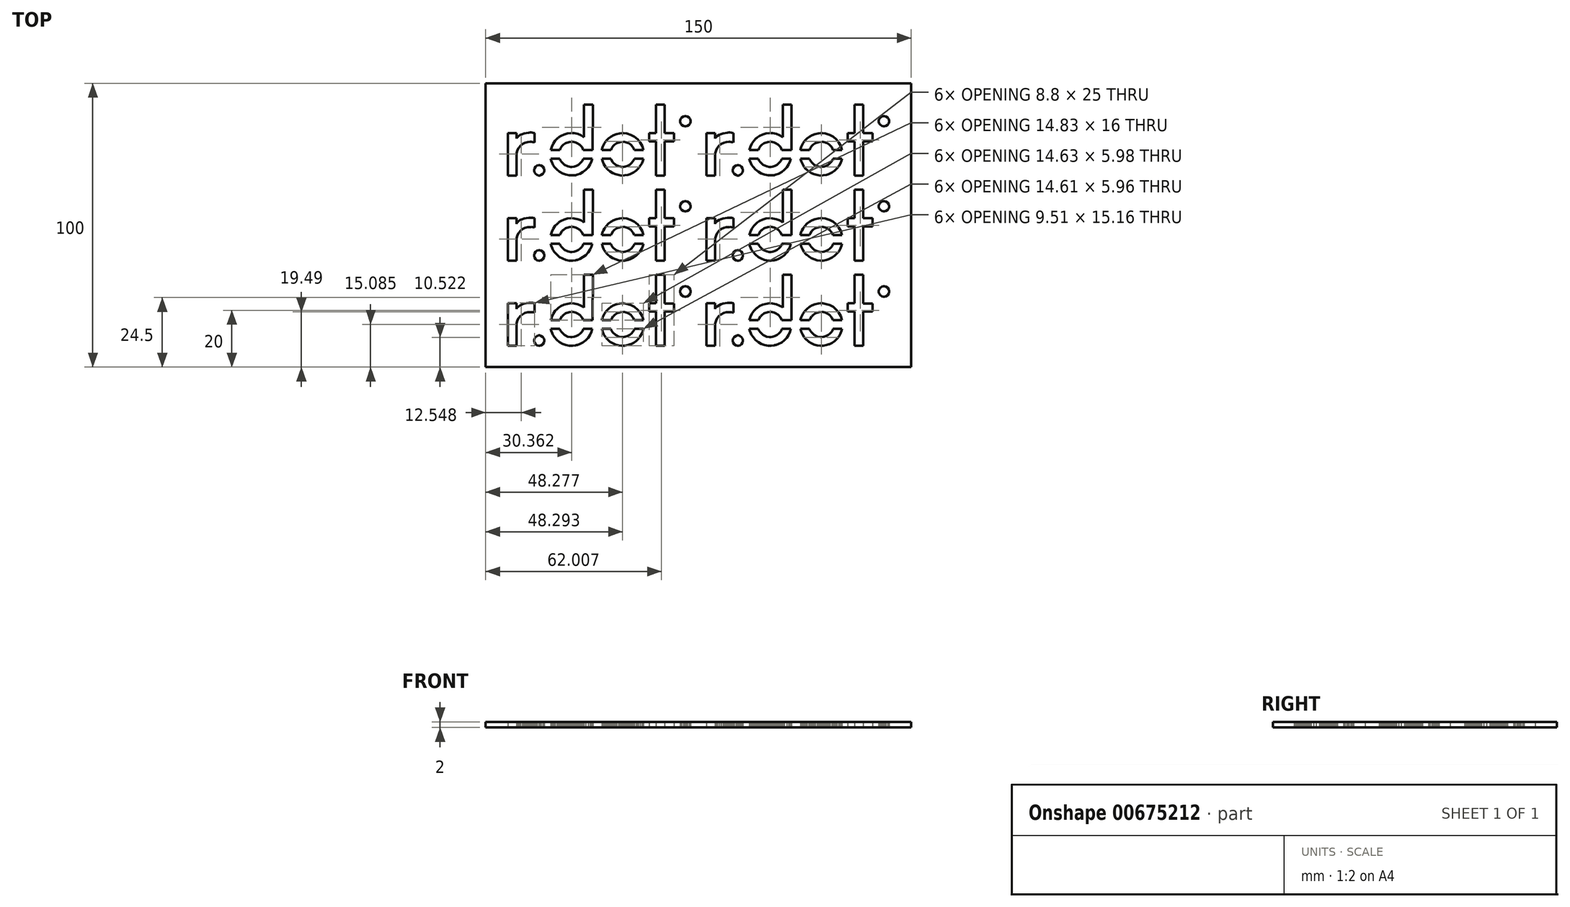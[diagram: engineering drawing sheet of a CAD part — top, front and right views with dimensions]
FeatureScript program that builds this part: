
annotation { "Feature Type Name" : "Feature", "Feature Type Description" : "" }
export const myFeature = defineFeature(function(context is Context, id is Id, definition is map)
    precondition{}
    {
        {
            var Q0;
            Q0=qCreatedBy(makeId("Top.planeOp"),FACE);
            var sketch = newSketch(context, id + "F0", { "sketchPlane" : qUnion([Q0])});
            skLineSegment(sketch, "E0", {"start": v(32.2, 6.66) * mm, "end": v(32.2, 6.49) * mm});
            skLineSegment(sketch, "E1", {"start": v(32.2, 6.49) * mm, "end": v(32.06, 5.96) * mm});
            skLineSegment(sketch, "E2", {"start": v(32.06, 5.96) * mm, "end": v(31.67, 5.38) * mm});
            skLineSegment(sketch, "E3", {"start": v(31.67, 5.38) * mm, "end": v(31.1, 5) * mm});
            skLineSegment(sketch, "E4", {"start": v(31.1, 5) * mm, "end": v(30.57, 4.85) * mm});
            skLineSegment(sketch, "E5", {"start": v(30.57, 4.85) * mm, "end": v(30.39, 4.85) * mm});
            skLineSegment(sketch, "E6", {"start": v(30.39, 4.85) * mm, "end": v(30.21, 4.85) * mm});
            skLineSegment(sketch, "E7", {"start": v(30.21, 4.85) * mm, "end": v(29.68, 5) * mm});
            skLineSegment(sketch, "E8", {"start": v(29.68, 5) * mm, "end": v(29.1, 5.38) * mm});
            skLineSegment(sketch, "E9", {"start": v(29.1, 5.38) * mm, "end": v(28.72, 5.96) * mm});
            skLineSegment(sketch, "E10", {"start": v(28.72, 5.96) * mm, "end": v(28.57, 6.49) * mm});
            skLineSegment(sketch, "E11", {"start": v(28.57, 6.49) * mm, "end": v(28.57, 6.66) * mm});
            skLineSegment(sketch, "E12", {"start": v(28.57, 6.66) * mm, "end": v(28.57, 6.84) * mm});
            skLineSegment(sketch, "E13", {"start": v(28.57, 6.84) * mm, "end": v(28.72, 7.37) * mm});
            skLineSegment(sketch, "E14", {"start": v(28.72, 7.37) * mm, "end": v(29.1, 7.95) * mm});
            skLineSegment(sketch, "E15", {"start": v(29.1, 7.95) * mm, "end": v(29.68, 8.34) * mm});
            skLineSegment(sketch, "E16", {"start": v(29.68, 8.34) * mm, "end": v(30.21, 8.48) * mm});
            skLineSegment(sketch, "E17", {"start": v(30.21, 8.48) * mm, "end": v(30.39, 8.48) * mm});
            skLineSegment(sketch, "E18", {"start": v(30.39, 8.48) * mm, "end": v(30.57, 8.48) * mm});
            skLineSegment(sketch, "E19", {"start": v(30.57, 8.48) * mm, "end": v(31.1, 8.34) * mm});
            skLineSegment(sketch, "E20", {"start": v(31.1, 8.34) * mm, "end": v(31.67, 7.95) * mm});
            skLineSegment(sketch, "E21", {"start": v(31.67, 7.95) * mm, "end": v(32.06, 7.37) * mm});
            skLineSegment(sketch, "E22", {"start": v(32.06, 7.37) * mm, "end": v(32.2, 6.84) * mm});
            skLineSegment(sketch, "E23", {"start": v(32.2, 6.84) * mm, "end": v(32.2, 6.66) * mm});
            skLineSegment(sketch, "E24", {"start": v(23.05, 12.5) * mm, "end": v(19.98, 12.5) * mm});
            skLineSegment(sketch, "E25", {"start": v(19.98, 12.5) * mm, "end": v(19.98, 2.51) * mm});
            skLineSegment(sketch, "E26", {"start": v(19.98, 2.51) * mm, "end": v(17.6, 2.51) * mm});
            skLineSegment(sketch, "E27", {"start": v(17.6, 2.51) * mm, "end": v(17.6, -0.42) * mm});
            skLineSegment(sketch, "E28", {"start": v(17.6, -0.42) * mm, "end": v(19.98, -0.42) * mm});
            skLineSegment(sketch, "E29", {"start": v(19.98, -0.42) * mm, "end": v(19.98, -12.5) * mm});
            skLineSegment(sketch, "E30", {"start": v(19.98, -12.5) * mm, "end": v(23.05, -12.5) * mm});
            skLineSegment(sketch, "E31", {"start": v(23.05, -12.5) * mm, "end": v(23.05, -0.42) * mm});
            skLineSegment(sketch, "E32", {"start": v(23.05, -0.42) * mm, "end": v(26.4, -0.42) * mm});
            skLineSegment(sketch, "E33", {"start": v(26.4, -0.42) * mm, "end": v(26.4, 2.44) * mm});
            skLineSegment(sketch, "E34", {"start": v(26.4, 2.44) * mm, "end": v(23.05, 2.44) * mm});
            skLineSegment(sketch, "E35", {"start": v(23.05, 2.44) * mm, "end": v(23.05, 12.5) * mm});
            skLineSegment(sketch, "E36", {"start": v(8.29, 2.48) * mm, "end": v(8, 2.48) * mm});
            skLineSegment(sketch, "E37", {"start": v(8, 2.48) * mm, "end": v(7.17, 2.4) * mm});
            skLineSegment(sketch, "E38", {"start": v(7.17, 2.4) * mm, "end": v(6.1, 2.15) * mm});
            skLineSegment(sketch, "E39", {"start": v(6.1, 2.15) * mm, "end": v(5.08, 1.76) * mm});
            skLineSegment(sketch, "E40", {"start": v(5.08, 1.76) * mm, "end": v(4.13, 1.22) * mm});
            skLineSegment(sketch, "E41", {"start": v(4.13, 1.22) * mm, "end": v(3.28, 0.55) * mm});
            skLineSegment(sketch, "E42", {"start": v(3.28, 0.55) * mm, "end": v(2.52, -0.23) * mm});
            skLineSegment(sketch, "E43", {"start": v(2.52, -0.23) * mm, "end": v(1.89, -1.13) * mm});
            skLineSegment(sketch, "E44", {"start": v(1.89, -1.13) * mm, "end": v(1.49, -1.87) * mm});
            skLineSegment(sketch, "E45", {"start": v(1.49, -1.87) * mm, "end": v(1.38, -2.13) * mm});
            skLineSegment(sketch, "E46", {"start": v(1.38, -2.13) * mm, "end": v(1.28, -2.4) * mm});
            skLineSegment(sketch, "E47", {"start": v(1.28, -2.4) * mm, "end": v(1.03, -3.2) * mm});
            skLineSegment(sketch, "E48", {"start": v(1.03, -3.2) * mm, "end": v(0.98, -3.5) * mm});
            skLineSegment(sketch, "E49", {"start": v(0.97, -6.5) * mm, "end": v(1.24, -7.5) * mm});
            skLineSegment(sketch, "E50", {"start": v(1.24, -7.5) * mm, "end": v(1.68, -8.5) * mm});
            skLineSegment(sketch, "E51", {"start": v(1.68, -8.5) * mm, "end": v(2.27, -9.43) * mm});
            skLineSegment(sketch, "E52", {"start": v(2.27, -9.43) * mm, "end": v(2.8, -10.08) * mm});
            skLineSegment(sketch, "E53", {"start": v(2.8, -10.08) * mm, "end": v(3, -10.28) * mm});
            skLineSegment(sketch, "E54", {"start": v(3, -10.28) * mm, "end": v(3.2, -10.47) * mm});
            skLineSegment(sketch, "E55", {"start": v(3.2, -10.47) * mm, "end": v(3.85, -11) * mm});
            skLineSegment(sketch, "E56", {"start": v(3.85, -11) * mm, "end": v(4.78, -11.6) * mm});
            skLineSegment(sketch, "E57", {"start": v(4.78, -11.6) * mm, "end": v(5.78, -12.03) * mm});
            skLineSegment(sketch, "E58", {"start": v(5.78, -12.03) * mm, "end": v(6.83, -12.32) * mm});
            skLineSegment(sketch, "E59", {"start": v(6.83, -12.32) * mm, "end": v(7.9, -12.46) * mm});
            skLineSegment(sketch, "E60", {"start": v(7.9, -12.46) * mm, "end": v(9, -12.43) * mm});
            skLineSegment(sketch, "E61", {"start": v(9, -12.43) * mm, "end": v(10.08, -12.25) * mm});
            skLineSegment(sketch, "E62", {"start": v(10.08, -12.25) * mm, "end": v(10.89, -12) * mm});
            skLineSegment(sketch, "E63", {"start": v(10.89, -12) * mm, "end": v(11.14, -11.9) * mm});
            skLineSegment(sketch, "E64", {"start": v(11.14, -11.9) * mm, "end": v(11.4, -11.79) * mm});
            skLineSegment(sketch, "E65", {"start": v(11.4, -11.79) * mm, "end": v(12.14, -11.4) * mm});
            skLineSegment(sketch, "E66", {"start": v(12.14, -11.4) * mm, "end": v(13.04, -10.75) * mm});
            skLineSegment(sketch, "E67", {"start": v(13.04, -10.75) * mm, "end": v(13.83, -10) * mm});
            skLineSegment(sketch, "E68", {"start": v(13.83, -10) * mm, "end": v(14.5, -9.14) * mm});
            skLineSegment(sketch, "E69", {"start": v(14.5, -9.14) * mm, "end": v(15.03, -8.2) * mm});
            skLineSegment(sketch, "E70", {"start": v(15.03, -8.2) * mm, "end": v(15.43, -7.18) * mm});
            skLineSegment(sketch, "E71", {"start": v(15.43, -7.18) * mm, "end": v(15.58, -6.5) * mm});
            skLineSegment(sketch, "E72", {"start": v(15.6, -3.5) * mm, "end": v(15.6, -3.49) * mm});
            skLineSegment(sketch, "E73", {"start": v(15.6, -3.49) * mm, "end": v(15.17, -2.08) * mm});
            skLineSegment(sketch, "E74", {"start": v(15.17, -2.08) * mm, "end": v(14.48, -0.82) * mm});
            skLineSegment(sketch, "E75", {"start": v(14.48, -0.82) * mm, "end": v(13.57, 0.3) * mm});
            skLineSegment(sketch, "E76", {"start": v(13.57, 0.3) * mm, "end": v(12.46, 1.2) * mm});
            skLineSegment(sketch, "E77", {"start": v(12.46, 1.2) * mm, "end": v(11.2, 1.9) * mm});
            skLineSegment(sketch, "E78", {"start": v(11.2, 1.9) * mm, "end": v(9.8, 2.33) * mm});
            skLineSegment(sketch, "E79", {"start": v(9.8, 2.33) * mm, "end": v(8.66, 2.48) * mm});
            skLineSegment(sketch, "E80", {"start": v(8.66, 2.48) * mm, "end": v(8.29, 2.48) * mm});
            skLineSegment(sketch, "E81", {"start": v(8.29, -9.43) * mm, "end": v(7.96, -9.43) * mm});
            skLineSegment(sketch, "E82", {"start": v(7.96, -9.43) * mm, "end": v(6.99, -9.23) * mm});
            skLineSegment(sketch, "E83", {"start": v(6.99, -9.23) * mm, "end": v(5.82, -8.68) * mm});
            skLineSegment(sketch, "E84", {"start": v(5.82, -8.68) * mm, "end": v(4.87, -7.82) * mm});
            skLineSegment(sketch, "E85", {"start": v(4.87, -7.82) * mm, "end": v(4.31, -6.99) * mm});
            skLineSegment(sketch, "E86", {"start": v(4.31, -6.99) * mm, "end": v(4.19, -6.69) * mm});
            skLineSegment(sketch, "E87", {"start": v(4.19, -6.69) * mm, "end": v(4.11, -6.5) * mm});
            skLineSegment(sketch, "E88", {"start": v(4.16, -3.5) * mm, "end": v(4.37, -2.91) * mm});
            skLineSegment(sketch, "E89", {"start": v(4.37, -2.91) * mm, "end": v(4.92, -2.09) * mm});
            skLineSegment(sketch, "E90", {"start": v(4.92, -2.09) * mm, "end": v(5.15, -1.86) * mm});
            skLineSegment(sketch, "E91", {"start": v(5.15, -1.86) * mm, "end": v(5.38, -1.63) * mm});
            skLineSegment(sketch, "E92", {"start": v(5.38, -1.63) * mm, "end": v(6.2, -1.08) * mm});
            skLineSegment(sketch, "E93", {"start": v(6.2, -1.08) * mm, "end": v(7.42, -0.64) * mm});
            skLineSegment(sketch, "E94", {"start": v(7.42, -0.64) * mm, "end": v(8.7, -0.58) * mm});
            skLineSegment(sketch, "E95", {"start": v(8.7, -0.58) * mm, "end": v(9.68, -0.77) * mm});
            skLineSegment(sketch, "E96", {"start": v(9.68, -0.77) * mm, "end": v(9.98, -0.9) * mm});
            skLineSegment(sketch, "E97", {"start": v(9.98, -0.9) * mm, "end": v(10.28, -1.02) * mm});
            skLineSegment(sketch, "E98", {"start": v(10.28, -1.02) * mm, "end": v(11.1, -1.57) * mm});
            skLineSegment(sketch, "E99", {"start": v(11.1, -1.57) * mm, "end": v(11.97, -2.53) * mm});
            skLineSegment(sketch, "E100", {"start": v(11.97, -2.53) * mm, "end": v(12.43, -3.5) * mm});
            skLineSegment(sketch, "E101", {"start": v(12.44, -6.5) * mm, "end": v(12.37, -6.72) * mm});
            skLineSegment(sketch, "E102", {"start": v(12.37, -6.72) * mm, "end": v(11.96, -7.47) * mm});
            skLineSegment(sketch, "E103", {"start": v(11.96, -7.47) * mm, "end": v(11.42, -8.13) * mm});
            skLineSegment(sketch, "E104", {"start": v(11.42, -8.13) * mm, "end": v(10.76, -8.67) * mm});
            skLineSegment(sketch, "E105", {"start": v(10.76, -8.67) * mm, "end": v(10.01, -9.08) * mm});
            skLineSegment(sketch, "E106", {"start": v(10.01, -9.08) * mm, "end": v(9.18, -9.34) * mm});
            skLineSegment(sketch, "E107", {"start": v(9.18, -9.34) * mm, "end": v(8.5, -9.43) * mm});
            skLineSegment(sketch, "E108", {"start": v(8.5, -9.43) * mm, "end": v(8.29, -9.43) * mm});
            skLineSegment(sketch, "E109", {"start": v(-2.22, 12.5) * mm, "end": v(-5.3, 12.5) * mm});
            skLineSegment(sketch, "E110", {"start": v(-5.3, 12.5) * mm, "end": v(-5.3, 1.02) * mm});
            skLineSegment(sketch, "E111", {"start": v(-5.3, 1.02) * mm, "end": v(-5.55, 1.21) * mm});
            skLineSegment(sketch, "E112", {"start": v(-5.55, 1.21) * mm, "end": v(-6.39, 1.69) * mm});
            skLineSegment(sketch, "E113", {"start": v(-6.39, 1.69) * mm, "end": v(-7.55, 2.15) * mm});
            skLineSegment(sketch, "E114", {"start": v(-7.55, 2.15) * mm, "end": v(-8.75, 2.42) * mm});
            skLineSegment(sketch, "E115", {"start": v(-8.75, 2.42) * mm, "end": v(-9.98, 2.48) * mm});
            skLineSegment(sketch, "E116", {"start": v(-9.98, 2.48) * mm, "end": v(-11.2, 2.33) * mm});
            skLineSegment(sketch, "E117", {"start": v(-11.2, 2.33) * mm, "end": v(-12.38, 2) * mm});
            skLineSegment(sketch, "E118", {"start": v(-12.38, 2) * mm, "end": v(-13.51, 1.45) * mm});
            skLineSegment(sketch, "E119", {"start": v(-13.51, 1.45) * mm, "end": v(-14.31, 0.92) * mm});
            skLineSegment(sketch, "E120", {"start": v(-14.31, 0.92) * mm, "end": v(-14.55, 0.71) * mm});
            skLineSegment(sketch, "E121", {"start": v(-14.55, 0.71) * mm, "end": v(-14.8, 0.5) * mm});
            skLineSegment(sketch, "E122", {"start": v(-14.8, 0.5) * mm, "end": v(-15.46, -0.19) * mm});
            skLineSegment(sketch, "E123", {"start": v(-15.46, -0.19) * mm, "end": v(-16.18, -1.21) * mm});
            skLineSegment(sketch, "E124", {"start": v(-16.18, -1.21) * mm, "end": v(-16.71, -2.32) * mm});
            skLineSegment(sketch, "E125", {"start": v(-16.71, -2.32) * mm, "end": v(-17.05, -3.5) * mm});
            skLineSegment(sketch, "E126", {"start": v(-17.02, -6.5) * mm, "end": v(-16.88, -7.18) * mm});
            skLineSegment(sketch, "E127", {"start": v(-16.88, -7.18) * mm, "end": v(-16.54, -8.08) * mm});
            skLineSegment(sketch, "E128", {"start": v(-16.54, -8.08) * mm, "end": v(-16.4, -8.36) * mm});
            skLineSegment(sketch, "E129", {"start": v(-16.4, -8.36) * mm, "end": v(-16.26, -8.65) * mm});
            skLineSegment(sketch, "E130", {"start": v(-16.26, -8.65) * mm, "end": v(-15.73, -9.45) * mm});
            skLineSegment(sketch, "E131", {"start": v(-15.73, -9.45) * mm, "end": v(-14.9, -10.39) * mm});
            skLineSegment(sketch, "E132", {"start": v(-14.9, -10.39) * mm, "end": v(-13.94, -11.16) * mm});
            skLineSegment(sketch, "E133", {"start": v(-13.94, -11.16) * mm, "end": v(-12.88, -11.77) * mm});
            skLineSegment(sketch, "E134", {"start": v(-12.88, -11.77) * mm, "end": v(-11.73, -12.2) * mm});
            skLineSegment(sketch, "E135", {"start": v(-11.73, -12.2) * mm, "end": v(-10.51, -12.42) * mm});
            skLineSegment(sketch, "E136", {"start": v(-10.51, -12.42) * mm, "end": v(-9.26, -12.45) * mm});
            skLineSegment(sketch, "E137", {"start": v(-9.26, -12.45) * mm, "end": v(-8.3, -12.34) * mm});
            skLineSegment(sketch, "E138", {"start": v(-8.3, -12.34) * mm, "end": v(-8, -12.26) * mm});
            skLineSegment(sketch, "E139", {"start": v(-8, -12.26) * mm, "end": v(-7.7, -12.19) * mm});
            skLineSegment(sketch, "E140", {"start": v(-7.7, -12.19) * mm, "end": v(-6.79, -11.86) * mm});
            skLineSegment(sketch, "E141", {"start": v(-6.79, -11.86) * mm, "end": v(-5.68, -11.27) * mm});
            skLineSegment(sketch, "E142", {"start": v(-5.68, -11.27) * mm, "end": v(-4.7, -10.52) * mm});
            skLineSegment(sketch, "E143", {"start": v(-4.7, -10.52) * mm, "end": v(-3.87, -9.62) * mm});
            skLineSegment(sketch, "E144", {"start": v(-3.87, -9.62) * mm, "end": v(-3.19, -8.6) * mm});
            skLineSegment(sketch, "E145", {"start": v(-3.19, -8.6) * mm, "end": v(-2.68, -7.48) * mm});
            skLineSegment(sketch, "E146", {"start": v(-2.68, -7.48) * mm, "end": v(-2.43, -6.5) * mm});
            skLineSegment(sketch, "E147", {"start": v(-2.26, -3.5) * mm, "end": v(-2.22, 12.5) * mm});
            skLineSegment(sketch, "E148", {"start": v(-9.73, -9.43) * mm, "end": v(-10.06, -9.43) * mm});
            skLineSegment(sketch, "E149", {"start": v(-10.06, -9.43) * mm, "end": v(-11.03, -9.24) * mm});
            skLineSegment(sketch, "E150", {"start": v(-11.03, -9.24) * mm, "end": v(-12.2, -8.68) * mm});
            skLineSegment(sketch, "E151", {"start": v(-12.2, -8.68) * mm, "end": v(-13.15, -7.82) * mm});
            skLineSegment(sketch, "E152", {"start": v(-13.15, -7.82) * mm, "end": v(-13.7, -7) * mm});
            skLineSegment(sketch, "E153", {"start": v(-13.7, -7) * mm, "end": v(-13.83, -6.7) * mm});
            skLineSegment(sketch, "E154", {"start": v(-13.83, -6.7) * mm, "end": v(-13.95, -6.4) * mm});
            skLineSegment(sketch, "E155", {"start": v(-13.85, -3.5) * mm, "end": v(-13.65, -2.92) * mm});
            skLineSegment(sketch, "E156", {"start": v(-13.65, -2.92) * mm, "end": v(-13.1, -2.1) * mm});
            skLineSegment(sketch, "E157", {"start": v(-13.1, -2.1) * mm, "end": v(-12.87, -1.86) * mm});
            skLineSegment(sketch, "E158", {"start": v(-12.87, -1.86) * mm, "end": v(-12.64, -1.63) * mm});
            skLineSegment(sketch, "E159", {"start": v(-12.64, -1.63) * mm, "end": v(-11.8, -1.08) * mm});
            skLineSegment(sketch, "E160", {"start": v(-11.8, -1.08) * mm, "end": v(-10.6, -0.65) * mm});
            skLineSegment(sketch, "E161", {"start": v(-10.6, -0.65) * mm, "end": v(-9.3, -0.58) * mm});
            skLineSegment(sketch, "E162", {"start": v(-9.3, -0.58) * mm, "end": v(-8.33, -0.78) * mm});
            skLineSegment(sketch, "E163", {"start": v(-8.33, -0.78) * mm, "end": v(-8.03, -0.9) * mm});
            skLineSegment(sketch, "E164", {"start": v(-8.03, -0.9) * mm, "end": v(-7.73, -1.02) * mm});
            skLineSegment(sketch, "E165", {"start": v(-7.73, -1.02) * mm, "end": v(-6.9, -1.58) * mm});
            skLineSegment(sketch, "E166", {"start": v(-6.9, -1.58) * mm, "end": v(-6.04, -2.53) * mm});
            skLineSegment(sketch, "E167", {"start": v(-6.04, -2.53) * mm, "end": v(-5.58, -3.5) * mm});
            skLineSegment(sketch, "E168", {"start": v(-5.58, -6.5) * mm, "end": v(-5.65, -6.72) * mm});
            skLineSegment(sketch, "E169", {"start": v(-5.65, -6.72) * mm, "end": v(-6.06, -7.47) * mm});
            skLineSegment(sketch, "E170", {"start": v(-6.06, -7.47) * mm, "end": v(-6.6, -8.13) * mm});
            skLineSegment(sketch, "E171", {"start": v(-6.6, -8.13) * mm, "end": v(-7.25, -8.67) * mm});
            skLineSegment(sketch, "E172", {"start": v(-7.25, -8.67) * mm, "end": v(-8, -9.08) * mm});
            skLineSegment(sketch, "E173", {"start": v(-8, -9.08) * mm, "end": v(-8.84, -9.34) * mm});
            skLineSegment(sketch, "E174", {"start": v(-8.84, -9.34) * mm, "end": v(-9.5, -9.43) * mm});
            skLineSegment(sketch, "E175", {"start": v(-9.5, -9.43) * mm, "end": v(-9.73, -9.43) * mm});
            skLineSegment(sketch, "E176", {"start": v(-9.73, -9.43) * mm, "end": v(-9.73, -9.43) * mm});
            skLineSegment(sketch, "E177", {"start": v(-19.3, -10.65) * mm, "end": v(-19.3, -10.83) * mm});
            skLineSegment(sketch, "E178", {"start": v(-19.3, -10.83) * mm, "end": v(-19.44, -11.36) * mm});
            skLineSegment(sketch, "E179", {"start": v(-19.44, -11.36) * mm, "end": v(-19.83, -11.93) * mm});
            skLineSegment(sketch, "E180", {"start": v(-19.83, -11.93) * mm, "end": v(-20.4, -12.32) * mm});
            skLineSegment(sketch, "E181", {"start": v(-20.4, -12.32) * mm, "end": v(-20.94, -12.47) * mm});
            skLineSegment(sketch, "E182", {"start": v(-20.94, -12.47) * mm, "end": v(-21.11, -12.47) * mm});
            skLineSegment(sketch, "E183", {"start": v(-21.11, -12.47) * mm, "end": v(-21.29, -12.47) * mm});
            skLineSegment(sketch, "E184", {"start": v(-21.29, -12.47) * mm, "end": v(-21.82, -12.32) * mm});
            skLineSegment(sketch, "E185", {"start": v(-21.82, -12.32) * mm, "end": v(-22.4, -11.93) * mm});
            skLineSegment(sketch, "E186", {"start": v(-22.4, -11.93) * mm, "end": v(-22.79, -11.36) * mm});
            skLineSegment(sketch, "E187", {"start": v(-22.79, -11.36) * mm, "end": v(-22.93, -10.83) * mm});
            skLineSegment(sketch, "E188", {"start": v(-22.93, -10.83) * mm, "end": v(-22.93, -10.65) * mm});
            skLineSegment(sketch, "E189", {"start": v(-22.93, -10.65) * mm, "end": v(-22.93, -10.47) * mm});
            skLineSegment(sketch, "E190", {"start": v(-22.93, -10.47) * mm, "end": v(-22.79, -9.94) * mm});
            skLineSegment(sketch, "E191", {"start": v(-22.79, -9.94) * mm, "end": v(-22.4, -9.37) * mm});
            skLineSegment(sketch, "E192", {"start": v(-22.4, -9.37) * mm, "end": v(-21.82, -8.98) * mm});
            skLineSegment(sketch, "E193", {"start": v(-21.82, -8.98) * mm, "end": v(-21.29, -8.83) * mm});
            skLineSegment(sketch, "E194", {"start": v(-21.29, -8.83) * mm, "end": v(-21.11, -8.83) * mm});
            skLineSegment(sketch, "E195", {"start": v(-21.11, -8.83) * mm, "end": v(-20.94, -8.83) * mm});
            skLineSegment(sketch, "E196", {"start": v(-20.94, -8.83) * mm, "end": v(-20.4, -8.98) * mm});
            skLineSegment(sketch, "E197", {"start": v(-20.4, -8.98) * mm, "end": v(-19.83, -9.37) * mm});
            skLineSegment(sketch, "E198", {"start": v(-19.83, -9.37) * mm, "end": v(-19.44, -9.94) * mm});
            skLineSegment(sketch, "E199", {"start": v(-19.44, -9.94) * mm, "end": v(-19.3, -10.47) * mm});
            skLineSegment(sketch, "E200", {"start": v(-19.3, -10.47) * mm, "end": v(-19.3, -10.65) * mm});
            skLineSegment(sketch, "E201", {"start": v(-22.7, -0.77) * mm, "end": v(-22.81, -0.75) * mm});
            skLineSegment(sketch, "E202", {"start": v(-22.81, -0.75) * mm, "end": v(-23.38, -0.65) * mm});
            skLineSegment(sketch, "E203", {"start": v(-23.38, -0.65) * mm, "end": v(-23.96, -0.61) * mm});
            skLineSegment(sketch, "E204", {"start": v(-23.96, -0.61) * mm, "end": v(-24.08, -0.61) * mm});
            skLineSegment(sketch, "E205", {"start": v(-24.08, -0.61) * mm, "end": v(-24.35, -0.61) * mm});
            skLineSegment(sketch, "E206", {"start": v(-24.35, -0.61) * mm, "end": v(-25.16, -0.7) * mm});
            skLineSegment(sketch, "E207", {"start": v(-25.16, -0.7) * mm, "end": v(-26.13, -0.94) * mm});
            skLineSegment(sketch, "E208", {"start": v(-26.13, -0.94) * mm, "end": v(-27, -1.35) * mm});
            skLineSegment(sketch, "E209", {"start": v(-27, -1.35) * mm, "end": v(-27.74, -1.93) * mm});
            skLineSegment(sketch, "E210", {"start": v(-27.74, -1.93) * mm, "end": v(-28.34, -2.69) * mm});
            skLineSegment(sketch, "E211", {"start": v(-28.34, -2.69) * mm, "end": v(-28.8, -3.62) * mm});
            skLineSegment(sketch, "E212", {"start": v(-28.8, -3.62) * mm, "end": v(-29.07, -4.74) * mm});
            skLineSegment(sketch, "E213", {"start": v(-29.07, -4.74) * mm, "end": v(-29.17, -5.72) * mm});
            skLineSegment(sketch, "E214", {"start": v(-29.17, -5.72) * mm, "end": v(-29.17, -6.04) * mm});
            skLineSegment(sketch, "E215", {"start": v(-29.17, -6.04) * mm, "end": v(-29.17, -12.5) * mm});
            skLineSegment(sketch, "E216", {"start": v(-29.17, -12.5) * mm, "end": v(-32.2, -12.5) * mm});
            skLineSegment(sketch, "E217", {"start": v(-32.2, -12.5) * mm, "end": v(-32.2, 2.47) * mm});
            skLineSegment(sketch, "E218", {"start": v(-32.2, 2.47) * mm, "end": v(-29.17, 2.47) * mm});
            skLineSegment(sketch, "E219", {"start": v(-29.17, 2.47) * mm, "end": v(-29.17, 0.52) * mm});
            skLineSegment(sketch, "E220", {"start": v(-29.17, 0.52) * mm, "end": v(-29.1, 0.65) * mm});
            skLineSegment(sketch, "E221", {"start": v(-29.1, 0.65) * mm, "end": v(-28.84, 1) * mm});
            skLineSegment(sketch, "E222", {"start": v(-28.84, 1) * mm, "end": v(-28.37, 1.44) * mm});
            skLineSegment(sketch, "E223", {"start": v(-28.37, 1.44) * mm, "end": v(-27.79, 1.8) * mm});
            skLineSegment(sketch, "E224", {"start": v(-27.79, 1.8) * mm, "end": v(-27.12, 2.1) * mm});
            skLineSegment(sketch, "E225", {"start": v(-27.12, 2.1) * mm, "end": v(-26.39, 2.35) * mm});
            skLineSegment(sketch, "E226", {"start": v(-26.39, 2.35) * mm, "end": v(-25.62, 2.52) * mm});
            skLineSegment(sketch, "E227", {"start": v(-25.62, 2.52) * mm, "end": v(-24.84, 2.63) * mm});
            skLineSegment(sketch, "E228", {"start": v(-24.84, 2.63) * mm, "end": v(-24.27, 2.66) * mm});
            skLineSegment(sketch, "E229", {"start": v(-24.27, 2.66) * mm, "end": v(-24.08, 2.66) * mm});
            skLineSegment(sketch, "E230", {"start": v(-24.08, 2.66) * mm, "end": v(-23.9, 2.66) * mm});
            skLineSegment(sketch, "E231", {"start": v(-23.9, 2.66) * mm, "end": v(-23.33, 2.61) * mm});
            skLineSegment(sketch, "E232", {"start": v(-23.33, 2.61) * mm, "end": v(-22.8, 2.48) * mm});
            skLineSegment(sketch, "E233", {"start": v(-22.8, 2.48) * mm, "end": v(-22.7, 2.44) * mm});
            skLineSegment(sketch, "E234", {"start": v(-22.7, 2.44) * mm, "end": v(-22.7, -0.77) * mm});
            skLineSegment(sketch, "E235", {"start": v(-17.02, -6.5) * mm, "end": v(-13.9, -6.5) * mm});
            skLineSegment(sketch, "E236", {"start": v(-17.05, -3.5) * mm, "end": v(-13.85, -3.5) * mm});
            skLineSegment(sketch, "E237.trimOffspring", {"start": v(-5.58, -6.5) * mm, "end": v(-2.43, -6.5) * mm});
            skLineSegment(sketch, "E238.trimOffspring", {"start": v(-5.58, -3.5) * mm, "end": v(-2.26, -3.5) * mm});
            skLineSegment(sketch, "E239.trimOffspring", {"start": v(12.43, -3.5) * mm, "end": v(15.6, -3.5) * mm});
            skLineSegment(sketch, "E240.trimOffspring", {"start": v(12.44, -6.5) * mm, "end": v(15.58, -6.5) * mm});
            skLineSegment(sketch, "E241.trimOffspring", {"start": v(0.98, -3.5) * mm, "end": v(4.16, -3.5) * mm});
            skLineSegment(sketch, "E242.trimOffspring", {"start": v(0.97, -6.5) * mm, "end": v(4.11, -6.5) * mm});
            skLineSegment(sketch, "E243.0.1.0", {"start": v(19.98, 29.58) * mm, "end": v(19.98, 17.5) * mm});
            skLineSegment(sketch, "E243.0.1.1", {"start": v(19.98, 42.5) * mm, "end": v(19.98, 32.51) * mm});
            skLineSegment(sketch, "E243.0.1.2", {"start": v(-22.7, 32.44) * mm, "end": v(-22.7, 29.23) * mm});
            skLineSegment(sketch, "E243.0.1.3", {"start": v(26.4, 29.58) * mm, "end": v(26.4, 32.44) * mm});
            skLineSegment(sketch, "E243.0.1.4", {"start": v(26.4, 32.44) * mm, "end": v(23.05, 32.44) * mm});
            skLineSegment(sketch, "E243.0.1.5", {"start": v(12.43, 26.5) * mm, "end": v(15.6, 26.5) * mm});
            skLineSegment(sketch, "E243.0.1.6", {"start": v(-17.05, 26.5) * mm, "end": v(-13.85, 26.5) * mm});
            skLineSegment(sketch, "E243.0.1.7", {"start": v(-32.2, 17.5) * mm, "end": v(-32.2, 32.47) * mm});
            skLineSegment(sketch, "E243.0.1.8", {"start": v(-29.17, 23.96) * mm, "end": v(-29.17, 17.5) * mm});
            skLineSegment(sketch, "E243.0.1.9", {"start": v(0.98, 26.5) * mm, "end": v(4.16, 26.5) * mm});
            skLineSegment(sketch, "E243.0.1.10", {"start": v(0.97, 23.5) * mm, "end": v(4.11, 23.5) * mm});
            skLineSegment(sketch, "E243.0.1.11", {"start": v(12.44, 23.5) * mm, "end": v(15.58, 23.5) * mm});
            skLineSegment(sketch, "E243.0.1.12", {"start": v(-5.3, 42.5) * mm, "end": v(-5.3, 31.02) * mm});
            skLineSegment(sketch, "E243.0.1.13", {"start": v(23.05, 17.5) * mm, "end": v(23.05, 29.58) * mm});
            skLineSegment(sketch, "E243.0.1.14", {"start": v(-32.2, 32.47) * mm, "end": v(-29.17, 32.47) * mm});
            skLineSegment(sketch, "E243.0.1.15", {"start": v(-29.17, 17.5) * mm, "end": v(-32.2, 17.5) * mm});
            skLineSegment(sketch, "E243.0.1.16", {"start": v(17.6, 32.51) * mm, "end": v(17.6, 29.58) * mm});
            skLineSegment(sketch, "E243.0.1.17", {"start": v(-2.26, 26.5) * mm, "end": v(-2.22, 42.5) * mm});
            skLineSegment(sketch, "E243.0.1.18", {"start": v(-2.22, 42.5) * mm, "end": v(-5.3, 42.5) * mm});
            skLineSegment(sketch, "E243.0.1.19", {"start": v(19.98, 17.5) * mm, "end": v(23.05, 17.5) * mm});
            skLineSegment(sketch, "E243.0.1.20", {"start": v(-5.58, 23.5) * mm, "end": v(-2.43, 23.5) * mm});
            skLineSegment(sketch, "E243.0.1.21", {"start": v(-17.02, 23.5) * mm, "end": v(-13.9, 23.5) * mm});
            skLineSegment(sketch, "E243.0.1.22", {"start": v(23.05, 42.5) * mm, "end": v(19.98, 42.5) * mm});
            skLineSegment(sketch, "E243.0.1.23", {"start": v(23.05, 32.44) * mm, "end": v(23.05, 42.5) * mm});
            skLineSegment(sketch, "E243.0.1.24", {"start": v(-5.58, 26.5) * mm, "end": v(-2.26, 26.5) * mm});
            skLineSegment(sketch, "E243.0.1.25", {"start": v(23.05, 29.58) * mm, "end": v(26.4, 29.58) * mm});
            skLineSegment(sketch, "E243.0.1.26", {"start": v(-4.7, 19.48) * mm, "end": v(-3.87, 20.38) * mm});
            skLineSegment(sketch, "E243.0.1.27", {"start": v(-16.71, 27.68) * mm, "end": v(-17.05, 26.5) * mm});
            skLineSegment(sketch, "E243.0.1.28", {"start": v(29.1, 37.95) * mm, "end": v(29.68, 38.34) * mm});
            skLineSegment(sketch, "E243.0.1.29", {"start": v(-13.83, 23.3) * mm, "end": v(-13.95, 23.6) * mm});
            skLineSegment(sketch, "E243.0.1.30", {"start": v(5.82, 21.32) * mm, "end": v(4.87, 22.18) * mm});
            skLineSegment(sketch, "E243.0.1.31", {"start": v(-3.19, 21.4) * mm, "end": v(-2.68, 22.52) * mm});
            skLineSegment(sketch, "E243.0.1.32", {"start": v(17.6, 29.58) * mm, "end": v(19.98, 29.58) * mm});
            skLineSegment(sketch, "E243.0.1.33", {"start": v(-6.79, 18.14) * mm, "end": v(-5.68, 18.73) * mm});
            skLineSegment(sketch, "E243.0.1.34", {"start": v(7.42, 29.36) * mm, "end": v(8.7, 29.42) * mm});
            skLineSegment(sketch, "E243.0.1.35", {"start": v(4.78, 18.4) * mm, "end": v(5.78, 17.97) * mm});
            skLineSegment(sketch, "E243.0.1.36", {"start": v(-6.06, 22.53) * mm, "end": v(-6.6, 21.87) * mm});
            skLineSegment(sketch, "E243.0.1.37", {"start": v(15.17, 27.92) * mm, "end": v(14.48, 29.18) * mm});
            skLineSegment(sketch, "E243.0.1.38", {"start": v(14.5, 20.86) * mm, "end": v(15.03, 21.8) * mm});
            skLineSegment(sketch, "E243.0.1.39", {"start": v(1.68, 21.5) * mm, "end": v(2.27, 20.57) * mm});
            skLineSegment(sketch, "E243.0.1.40", {"start": v(-27.74, 28.07) * mm, "end": v(-28.34, 27.31) * mm});
            skLineSegment(sketch, "E243.0.1.41", {"start": v(-27, 28.65) * mm, "end": v(-27.74, 28.07) * mm});
            skLineSegment(sketch, "E243.0.1.42", {"start": v(-3.87, 20.38) * mm, "end": v(-3.19, 21.4) * mm});
            skLineSegment(sketch, "E243.0.1.43", {"start": v(9.8, 32.33) * mm, "end": v(8.66, 32.48) * mm});
            skLineSegment(sketch, "E243.0.1.44", {"start": v(-2.68, 22.52) * mm, "end": v(-2.43, 23.5) * mm});
            skLineSegment(sketch, "E243.0.1.45", {"start": v(-6.6, 21.87) * mm, "end": v(-7.25, 21.33) * mm});
            skLineSegment(sketch, "E243.0.1.46", {"start": v(14.48, 29.18) * mm, "end": v(13.57, 30.3) * mm});
            skLineSegment(sketch, "E243.0.1.47", {"start": v(19.98, 32.51) * mm, "end": v(17.6, 32.51) * mm});
            skLineSegment(sketch, "E243.0.1.48", {"start": v(-11.03, 20.76) * mm, "end": v(-12.2, 21.32) * mm});
            skLineSegment(sketch, "E243.0.1.49", {"start": v(31.67, 37.95) * mm, "end": v(32.06, 37.37) * mm});
            skLineSegment(sketch, "E243.0.1.50", {"start": v(6.99, 20.77) * mm, "end": v(5.82, 21.32) * mm});
            skLineSegment(sketch, "E243.0.1.51", {"start": v(1.24, 22.5) * mm, "end": v(1.68, 21.5) * mm});
            skLineSegment(sketch, "E243.0.1.52", {"start": v(-26.39, 32.35) * mm, "end": v(-25.62, 32.52) * mm});
            skLineSegment(sketch, "E243.0.1.53", {"start": v(11.14, 18.1) * mm, "end": v(11.4, 18.21) * mm});
            skLineSegment(sketch, "E243.0.1.54", {"start": v(5.15, 28.14) * mm, "end": v(5.38, 28.37) * mm});
            skLineSegment(sketch, "E243.0.1.55", {"start": v(-12.64, 28.37) * mm, "end": v(-11.8, 28.92) * mm});
            skLineSegment(sketch, "E243.0.1.56", {"start": v(-16.26, 21.35) * mm, "end": v(-15.73, 20.55) * mm});
            skLineSegment(sketch, "E243.0.1.57", {"start": v(-29.17, 30.52) * mm, "end": v(-29.1, 30.65) * mm});
            skLineSegment(sketch, "E243.0.1.58", {"start": v(10.01, 20.92) * mm, "end": v(9.18, 20.66) * mm});
            skLineSegment(sketch, "E243.0.1.59", {"start": v(3.28, 30.55) * mm, "end": v(2.52, 29.77) * mm});
            skLineSegment(sketch, "E243.0.1.60", {"start": v(5.78, 17.97) * mm, "end": v(6.83, 17.68) * mm});
            skLineSegment(sketch, "E243.0.1.61", {"start": v(15.03, 21.8) * mm, "end": v(15.43, 22.82) * mm});
            skLineSegment(sketch, "E243.0.1.62", {"start": v(-13.15, 22.18) * mm, "end": v(-13.7, 23) * mm});
            skLineSegment(sketch, "E243.0.1.63", {"start": v(11.42, 21.87) * mm, "end": v(10.76, 21.33) * mm});
            skLineSegment(sketch, "E243.0.1.64", {"start": v(-10.51, 17.58) * mm, "end": v(-9.26, 17.55) * mm});
            skLineSegment(sketch, "E243.0.1.65", {"start": v(11.97, 27.47) * mm, "end": v(12.43, 26.5) * mm});
            skLineSegment(sketch, "E243.0.1.66", {"start": v(-28.8, 26.38) * mm, "end": v(-29.07, 25.26) * mm});
            skLineSegment(sketch, "E243.0.1.67", {"start": v(10.28, 28.98) * mm, "end": v(11.1, 28.43) * mm});
            skLineSegment(sketch, "E243.0.1.68", {"start": v(9.98, 29.1) * mm, "end": v(10.28, 28.98) * mm});
            skLineSegment(sketch, "E243.0.1.69", {"start": v(-22.4, 20.63) * mm, "end": v(-21.82, 21.02) * mm});
            skLineSegment(sketch, "E243.0.1.70", {"start": v(-7.55, 32.15) * mm, "end": v(-8.75, 32.42) * mm});
            skLineSegment(sketch, "E243.0.1.71", {"start": v(10.08, 17.75) * mm, "end": v(10.89, 18) * mm});
            skLineSegment(sketch, "E243.0.1.72", {"start": v(9, 17.57) * mm, "end": v(10.08, 17.75) * mm});
            skLineSegment(sketch, "E243.0.1.73", {"start": v(-7.25, 21.33) * mm, "end": v(-8, 20.92) * mm});
            skLineSegment(sketch, "E243.0.1.74", {"start": v(5.38, 28.37) * mm, "end": v(6.2, 28.92) * mm});
            skLineSegment(sketch, "E243.0.1.75", {"start": v(4.13, 31.22) * mm, "end": v(3.28, 30.55) * mm});
            skLineSegment(sketch, "E243.0.1.76", {"start": v(6.83, 17.68) * mm, "end": v(7.9, 17.54) * mm});
            skLineSegment(sketch, "E243.0.1.77", {"start": v(-22.4, 18.07) * mm, "end": v(-22.79, 18.64) * mm});
            skLineSegment(sketch, "E243.0.1.78", {"start": v(6.1, 32.15) * mm, "end": v(5.08, 31.76) * mm});
            skLineSegment(sketch, "E243.0.1.79", {"start": v(-6.9, 28.42) * mm, "end": v(-6.04, 27.47) * mm});
            skLineSegment(sketch, "E243.0.1.80", {"start": v(5.08, 31.76) * mm, "end": v(4.13, 31.22) * mm});
            skLineSegment(sketch, "E243.0.1.81", {"start": v(-6.04, 27.47) * mm, "end": v(-5.58, 26.5) * mm});
            skLineSegment(sketch, "E243.0.1.82", {"start": v(-15.73, 20.55) * mm, "end": v(-14.9, 19.61) * mm});
            skLineSegment(sketch, "E243.0.1.83", {"start": v(-8.75, 32.42) * mm, "end": v(-9.98, 32.48) * mm});
            skLineSegment(sketch, "E243.0.1.84", {"start": v(13.04, 19.25) * mm, "end": v(13.83, 20) * mm});
            skLineSegment(sketch, "E243.0.1.85", {"start": v(-10.6, 29.35) * mm, "end": v(-9.3, 29.42) * mm});
            skLineSegment(sketch, "E243.0.1.86", {"start": v(-6.39, 31.69) * mm, "end": v(-7.55, 32.15) * mm});
            skLineSegment(sketch, "E243.0.1.87", {"start": v(0.97, 23.5) * mm, "end": v(1.24, 22.5) * mm});
            skLineSegment(sketch, "E243.0.1.88", {"start": v(10.76, 21.33) * mm, "end": v(10.01, 20.92) * mm});
            skLineSegment(sketch, "E243.0.1.89", {"start": v(3.85, 19) * mm, "end": v(4.78, 18.4) * mm});
            skLineSegment(sketch, "E243.0.1.90", {"start": v(13.83, 20) * mm, "end": v(14.5, 20.86) * mm});
            skLineSegment(sketch, "E243.0.1.91", {"start": v(-12.87, 28.14) * mm, "end": v(-12.64, 28.37) * mm});
            skLineSegment(sketch, "E243.0.1.92", {"start": v(-29.17, 32.47) * mm, "end": v(-29.17, 30.52) * mm});
            skLineSegment(sketch, "E243.0.1.93", {"start": v(-13.85, 26.5) * mm, "end": v(-13.65, 27.08) * mm});
            skLineSegment(sketch, "E243.0.1.94", {"start": v(4.92, 27.91) * mm, "end": v(5.15, 28.14) * mm});
            skLineSegment(sketch, "E243.0.1.95", {"start": v(-12.38, 32) * mm, "end": v(-13.51, 31.45) * mm});
            skLineSegment(sketch, "E243.0.1.96", {"start": v(-12.88, 18.23) * mm, "end": v(-11.73, 17.8) * mm});
            skLineSegment(sketch, "E243.0.1.97", {"start": v(-19.83, 18.07) * mm, "end": v(-20.4, 17.68) * mm});
            skLineSegment(sketch, "E243.0.1.98", {"start": v(29.1, 35.38) * mm, "end": v(28.72, 35.96) * mm});
            skLineSegment(sketch, "E243.0.1.99", {"start": v(11.4, 18.21) * mm, "end": v(12.14, 18.6) * mm});
            skLineSegment(sketch, "E243.0.1.100", {"start": v(-27.12, 32.1) * mm, "end": v(-26.39, 32.35) * mm});
            skLineSegment(sketch, "E243.0.1.101", {"start": v(6.2, 28.92) * mm, "end": v(7.42, 29.36) * mm});
            skLineSegment(sketch, "E243.0.1.102", {"start": v(7.9, 17.54) * mm, "end": v(9, 17.57) * mm});
            skLineSegment(sketch, "E243.0.1.103", {"start": v(-29.1, 30.65) * mm, "end": v(-28.84, 31) * mm});
            skLineSegment(sketch, "E243.0.1.104", {"start": v(-28.37, 31.44) * mm, "end": v(-27.79, 31.8) * mm});
            skLineSegment(sketch, "E243.0.1.105", {"start": v(-7.7, 17.81) * mm, "end": v(-6.79, 18.14) * mm});
            skLineSegment(sketch, "E243.0.1.106", {"start": v(7.17, 32.4) * mm, "end": v(6.1, 32.15) * mm});
            skLineSegment(sketch, "E243.0.1.107", {"start": v(-19.83, 20.63) * mm, "end": v(-19.44, 20.06) * mm});
            skLineSegment(sketch, "E243.0.1.108", {"start": v(4.16, 26.5) * mm, "end": v(4.37, 27.09) * mm});
            skLineSegment(sketch, "E243.0.1.109", {"start": v(-11.73, 17.8) * mm, "end": v(-10.51, 17.58) * mm});
            skLineSegment(sketch, "E243.0.1.110", {"start": v(-7.73, 28.98) * mm, "end": v(-6.9, 28.42) * mm});
            skLineSegment(sketch, "E243.0.1.111", {"start": v(12.14, 18.6) * mm, "end": v(13.04, 19.25) * mm});
            skLineSegment(sketch, "E243.0.1.112", {"start": v(1.03, 26.8) * mm, "end": v(0.98, 26.5) * mm});
            skLineSegment(sketch, "E243.0.1.113", {"start": v(31.67, 35.38) * mm, "end": v(31.1, 35) * mm});
            skLineSegment(sketch, "E243.0.1.114", {"start": v(-26.13, 29.06) * mm, "end": v(-27, 28.65) * mm});
            skLineSegment(sketch, "E243.0.1.115", {"start": v(-27.79, 31.8) * mm, "end": v(-27.12, 32.1) * mm});
            skLineSegment(sketch, "E243.0.1.116", {"start": v(-5.68, 18.73) * mm, "end": v(-4.7, 19.48) * mm});
            skLineSegment(sketch, "E243.0.1.117", {"start": v(11.2, 31.9) * mm, "end": v(9.8, 32.33) * mm});
            skLineSegment(sketch, "E243.0.1.118", {"start": v(-11.8, 28.92) * mm, "end": v(-10.6, 29.35) * mm});
            skLineSegment(sketch, "E243.0.1.119", {"start": v(-17.02, 23.5) * mm, "end": v(-16.88, 22.82) * mm});
            skLineSegment(sketch, "E243.0.1.120", {"start": v(8.7, 29.42) * mm, "end": v(9.68, 29.23) * mm});
            skLineSegment(sketch, "E243.0.1.121", {"start": v(10.89, 18) * mm, "end": v(11.14, 18.1) * mm});
            skLineSegment(sketch, "E243.0.1.122", {"start": v(9.68, 29.23) * mm, "end": v(9.98, 29.1) * mm});
            skLineSegment(sketch, "E243.0.1.123", {"start": v(12.46, 31.2) * mm, "end": v(11.2, 31.9) * mm});
            skLineSegment(sketch, "E243.0.1.124", {"start": v(13.57, 30.3) * mm, "end": v(12.46, 31.2) * mm});
            skLineSegment(sketch, "E243.0.1.125", {"start": v(-13.65, 27.08) * mm, "end": v(-13.1, 27.9) * mm});
            skLineSegment(sketch, "E243.0.1.126", {"start": v(-16.18, 28.79) * mm, "end": v(-16.71, 27.68) * mm});
            skLineSegment(sketch, "E243.0.1.127", {"start": v(-8, 20.92) * mm, "end": v(-8.84, 20.66) * mm});
            skLineSegment(sketch, "E243.0.1.128", {"start": v(-28.84, 31) * mm, "end": v(-28.37, 31.44) * mm});
            skLineSegment(sketch, "E243.0.1.129", {"start": v(4.37, 27.09) * mm, "end": v(4.92, 27.91) * mm});
            skLineSegment(sketch, "E243.0.1.130", {"start": v(-15.46, 29.81) * mm, "end": v(-16.18, 28.79) * mm});
            skLineSegment(sketch, "E243.0.1.131", {"start": v(11.96, 22.53) * mm, "end": v(11.42, 21.87) * mm});
            skLineSegment(sketch, "E243.0.1.132", {"start": v(-9.98, 32.48) * mm, "end": v(-11.2, 32.33) * mm});
            skLineSegment(sketch, "E243.0.1.133", {"start": v(-13.94, 18.84) * mm, "end": v(-12.88, 18.23) * mm});
            skLineSegment(sketch, "E243.0.1.134", {"start": v(-11.2, 32.33) * mm, "end": v(-12.38, 32) * mm});
            skLineSegment(sketch, "E243.0.1.135", {"start": v(11.1, 28.43) * mm, "end": v(11.97, 27.47) * mm});
            skLineSegment(sketch, "E243.0.1.136", {"start": v(-13.1, 27.9) * mm, "end": v(-12.87, 28.14) * mm});
            skLineSegment(sketch, "E243.0.1.137", {"start": v(-13.7, 23) * mm, "end": v(-13.83, 23.3) * mm});
            skLineSegment(sketch, "E243.0.1.138", {"start": v(2.52, 29.77) * mm, "end": v(1.89, 28.87) * mm});
            skLineSegment(sketch, "E243.0.1.139", {"start": v(15.43, 22.82) * mm, "end": v(15.58, 23.5) * mm});
            skLineSegment(sketch, "E243.0.1.140", {"start": v(-12.2, 21.32) * mm, "end": v(-13.15, 22.18) * mm});
            skLineSegment(sketch, "E243.0.1.141", {"start": v(-14.9, 19.61) * mm, "end": v(-13.94, 18.84) * mm});
            skLineSegment(sketch, "E243.0.1.142", {"start": v(-28.34, 27.31) * mm, "end": v(-28.8, 26.38) * mm});
            skLineSegment(sketch, "E243.0.1.143", {"start": v(28.72, 37.37) * mm, "end": v(29.1, 37.95) * mm});
            skLineSegment(sketch, "E243.0.1.144", {"start": v(15.6, 26.51) * mm, "end": v(15.17, 27.92) * mm});
            skLineSegment(sketch, "E243.0.1.145", {"start": v(-22.79, 20.06) * mm, "end": v(-22.4, 20.63) * mm});
            skLineSegment(sketch, "E243.0.1.146", {"start": v(29.68, 35) * mm, "end": v(29.1, 35.38) * mm});
            skLineSegment(sketch, "E243.0.1.147", {"start": v(1.28, 27.6) * mm, "end": v(1.03, 26.8) * mm});
            skLineSegment(sketch, "E243.0.1.148", {"start": v(-19.44, 18.64) * mm, "end": v(-19.83, 18.07) * mm});
            skLineSegment(sketch, "E243.0.1.149", {"start": v(-20.4, 21.02) * mm, "end": v(-19.83, 20.63) * mm});
            skLineSegment(sketch, "E243.0.1.150", {"start": v(31.1, 38.34) * mm, "end": v(31.67, 37.95) * mm});
            skLineSegment(sketch, "E243.0.1.151", {"start": v(-25.62, 32.52) * mm, "end": v(-24.84, 32.63) * mm});
            skLineSegment(sketch, "E243.0.1.152", {"start": v(32.06, 35.96) * mm, "end": v(31.67, 35.38) * mm});
            skLineSegment(sketch, "E243.0.1.153", {"start": v(-25.16, 29.3) * mm, "end": v(-26.13, 29.06) * mm});
            skLineSegment(sketch, "E243.0.1.154", {"start": v(-21.82, 17.68) * mm, "end": v(-22.4, 18.07) * mm});
            skLineSegment(sketch, "E243.0.1.155", {"start": v(3.2, 19.53) * mm, "end": v(3.85, 19) * mm});
            skLineSegment(sketch, "E243.0.1.156", {"start": v(-23.33, 32.61) * mm, "end": v(-22.8, 32.48) * mm});
            skLineSegment(sketch, "E243.0.1.157", {"start": v(8.29, 32.48) * mm, "end": v(8, 32.48) * mm});
            skLineSegment(sketch, "E243.0.1.158", {"start": v(-10.06, 20.57) * mm, "end": v(-11.03, 20.76) * mm});
            skLineSegment(sketch, "E243.0.1.159", {"start": v(8.66, 32.48) * mm, "end": v(8.29, 32.48) * mm});
            skLineSegment(sketch, "E243.0.1.160", {"start": v(29.68, 38.34) * mm, "end": v(30.21, 38.48) * mm});
            skLineSegment(sketch, "E243.0.1.161", {"start": v(8.5, 20.57) * mm, "end": v(8.29, 20.57) * mm});
            skLineSegment(sketch, "E243.0.1.162", {"start": v(1.89, 28.87) * mm, "end": v(1.49, 28.13) * mm});
            skLineSegment(sketch, "E243.0.1.163", {"start": v(-24.08, 32.66) * mm, "end": v(-23.9, 32.66) * mm});
            skLineSegment(sketch, "E243.0.1.164", {"start": v(-19.3, 19.53) * mm, "end": v(-19.3, 19.35) * mm});
            skLineSegment(sketch, "E243.0.1.165", {"start": v(2.8, 19.92) * mm, "end": v(3, 19.72) * mm});
            skLineSegment(sketch, "E243.0.1.166", {"start": v(30.21, 34.85) * mm, "end": v(29.68, 35) * mm});
            skLineSegment(sketch, "E243.0.1.167", {"start": v(-23.38, 29.35) * mm, "end": v(-23.96, 29.39) * mm});
            skLineSegment(sketch, "E243.0.1.168", {"start": v(-19.44, 20.06) * mm, "end": v(-19.3, 19.53) * mm});
            skLineSegment(sketch, "E243.0.1.169", {"start": v(30.21, 38.48) * mm, "end": v(30.39, 38.48) * mm});
            skLineSegment(sketch, "E243.0.1.170", {"start": v(9.18, 20.66) * mm, "end": v(8.5, 20.57) * mm});
            skLineSegment(sketch, "E243.0.1.171", {"start": v(-9.26, 17.55) * mm, "end": v(-8.3, 17.66) * mm});
            skLineSegment(sketch, "E243.0.1.172", {"start": v(-22.8, 32.48) * mm, "end": v(-22.7, 32.44) * mm});
            skLineSegment(sketch, "E243.0.1.173", {"start": v(-5.58, 23.5) * mm, "end": v(-5.65, 23.28) * mm});
            skLineSegment(sketch, "E243.0.1.174", {"start": v(-14.31, 30.92) * mm, "end": v(-14.55, 30.71) * mm});
            skLineSegment(sketch, "E243.0.1.175", {"start": v(-23.9, 32.66) * mm, "end": v(-23.33, 32.61) * mm});
            skLineSegment(sketch, "E243.0.1.176", {"start": v(-24.84, 32.63) * mm, "end": v(-24.27, 32.66) * mm});
            skLineSegment(sketch, "E243.0.1.177", {"start": v(-24.27, 32.66) * mm, "end": v(-24.08, 32.66) * mm});
            skLineSegment(sketch, "E243.0.1.178", {"start": v(-29.07, 25.26) * mm, "end": v(-29.17, 24.28) * mm});
            skLineSegment(sketch, "E243.0.1.179", {"start": v(30.57, 38.48) * mm, "end": v(31.1, 38.34) * mm});
            skLineSegment(sketch, "E243.0.1.180", {"start": v(7.96, 20.57) * mm, "end": v(6.99, 20.77) * mm});
            skLineSegment(sketch, "E243.0.1.181", {"start": v(-8.33, 29.22) * mm, "end": v(-8.03, 29.1) * mm});
            skLineSegment(sketch, "E243.0.1.182", {"start": v(-5.55, 31.21) * mm, "end": v(-6.39, 31.69) * mm});
            skLineSegment(sketch, "E243.0.1.183", {"start": v(-5.3, 31.02) * mm, "end": v(-5.55, 31.21) * mm});
            skLineSegment(sketch, "E243.0.1.184", {"start": v(-24.35, 29.39) * mm, "end": v(-25.16, 29.3) * mm});
            skLineSegment(sketch, "E243.0.1.185", {"start": v(30.39, 34.85) * mm, "end": v(30.21, 34.85) * mm});
            skLineSegment(sketch, "E243.0.1.186", {"start": v(30.57, 34.85) * mm, "end": v(30.39, 34.85) * mm});
            skLineSegment(sketch, "E243.0.1.187", {"start": v(4.19, 23.31) * mm, "end": v(4.11, 23.5) * mm});
            skLineSegment(sketch, "E243.0.1.188", {"start": v(-13.51, 31.45) * mm, "end": v(-14.31, 30.92) * mm});
            skLineSegment(sketch, "E243.0.1.189", {"start": v(-19.3, 19.35) * mm, "end": v(-19.3, 19.17) * mm});
            skLineSegment(sketch, "E243.0.1.190", {"start": v(-16.4, 21.64) * mm, "end": v(-16.26, 21.35) * mm});
            skLineSegment(sketch, "E243.0.1.191", {"start": v(-22.93, 19.17) * mm, "end": v(-22.93, 19.35) * mm});
            skLineSegment(sketch, "E243.0.1.192", {"start": v(-8.3, 17.66) * mm, "end": v(-8, 17.74) * mm});
            skLineSegment(sketch, "E243.0.1.193", {"start": v(8, 32.48) * mm, "end": v(7.17, 32.4) * mm});
            skLineSegment(sketch, "E243.0.1.194", {"start": v(-16.54, 21.92) * mm, "end": v(-16.4, 21.64) * mm});
            skLineSegment(sketch, "E243.0.1.195", {"start": v(-22.93, 19.53) * mm, "end": v(-22.79, 20.06) * mm});
            skLineSegment(sketch, "E243.0.1.196", {"start": v(1.38, 27.87) * mm, "end": v(1.28, 27.6) * mm});
            skLineSegment(sketch, "E243.0.1.197", {"start": v(-29.17, 24.28) * mm, "end": v(-29.17, 23.96) * mm});
            skLineSegment(sketch, "E243.0.1.198", {"start": v(15.6, 26.5) * mm, "end": v(15.6, 26.51) * mm});
            skLineSegment(sketch, "E243.0.1.199", {"start": v(-8, 17.74) * mm, "end": v(-7.7, 17.81) * mm});
            skLineSegment(sketch, "E243.0.1.200", {"start": v(-22.79, 18.64) * mm, "end": v(-22.93, 19.17) * mm});
            skLineSegment(sketch, "E243.0.1.201", {"start": v(-14.8, 30.5) * mm, "end": v(-15.46, 29.81) * mm});
            skLineSegment(sketch, "E243.0.1.202", {"start": v(12.37, 23.28) * mm, "end": v(11.96, 22.53) * mm});
            skLineSegment(sketch, "E243.0.1.203", {"start": v(4.87, 22.18) * mm, "end": v(4.31, 23.01) * mm});
            skLineSegment(sketch, "E243.0.1.204", {"start": v(-8.03, 29.1) * mm, "end": v(-7.73, 28.98) * mm});
            skLineSegment(sketch, "E243.0.1.205", {"start": v(30.39, 38.48) * mm, "end": v(30.57, 38.48) * mm});
            skLineSegment(sketch, "E243.0.1.206", {"start": v(-9.3, 29.42) * mm, "end": v(-8.33, 29.22) * mm});
            skLineSegment(sketch, "E243.0.1.207", {"start": v(8.29, 20.57) * mm, "end": v(7.96, 20.57) * mm});
            skLineSegment(sketch, "E243.0.1.208", {"start": v(-16.88, 22.82) * mm, "end": v(-16.54, 21.92) * mm});
            skLineSegment(sketch, "E243.0.1.209", {"start": v(1.49, 28.13) * mm, "end": v(1.38, 27.87) * mm});
            skLineSegment(sketch, "E243.0.1.210", {"start": v(-23.96, 29.39) * mm, "end": v(-24.08, 29.39) * mm});
            skLineSegment(sketch, "E243.0.1.211", {"start": v(31.1, 35) * mm, "end": v(30.57, 34.85) * mm});
            skLineSegment(sketch, "E243.0.1.212", {"start": v(-5.65, 23.28) * mm, "end": v(-6.06, 22.53) * mm});
            skLineSegment(sketch, "E243.0.1.213", {"start": v(-22.81, 29.25) * mm, "end": v(-23.38, 29.35) * mm});
            skLineSegment(sketch, "E243.0.1.214", {"start": v(4.31, 23.01) * mm, "end": v(4.19, 23.31) * mm});
            skLineSegment(sketch, "E243.0.1.215", {"start": v(2.27, 20.57) * mm, "end": v(2.8, 19.92) * mm});
            skLineSegment(sketch, "E243.0.1.216", {"start": v(-19.3, 19.17) * mm, "end": v(-19.44, 18.64) * mm});
            skLineSegment(sketch, "E243.0.1.217", {"start": v(12.44, 23.5) * mm, "end": v(12.37, 23.28) * mm});
            skLineSegment(sketch, "E243.0.1.218", {"start": v(3, 19.72) * mm, "end": v(3.2, 19.53) * mm});
            skLineSegment(sketch, "E243.0.1.219", {"start": v(-22.93, 19.35) * mm, "end": v(-22.93, 19.53) * mm});
            skLineSegment(sketch, "E243.0.1.220", {"start": v(-14.55, 30.71) * mm, "end": v(-14.8, 30.5) * mm});
            skLineSegment(sketch, "E243.0.1.221", {"start": v(-22.7, 29.23) * mm, "end": v(-22.81, 29.25) * mm});
            skLineSegment(sketch, "E243.0.1.222", {"start": v(-24.08, 29.39) * mm, "end": v(-24.35, 29.39) * mm});
            skLineSegment(sketch, "E243.0.1.223", {"start": v(-8.84, 20.66) * mm, "end": v(-9.5, 20.57) * mm});
            skLineSegment(sketch, "E243.0.1.224", {"start": v(-21.82, 21.02) * mm, "end": v(-21.29, 21.17) * mm});
            skLineSegment(sketch, "E243.0.1.225", {"start": v(32.2, 36.49) * mm, "end": v(32.06, 35.96) * mm});
            skLineSegment(sketch, "E243.0.1.226", {"start": v(-21.29, 21.17) * mm, "end": v(-21.11, 21.17) * mm});
            skLineSegment(sketch, "E243.0.1.227", {"start": v(-21.29, 17.53) * mm, "end": v(-21.82, 17.68) * mm});
            skLineSegment(sketch, "E243.0.1.228", {"start": v(-20.4, 17.68) * mm, "end": v(-20.94, 17.53) * mm});
            skLineSegment(sketch, "E243.0.1.229", {"start": v(-9.73, 20.57) * mm, "end": v(-9.73, 20.57) * mm});
            skLineSegment(sketch, "E243.0.1.230", {"start": v(28.57, 36.84) * mm, "end": v(28.72, 37.37) * mm});
            skLineSegment(sketch, "E243.0.1.231", {"start": v(-9.5, 20.57) * mm, "end": v(-9.73, 20.57) * mm});
            skLineSegment(sketch, "E243.0.1.232", {"start": v(-20.94, 21.17) * mm, "end": v(-20.4, 21.02) * mm});
            skLineSegment(sketch, "E243.0.1.233", {"start": v(28.57, 36.66) * mm, "end": v(28.57, 36.84) * mm});
            skLineSegment(sketch, "E243.0.1.234", {"start": v(28.72, 35.96) * mm, "end": v(28.57, 36.49) * mm});
            skLineSegment(sketch, "E243.0.1.235", {"start": v(32.2, 36.84) * mm, "end": v(32.2, 36.66) * mm});
            skLineSegment(sketch, "E243.0.1.236", {"start": v(-21.11, 17.53) * mm, "end": v(-21.29, 17.53) * mm});
            skLineSegment(sketch, "E243.0.1.237", {"start": v(32.06, 37.37) * mm, "end": v(32.2, 36.84) * mm});
            skLineSegment(sketch, "E243.0.1.238", {"start": v(-20.94, 17.53) * mm, "end": v(-21.11, 17.53) * mm});
            skLineSegment(sketch, "E243.0.1.239", {"start": v(-21.11, 21.17) * mm, "end": v(-20.94, 21.17) * mm});
            skLineSegment(sketch, "E243.0.1.240", {"start": v(-9.73, 20.57) * mm, "end": v(-10.06, 20.57) * mm});
            skLineSegment(sketch, "E243.0.1.241", {"start": v(28.57, 36.49) * mm, "end": v(28.57, 36.66) * mm});
            skLineSegment(sketch, "E243.0.1.242", {"start": v(32.2, 36.66) * mm, "end": v(32.2, 36.49) * mm});
            skLineSegment(sketch, "E243.0.2.0", {"start": v(19.98, 59.58) * mm, "end": v(19.98, 47.5) * mm});
            skLineSegment(sketch, "E243.0.2.1", {"start": v(19.98, 72.5) * mm, "end": v(19.98, 62.51) * mm});
            skLineSegment(sketch, "E243.0.2.2", {"start": v(-22.7, 62.44) * mm, "end": v(-22.7, 59.23) * mm});
            skLineSegment(sketch, "E243.0.2.3", {"start": v(26.4, 59.58) * mm, "end": v(26.4, 62.44) * mm});
            skLineSegment(sketch, "E243.0.2.4", {"start": v(26.4, 62.44) * mm, "end": v(23.05, 62.44) * mm});
            skLineSegment(sketch, "E243.0.2.5", {"start": v(12.43, 56.5) * mm, "end": v(15.6, 56.5) * mm});
            skLineSegment(sketch, "E243.0.2.6", {"start": v(-17.05, 56.5) * mm, "end": v(-13.85, 56.5) * mm});
            skLineSegment(sketch, "E243.0.2.7", {"start": v(-32.2, 47.5) * mm, "end": v(-32.2, 62.47) * mm});
            skLineSegment(sketch, "E243.0.2.8", {"start": v(-29.17, 53.96) * mm, "end": v(-29.17, 47.5) * mm});
            skLineSegment(sketch, "E243.0.2.9", {"start": v(0.98, 56.5) * mm, "end": v(4.16, 56.5) * mm});
            skLineSegment(sketch, "E243.0.2.10", {"start": v(0.97, 53.5) * mm, "end": v(4.11, 53.5) * mm});
            skLineSegment(sketch, "E243.0.2.11", {"start": v(12.44, 53.5) * mm, "end": v(15.58, 53.5) * mm});
            skLineSegment(sketch, "E243.0.2.12", {"start": v(-5.3, 72.5) * mm, "end": v(-5.3, 61.02) * mm});
            skLineSegment(sketch, "E243.0.2.13", {"start": v(23.05, 47.5) * mm, "end": v(23.05, 59.58) * mm});
            skLineSegment(sketch, "E243.0.2.14", {"start": v(-32.2, 62.47) * mm, "end": v(-29.17, 62.47) * mm});
            skLineSegment(sketch, "E243.0.2.15", {"start": v(-29.17, 47.5) * mm, "end": v(-32.2, 47.5) * mm});
            skLineSegment(sketch, "E243.0.2.16", {"start": v(17.6, 62.51) * mm, "end": v(17.6, 59.58) * mm});
            skLineSegment(sketch, "E243.0.2.17", {"start": v(-2.26, 56.5) * mm, "end": v(-2.22, 72.5) * mm});
            skLineSegment(sketch, "E243.0.2.18", {"start": v(-2.22, 72.5) * mm, "end": v(-5.3, 72.5) * mm});
            skLineSegment(sketch, "E243.0.2.19", {"start": v(19.98, 47.5) * mm, "end": v(23.05, 47.5) * mm});
            skLineSegment(sketch, "E243.0.2.20", {"start": v(-5.58, 53.5) * mm, "end": v(-2.43, 53.5) * mm});
            skLineSegment(sketch, "E243.0.2.21", {"start": v(-17.02, 53.5) * mm, "end": v(-13.9, 53.5) * mm});
            skLineSegment(sketch, "E243.0.2.22", {"start": v(23.05, 72.5) * mm, "end": v(19.98, 72.5) * mm});
            skLineSegment(sketch, "E243.0.2.23", {"start": v(23.05, 62.44) * mm, "end": v(23.05, 72.5) * mm});
            skLineSegment(sketch, "E243.0.2.24", {"start": v(-5.58, 56.5) * mm, "end": v(-2.26, 56.5) * mm});
            skLineSegment(sketch, "E243.0.2.25", {"start": v(23.05, 59.58) * mm, "end": v(26.4, 59.58) * mm});
            skLineSegment(sketch, "E243.0.2.26", {"start": v(-4.7, 49.48) * mm, "end": v(-3.87, 50.38) * mm});
            skLineSegment(sketch, "E243.0.2.27", {"start": v(-16.71, 57.68) * mm, "end": v(-17.05, 56.5) * mm});
            skLineSegment(sketch, "E243.0.2.28", {"start": v(29.1, 67.95) * mm, "end": v(29.68, 68.34) * mm});
            skLineSegment(sketch, "E243.0.2.29", {"start": v(-13.83, 53.3) * mm, "end": v(-13.95, 53.6) * mm});
            skLineSegment(sketch, "E243.0.2.30", {"start": v(5.82, 51.32) * mm, "end": v(4.87, 52.18) * mm});
            skLineSegment(sketch, "E243.0.2.31", {"start": v(-3.19, 51.4) * mm, "end": v(-2.68, 52.52) * mm});
            skLineSegment(sketch, "E243.0.2.32", {"start": v(17.6, 59.58) * mm, "end": v(19.98, 59.58) * mm});
            skLineSegment(sketch, "E243.0.2.33", {"start": v(-6.79, 48.14) * mm, "end": v(-5.68, 48.73) * mm});
            skLineSegment(sketch, "E243.0.2.34", {"start": v(7.42, 59.36) * mm, "end": v(8.7, 59.42) * mm});
            skLineSegment(sketch, "E243.0.2.35", {"start": v(4.78, 48.4) * mm, "end": v(5.78, 47.97) * mm});
            skLineSegment(sketch, "E243.0.2.36", {"start": v(-6.06, 52.53) * mm, "end": v(-6.6, 51.87) * mm});
            skLineSegment(sketch, "E243.0.2.37", {"start": v(15.17, 57.92) * mm, "end": v(14.48, 59.18) * mm});
            skLineSegment(sketch, "E243.0.2.38", {"start": v(14.5, 50.86) * mm, "end": v(15.03, 51.8) * mm});
            skLineSegment(sketch, "E243.0.2.39", {"start": v(1.68, 51.5) * mm, "end": v(2.27, 50.57) * mm});
            skLineSegment(sketch, "E243.0.2.40", {"start": v(-27.74, 58.07) * mm, "end": v(-28.34, 57.31) * mm});
            skLineSegment(sketch, "E243.0.2.41", {"start": v(-27, 58.65) * mm, "end": v(-27.74, 58.07) * mm});
            skLineSegment(sketch, "E243.0.2.42", {"start": v(-3.87, 50.38) * mm, "end": v(-3.19, 51.4) * mm});
            skLineSegment(sketch, "E243.0.2.43", {"start": v(9.8, 62.33) * mm, "end": v(8.66, 62.48) * mm});
            skLineSegment(sketch, "E243.0.2.44", {"start": v(-2.68, 52.52) * mm, "end": v(-2.43, 53.5) * mm});
            skLineSegment(sketch, "E243.0.2.45", {"start": v(-6.6, 51.87) * mm, "end": v(-7.25, 51.33) * mm});
            skLineSegment(sketch, "E243.0.2.46", {"start": v(14.48, 59.18) * mm, "end": v(13.57, 60.3) * mm});
            skLineSegment(sketch, "E243.0.2.47", {"start": v(19.98, 62.51) * mm, "end": v(17.6, 62.51) * mm});
            skLineSegment(sketch, "E243.0.2.48", {"start": v(-11.03, 50.76) * mm, "end": v(-12.2, 51.32) * mm});
            skLineSegment(sketch, "E243.0.2.49", {"start": v(31.67, 67.95) * mm, "end": v(32.06, 67.37) * mm});
            skLineSegment(sketch, "E243.0.2.50", {"start": v(6.99, 50.77) * mm, "end": v(5.82, 51.32) * mm});
            skLineSegment(sketch, "E243.0.2.51", {"start": v(1.24, 52.5) * mm, "end": v(1.68, 51.5) * mm});
            skLineSegment(sketch, "E243.0.2.52", {"start": v(-26.39, 62.35) * mm, "end": v(-25.62, 62.52) * mm});
            skLineSegment(sketch, "E243.0.2.53", {"start": v(11.14, 48.1) * mm, "end": v(11.4, 48.21) * mm});
            skLineSegment(sketch, "E243.0.2.54", {"start": v(5.15, 58.14) * mm, "end": v(5.38, 58.37) * mm});
            skLineSegment(sketch, "E243.0.2.55", {"start": v(-12.64, 58.37) * mm, "end": v(-11.8, 58.92) * mm});
            skLineSegment(sketch, "E243.0.2.56", {"start": v(-16.26, 51.35) * mm, "end": v(-15.73, 50.55) * mm});
            skLineSegment(sketch, "E243.0.2.57", {"start": v(-29.17, 60.52) * mm, "end": v(-29.1, 60.65) * mm});
            skLineSegment(sketch, "E243.0.2.58", {"start": v(10.01, 50.92) * mm, "end": v(9.18, 50.66) * mm});
            skLineSegment(sketch, "E243.0.2.59", {"start": v(3.28, 60.55) * mm, "end": v(2.52, 59.77) * mm});
            skLineSegment(sketch, "E243.0.2.60", {"start": v(5.78, 47.97) * mm, "end": v(6.83, 47.68) * mm});
            skLineSegment(sketch, "E243.0.2.61", {"start": v(15.03, 51.8) * mm, "end": v(15.43, 52.82) * mm});
            skLineSegment(sketch, "E243.0.2.62", {"start": v(-13.15, 52.18) * mm, "end": v(-13.7, 53) * mm});
            skLineSegment(sketch, "E243.0.2.63", {"start": v(11.42, 51.87) * mm, "end": v(10.76, 51.33) * mm});
            skLineSegment(sketch, "E243.0.2.64", {"start": v(-10.51, 47.58) * mm, "end": v(-9.26, 47.55) * mm});
            skLineSegment(sketch, "E243.0.2.65", {"start": v(11.97, 57.47) * mm, "end": v(12.43, 56.5) * mm});
            skLineSegment(sketch, "E243.0.2.66", {"start": v(-28.8, 56.38) * mm, "end": v(-29.07, 55.26) * mm});
            skLineSegment(sketch, "E243.0.2.67", {"start": v(10.28, 58.98) * mm, "end": v(11.1, 58.43) * mm});
            skLineSegment(sketch, "E243.0.2.68", {"start": v(9.98, 59.1) * mm, "end": v(10.28, 58.98) * mm});
            skLineSegment(sketch, "E243.0.2.69", {"start": v(-22.4, 50.63) * mm, "end": v(-21.82, 51.02) * mm});
            skLineSegment(sketch, "E243.0.2.70", {"start": v(-7.55, 62.15) * mm, "end": v(-8.75, 62.42) * mm});
            skLineSegment(sketch, "E243.0.2.71", {"start": v(10.08, 47.75) * mm, "end": v(10.89, 48) * mm});
            skLineSegment(sketch, "E243.0.2.72", {"start": v(9, 47.57) * mm, "end": v(10.08, 47.75) * mm});
            skLineSegment(sketch, "E243.0.2.73", {"start": v(-7.25, 51.33) * mm, "end": v(-8, 50.92) * mm});
            skLineSegment(sketch, "E243.0.2.74", {"start": v(5.38, 58.37) * mm, "end": v(6.2, 58.92) * mm});
            skLineSegment(sketch, "E243.0.2.75", {"start": v(4.13, 61.22) * mm, "end": v(3.28, 60.55) * mm});
            skLineSegment(sketch, "E243.0.2.76", {"start": v(6.83, 47.68) * mm, "end": v(7.9, 47.54) * mm});
            skLineSegment(sketch, "E243.0.2.77", {"start": v(-22.4, 48.07) * mm, "end": v(-22.79, 48.64) * mm});
            skLineSegment(sketch, "E243.0.2.78", {"start": v(6.1, 62.15) * mm, "end": v(5.08, 61.76) * mm});
            skLineSegment(sketch, "E243.0.2.79", {"start": v(-6.9, 58.42) * mm, "end": v(-6.04, 57.47) * mm});
            skLineSegment(sketch, "E243.0.2.80", {"start": v(5.08, 61.76) * mm, "end": v(4.13, 61.22) * mm});
            skLineSegment(sketch, "E243.0.2.81", {"start": v(-6.04, 57.47) * mm, "end": v(-5.58, 56.5) * mm});
            skLineSegment(sketch, "E243.0.2.82", {"start": v(-15.73, 50.55) * mm, "end": v(-14.9, 49.61) * mm});
            skLineSegment(sketch, "E243.0.2.83", {"start": v(-8.75, 62.42) * mm, "end": v(-9.98, 62.48) * mm});
            skLineSegment(sketch, "E243.0.2.84", {"start": v(13.04, 49.25) * mm, "end": v(13.83, 50) * mm});
            skLineSegment(sketch, "E243.0.2.85", {"start": v(-10.6, 59.35) * mm, "end": v(-9.3, 59.42) * mm});
            skLineSegment(sketch, "E243.0.2.86", {"start": v(-6.39, 61.69) * mm, "end": v(-7.55, 62.15) * mm});
            skLineSegment(sketch, "E243.0.2.87", {"start": v(0.97, 53.5) * mm, "end": v(1.24, 52.5) * mm});
            skLineSegment(sketch, "E243.0.2.88", {"start": v(10.76, 51.33) * mm, "end": v(10.01, 50.92) * mm});
            skLineSegment(sketch, "E243.0.2.89", {"start": v(3.85, 49) * mm, "end": v(4.78, 48.4) * mm});
            skLineSegment(sketch, "E243.0.2.90", {"start": v(13.83, 50) * mm, "end": v(14.5, 50.86) * mm});
            skLineSegment(sketch, "E243.0.2.91", {"start": v(-12.87, 58.14) * mm, "end": v(-12.64, 58.37) * mm});
            skLineSegment(sketch, "E243.0.2.92", {"start": v(-29.17, 62.47) * mm, "end": v(-29.17, 60.52) * mm});
            skLineSegment(sketch, "E243.0.2.93", {"start": v(-13.85, 56.5) * mm, "end": v(-13.65, 57.08) * mm});
            skLineSegment(sketch, "E243.0.2.94", {"start": v(4.92, 57.91) * mm, "end": v(5.15, 58.14) * mm});
            skLineSegment(sketch, "E243.0.2.95", {"start": v(-12.38, 62) * mm, "end": v(-13.51, 61.45) * mm});
            skLineSegment(sketch, "E243.0.2.96", {"start": v(-12.88, 48.23) * mm, "end": v(-11.73, 47.8) * mm});
            skLineSegment(sketch, "E243.0.2.97", {"start": v(-19.83, 48.07) * mm, "end": v(-20.4, 47.68) * mm});
            skLineSegment(sketch, "E243.0.2.98", {"start": v(29.1, 65.38) * mm, "end": v(28.72, 65.96) * mm});
            skLineSegment(sketch, "E243.0.2.99", {"start": v(11.4, 48.21) * mm, "end": v(12.14, 48.6) * mm});
            skLineSegment(sketch, "E243.0.2.100", {"start": v(-27.12, 62.1) * mm, "end": v(-26.39, 62.35) * mm});
            skLineSegment(sketch, "E243.0.2.101", {"start": v(6.2, 58.92) * mm, "end": v(7.42, 59.36) * mm});
            skLineSegment(sketch, "E243.0.2.102", {"start": v(7.9, 47.54) * mm, "end": v(9, 47.57) * mm});
            skLineSegment(sketch, "E243.0.2.103", {"start": v(-29.1, 60.65) * mm, "end": v(-28.84, 61) * mm});
            skLineSegment(sketch, "E243.0.2.104", {"start": v(-28.37, 61.44) * mm, "end": v(-27.79, 61.8) * mm});
            skLineSegment(sketch, "E243.0.2.105", {"start": v(-7.7, 47.81) * mm, "end": v(-6.79, 48.14) * mm});
            skLineSegment(sketch, "E243.0.2.106", {"start": v(7.17, 62.4) * mm, "end": v(6.1, 62.15) * mm});
            skLineSegment(sketch, "E243.0.2.107", {"start": v(-19.83, 50.63) * mm, "end": v(-19.44, 50.06) * mm});
            skLineSegment(sketch, "E243.0.2.108", {"start": v(4.16, 56.5) * mm, "end": v(4.37, 57.09) * mm});
            skLineSegment(sketch, "E243.0.2.109", {"start": v(-11.73, 47.8) * mm, "end": v(-10.51, 47.58) * mm});
            skLineSegment(sketch, "E243.0.2.110", {"start": v(-7.73, 58.98) * mm, "end": v(-6.9, 58.42) * mm});
            skLineSegment(sketch, "E243.0.2.111", {"start": v(12.14, 48.6) * mm, "end": v(13.04, 49.25) * mm});
            skLineSegment(sketch, "E243.0.2.112", {"start": v(1.03, 56.8) * mm, "end": v(0.98, 56.5) * mm});
            skLineSegment(sketch, "E243.0.2.113", {"start": v(31.67, 65.38) * mm, "end": v(31.1, 65) * mm});
            skLineSegment(sketch, "E243.0.2.114", {"start": v(-26.13, 59.06) * mm, "end": v(-27, 58.65) * mm});
            skLineSegment(sketch, "E243.0.2.115", {"start": v(-27.79, 61.8) * mm, "end": v(-27.12, 62.1) * mm});
            skLineSegment(sketch, "E243.0.2.116", {"start": v(-5.68, 48.73) * mm, "end": v(-4.7, 49.48) * mm});
            skLineSegment(sketch, "E243.0.2.117", {"start": v(11.2, 61.9) * mm, "end": v(9.8, 62.33) * mm});
            skLineSegment(sketch, "E243.0.2.118", {"start": v(-11.8, 58.92) * mm, "end": v(-10.6, 59.35) * mm});
            skLineSegment(sketch, "E243.0.2.119", {"start": v(-17.02, 53.5) * mm, "end": v(-16.88, 52.82) * mm});
            skLineSegment(sketch, "E243.0.2.120", {"start": v(8.7, 59.42) * mm, "end": v(9.68, 59.23) * mm});
            skLineSegment(sketch, "E243.0.2.121", {"start": v(10.89, 48) * mm, "end": v(11.14, 48.1) * mm});
            skLineSegment(sketch, "E243.0.2.122", {"start": v(9.68, 59.23) * mm, "end": v(9.98, 59.1) * mm});
            skLineSegment(sketch, "E243.0.2.123", {"start": v(12.46, 61.2) * mm, "end": v(11.2, 61.9) * mm});
            skLineSegment(sketch, "E243.0.2.124", {"start": v(13.57, 60.3) * mm, "end": v(12.46, 61.2) * mm});
            skLineSegment(sketch, "E243.0.2.125", {"start": v(-13.65, 57.08) * mm, "end": v(-13.1, 57.9) * mm});
            skLineSegment(sketch, "E243.0.2.126", {"start": v(-16.18, 58.79) * mm, "end": v(-16.71, 57.68) * mm});
            skLineSegment(sketch, "E243.0.2.127", {"start": v(-8, 50.92) * mm, "end": v(-8.84, 50.66) * mm});
            skLineSegment(sketch, "E243.0.2.128", {"start": v(-28.84, 61) * mm, "end": v(-28.37, 61.44) * mm});
            skLineSegment(sketch, "E243.0.2.129", {"start": v(4.37, 57.09) * mm, "end": v(4.92, 57.91) * mm});
            skLineSegment(sketch, "E243.0.2.130", {"start": v(-15.46, 59.81) * mm, "end": v(-16.18, 58.79) * mm});
            skLineSegment(sketch, "E243.0.2.131", {"start": v(11.96, 52.53) * mm, "end": v(11.42, 51.87) * mm});
            skLineSegment(sketch, "E243.0.2.132", {"start": v(-9.98, 62.48) * mm, "end": v(-11.2, 62.33) * mm});
            skLineSegment(sketch, "E243.0.2.133", {"start": v(-13.94, 48.84) * mm, "end": v(-12.88, 48.23) * mm});
            skLineSegment(sketch, "E243.0.2.134", {"start": v(-11.2, 62.33) * mm, "end": v(-12.38, 62) * mm});
            skLineSegment(sketch, "E243.0.2.135", {"start": v(11.1, 58.43) * mm, "end": v(11.97, 57.47) * mm});
            skLineSegment(sketch, "E243.0.2.136", {"start": v(-13.1, 57.9) * mm, "end": v(-12.87, 58.14) * mm});
            skLineSegment(sketch, "E243.0.2.137", {"start": v(-13.7, 53) * mm, "end": v(-13.83, 53.3) * mm});
            skLineSegment(sketch, "E243.0.2.138", {"start": v(2.52, 59.77) * mm, "end": v(1.89, 58.87) * mm});
            skLineSegment(sketch, "E243.0.2.139", {"start": v(15.43, 52.82) * mm, "end": v(15.58, 53.5) * mm});
            skLineSegment(sketch, "E243.0.2.140", {"start": v(-12.2, 51.32) * mm, "end": v(-13.15, 52.18) * mm});
            skLineSegment(sketch, "E243.0.2.141", {"start": v(-14.9, 49.61) * mm, "end": v(-13.94, 48.84) * mm});
            skLineSegment(sketch, "E243.0.2.142", {"start": v(-28.34, 57.31) * mm, "end": v(-28.8, 56.38) * mm});
            skLineSegment(sketch, "E243.0.2.143", {"start": v(28.72, 67.37) * mm, "end": v(29.1, 67.95) * mm});
            skLineSegment(sketch, "E243.0.2.144", {"start": v(15.6, 56.51) * mm, "end": v(15.17, 57.92) * mm});
            skLineSegment(sketch, "E243.0.2.145", {"start": v(-22.79, 50.06) * mm, "end": v(-22.4, 50.63) * mm});
            skLineSegment(sketch, "E243.0.2.146", {"start": v(29.68, 65) * mm, "end": v(29.1, 65.38) * mm});
            skLineSegment(sketch, "E243.0.2.147", {"start": v(1.28, 57.6) * mm, "end": v(1.03, 56.8) * mm});
            skLineSegment(sketch, "E243.0.2.148", {"start": v(-19.44, 48.64) * mm, "end": v(-19.83, 48.07) * mm});
            skLineSegment(sketch, "E243.0.2.149", {"start": v(-20.4, 51.02) * mm, "end": v(-19.83, 50.63) * mm});
            skLineSegment(sketch, "E243.0.2.150", {"start": v(31.1, 68.34) * mm, "end": v(31.67, 67.95) * mm});
            skLineSegment(sketch, "E243.0.2.151", {"start": v(-25.62, 62.52) * mm, "end": v(-24.84, 62.63) * mm});
            skLineSegment(sketch, "E243.0.2.152", {"start": v(32.06, 65.96) * mm, "end": v(31.67, 65.38) * mm});
            skLineSegment(sketch, "E243.0.2.153", {"start": v(-25.16, 59.3) * mm, "end": v(-26.13, 59.06) * mm});
            skLineSegment(sketch, "E243.0.2.154", {"start": v(-21.82, 47.68) * mm, "end": v(-22.4, 48.07) * mm});
            skLineSegment(sketch, "E243.0.2.155", {"start": v(3.2, 49.53) * mm, "end": v(3.85, 49) * mm});
            skLineSegment(sketch, "E243.0.2.156", {"start": v(-23.33, 62.61) * mm, "end": v(-22.8, 62.48) * mm});
            skLineSegment(sketch, "E243.0.2.157", {"start": v(8.29, 62.48) * mm, "end": v(8, 62.48) * mm});
            skLineSegment(sketch, "E243.0.2.158", {"start": v(-10.06, 50.57) * mm, "end": v(-11.03, 50.76) * mm});
            skLineSegment(sketch, "E243.0.2.159", {"start": v(8.66, 62.48) * mm, "end": v(8.29, 62.48) * mm});
            skLineSegment(sketch, "E243.0.2.160", {"start": v(29.68, 68.34) * mm, "end": v(30.21, 68.48) * mm});
            skLineSegment(sketch, "E243.0.2.161", {"start": v(8.5, 50.57) * mm, "end": v(8.29, 50.57) * mm});
            skLineSegment(sketch, "E243.0.2.162", {"start": v(1.89, 58.87) * mm, "end": v(1.49, 58.13) * mm});
            skLineSegment(sketch, "E243.0.2.163", {"start": v(-24.08, 62.66) * mm, "end": v(-23.9, 62.66) * mm});
            skLineSegment(sketch, "E243.0.2.164", {"start": v(-19.3, 49.53) * mm, "end": v(-19.3, 49.35) * mm});
            skLineSegment(sketch, "E243.0.2.165", {"start": v(2.8, 49.92) * mm, "end": v(3, 49.72) * mm});
            skLineSegment(sketch, "E243.0.2.166", {"start": v(30.21, 64.85) * mm, "end": v(29.68, 65) * mm});
            skLineSegment(sketch, "E243.0.2.167", {"start": v(-23.38, 59.35) * mm, "end": v(-23.96, 59.39) * mm});
            skLineSegment(sketch, "E243.0.2.168", {"start": v(-19.44, 50.06) * mm, "end": v(-19.3, 49.53) * mm});
            skLineSegment(sketch, "E243.0.2.169", {"start": v(30.21, 68.48) * mm, "end": v(30.39, 68.48) * mm});
            skLineSegment(sketch, "E243.0.2.170", {"start": v(9.18, 50.66) * mm, "end": v(8.5, 50.57) * mm});
            skLineSegment(sketch, "E243.0.2.171", {"start": v(-9.26, 47.55) * mm, "end": v(-8.3, 47.66) * mm});
            skLineSegment(sketch, "E243.0.2.172", {"start": v(-22.8, 62.48) * mm, "end": v(-22.7, 62.44) * mm});
            skLineSegment(sketch, "E243.0.2.173", {"start": v(-5.58, 53.5) * mm, "end": v(-5.65, 53.28) * mm});
            skLineSegment(sketch, "E243.0.2.174", {"start": v(-14.31, 60.92) * mm, "end": v(-14.55, 60.71) * mm});
            skLineSegment(sketch, "E243.0.2.175", {"start": v(-23.9, 62.66) * mm, "end": v(-23.33, 62.61) * mm});
            skLineSegment(sketch, "E243.0.2.176", {"start": v(-24.84, 62.63) * mm, "end": v(-24.27, 62.66) * mm});
            skLineSegment(sketch, "E243.0.2.177", {"start": v(-24.27, 62.66) * mm, "end": v(-24.08, 62.66) * mm});
            skLineSegment(sketch, "E243.0.2.178", {"start": v(-29.07, 55.26) * mm, "end": v(-29.17, 54.28) * mm});
            skLineSegment(sketch, "E243.0.2.179", {"start": v(30.57, 68.48) * mm, "end": v(31.1, 68.34) * mm});
            skLineSegment(sketch, "E243.0.2.180", {"start": v(7.96, 50.57) * mm, "end": v(6.99, 50.77) * mm});
            skLineSegment(sketch, "E243.0.2.181", {"start": v(-8.33, 59.22) * mm, "end": v(-8.03, 59.1) * mm});
            skLineSegment(sketch, "E243.0.2.182", {"start": v(-5.55, 61.21) * mm, "end": v(-6.39, 61.69) * mm});
            skLineSegment(sketch, "E243.0.2.183", {"start": v(-5.3, 61.02) * mm, "end": v(-5.55, 61.21) * mm});
            skLineSegment(sketch, "E243.0.2.184", {"start": v(-24.35, 59.39) * mm, "end": v(-25.16, 59.3) * mm});
            skLineSegment(sketch, "E243.0.2.185", {"start": v(30.39, 64.85) * mm, "end": v(30.21, 64.85) * mm});
            skLineSegment(sketch, "E243.0.2.186", {"start": v(30.57, 64.85) * mm, "end": v(30.39, 64.85) * mm});
            skLineSegment(sketch, "E243.0.2.187", {"start": v(4.19, 53.31) * mm, "end": v(4.11, 53.5) * mm});
            skLineSegment(sketch, "E243.0.2.188", {"start": v(-13.51, 61.45) * mm, "end": v(-14.31, 60.92) * mm});
            skLineSegment(sketch, "E243.0.2.189", {"start": v(-19.3, 49.35) * mm, "end": v(-19.3, 49.17) * mm});
            skLineSegment(sketch, "E243.0.2.190", {"start": v(-16.4, 51.64) * mm, "end": v(-16.26, 51.35) * mm});
            skLineSegment(sketch, "E243.0.2.191", {"start": v(-22.93, 49.17) * mm, "end": v(-22.93, 49.35) * mm});
            skLineSegment(sketch, "E243.0.2.192", {"start": v(-8.3, 47.66) * mm, "end": v(-8, 47.74) * mm});
            skLineSegment(sketch, "E243.0.2.193", {"start": v(8, 62.48) * mm, "end": v(7.17, 62.4) * mm});
            skLineSegment(sketch, "E243.0.2.194", {"start": v(-16.54, 51.92) * mm, "end": v(-16.4, 51.64) * mm});
            skLineSegment(sketch, "E243.0.2.195", {"start": v(-22.93, 49.53) * mm, "end": v(-22.79, 50.06) * mm});
            skLineSegment(sketch, "E243.0.2.196", {"start": v(1.38, 57.87) * mm, "end": v(1.28, 57.6) * mm});
            skLineSegment(sketch, "E243.0.2.197", {"start": v(-29.17, 54.28) * mm, "end": v(-29.17, 53.96) * mm});
            skLineSegment(sketch, "E243.0.2.198", {"start": v(15.6, 56.5) * mm, "end": v(15.6, 56.51) * mm});
            skLineSegment(sketch, "E243.0.2.199", {"start": v(-8, 47.74) * mm, "end": v(-7.7, 47.81) * mm});
            skLineSegment(sketch, "E243.0.2.200", {"start": v(-22.79, 48.64) * mm, "end": v(-22.93, 49.17) * mm});
            skLineSegment(sketch, "E243.0.2.201", {"start": v(-14.8, 60.5) * mm, "end": v(-15.46, 59.81) * mm});
            skLineSegment(sketch, "E243.0.2.202", {"start": v(12.37, 53.28) * mm, "end": v(11.96, 52.53) * mm});
            skLineSegment(sketch, "E243.0.2.203", {"start": v(4.87, 52.18) * mm, "end": v(4.31, 53.01) * mm});
            skLineSegment(sketch, "E243.0.2.204", {"start": v(-8.03, 59.1) * mm, "end": v(-7.73, 58.98) * mm});
            skLineSegment(sketch, "E243.0.2.205", {"start": v(30.39, 68.48) * mm, "end": v(30.57, 68.48) * mm});
            skLineSegment(sketch, "E243.0.2.206", {"start": v(-9.3, 59.42) * mm, "end": v(-8.33, 59.22) * mm});
            skLineSegment(sketch, "E243.0.2.207", {"start": v(8.29, 50.57) * mm, "end": v(7.96, 50.57) * mm});
            skLineSegment(sketch, "E243.0.2.208", {"start": v(-16.88, 52.82) * mm, "end": v(-16.54, 51.92) * mm});
            skLineSegment(sketch, "E243.0.2.209", {"start": v(1.49, 58.13) * mm, "end": v(1.38, 57.87) * mm});
            skLineSegment(sketch, "E243.0.2.210", {"start": v(-23.96, 59.39) * mm, "end": v(-24.08, 59.39) * mm});
            skLineSegment(sketch, "E243.0.2.211", {"start": v(31.1, 65) * mm, "end": v(30.57, 64.85) * mm});
            skLineSegment(sketch, "E243.0.2.212", {"start": v(-5.65, 53.28) * mm, "end": v(-6.06, 52.53) * mm});
            skLineSegment(sketch, "E243.0.2.213", {"start": v(-22.81, 59.25) * mm, "end": v(-23.38, 59.35) * mm});
            skLineSegment(sketch, "E243.0.2.214", {"start": v(4.31, 53.01) * mm, "end": v(4.19, 53.31) * mm});
            skLineSegment(sketch, "E243.0.2.215", {"start": v(2.27, 50.57) * mm, "end": v(2.8, 49.92) * mm});
            skLineSegment(sketch, "E243.0.2.216", {"start": v(-19.3, 49.17) * mm, "end": v(-19.44, 48.64) * mm});
            skLineSegment(sketch, "E243.0.2.217", {"start": v(12.44, 53.5) * mm, "end": v(12.37, 53.28) * mm});
            skLineSegment(sketch, "E243.0.2.218", {"start": v(3, 49.72) * mm, "end": v(3.2, 49.53) * mm});
            skLineSegment(sketch, "E243.0.2.219", {"start": v(-22.93, 49.35) * mm, "end": v(-22.93, 49.53) * mm});
            skLineSegment(sketch, "E243.0.2.220", {"start": v(-14.55, 60.71) * mm, "end": v(-14.8, 60.5) * mm});
            skLineSegment(sketch, "E243.0.2.221", {"start": v(-22.7, 59.23) * mm, "end": v(-22.81, 59.25) * mm});
            skLineSegment(sketch, "E243.0.2.222", {"start": v(-24.08, 59.39) * mm, "end": v(-24.35, 59.39) * mm});
            skLineSegment(sketch, "E243.0.2.223", {"start": v(-8.84, 50.66) * mm, "end": v(-9.5, 50.57) * mm});
            skLineSegment(sketch, "E243.0.2.224", {"start": v(-21.82, 51.02) * mm, "end": v(-21.29, 51.17) * mm});
            skLineSegment(sketch, "E243.0.2.225", {"start": v(32.2, 66.49) * mm, "end": v(32.06, 65.96) * mm});
            skLineSegment(sketch, "E243.0.2.226", {"start": v(-21.29, 51.17) * mm, "end": v(-21.11, 51.17) * mm});
            skLineSegment(sketch, "E243.0.2.227", {"start": v(-21.29, 47.53) * mm, "end": v(-21.82, 47.68) * mm});
            skLineSegment(sketch, "E243.0.2.228", {"start": v(-20.4, 47.68) * mm, "end": v(-20.94, 47.53) * mm});
            skLineSegment(sketch, "E243.0.2.229", {"start": v(-9.73, 50.57) * mm, "end": v(-9.73, 50.57) * mm});
            skLineSegment(sketch, "E243.0.2.230", {"start": v(28.57, 66.84) * mm, "end": v(28.72, 67.37) * mm});
            skLineSegment(sketch, "E243.0.2.231", {"start": v(-9.5, 50.57) * mm, "end": v(-9.73, 50.57) * mm});
            skLineSegment(sketch, "E243.0.2.232", {"start": v(-20.94, 51.17) * mm, "end": v(-20.4, 51.02) * mm});
            skLineSegment(sketch, "E243.0.2.233", {"start": v(28.57, 66.66) * mm, "end": v(28.57, 66.84) * mm});
            skLineSegment(sketch, "E243.0.2.234", {"start": v(28.72, 65.96) * mm, "end": v(28.57, 66.49) * mm});
            skLineSegment(sketch, "E243.0.2.235", {"start": v(32.2, 66.84) * mm, "end": v(32.2, 66.66) * mm});
            skLineSegment(sketch, "E243.0.2.236", {"start": v(-21.11, 47.53) * mm, "end": v(-21.29, 47.53) * mm});
            skLineSegment(sketch, "E243.0.2.237", {"start": v(32.06, 67.37) * mm, "end": v(32.2, 66.84) * mm});
            skLineSegment(sketch, "E243.0.2.238", {"start": v(-20.94, 47.53) * mm, "end": v(-21.11, 47.53) * mm});
            skLineSegment(sketch, "E243.0.2.239", {"start": v(-21.11, 51.17) * mm, "end": v(-20.94, 51.17) * mm});
            skLineSegment(sketch, "E243.0.2.240", {"start": v(-9.73, 50.57) * mm, "end": v(-10.06, 50.57) * mm});
            skLineSegment(sketch, "E243.0.2.241", {"start": v(28.57, 66.49) * mm, "end": v(28.57, 66.66) * mm});
            skLineSegment(sketch, "E243.0.2.242", {"start": v(32.2, 66.66) * mm, "end": v(32.2, 66.49) * mm});
            skLineSegment(sketch, "E243.1.0.0", {"start": v(89.98, -0.42) * mm, "end": v(89.98, -12.5) * mm});
            skLineSegment(sketch, "E243.1.0.1", {"start": v(89.98, 12.5) * mm, "end": v(89.98, 2.51) * mm});
            skLineSegment(sketch, "E243.1.0.2", {"start": v(47.3, 2.44) * mm, "end": v(47.3, -0.77) * mm});
            skLineSegment(sketch, "E243.1.0.3", {"start": v(96.4, -0.42) * mm, "end": v(96.4, 2.44) * mm});
            skLineSegment(sketch, "E243.1.0.4", {"start": v(96.4, 2.44) * mm, "end": v(93.05, 2.44) * mm});
            skLineSegment(sketch, "E243.1.0.5", {"start": v(82.43, -3.5) * mm, "end": v(85.6, -3.5) * mm});
            skLineSegment(sketch, "E243.1.0.6", {"start": v(52.95, -3.5) * mm, "end": v(56.15, -3.5) * mm});
            skLineSegment(sketch, "E243.1.0.7", {"start": v(37.8, -12.5) * mm, "end": v(37.8, 2.47) * mm});
            skLineSegment(sketch, "E243.1.0.8", {"start": v(40.83, -6.04) * mm, "end": v(40.83, -12.5) * mm});
            skLineSegment(sketch, "E243.1.0.9", {"start": v(70.98, -3.5) * mm, "end": v(74.16, -3.5) * mm});
            skLineSegment(sketch, "E243.1.0.10", {"start": v(70.97, -6.5) * mm, "end": v(74.11, -6.5) * mm});
            skLineSegment(sketch, "E243.1.0.11", {"start": v(82.44, -6.5) * mm, "end": v(85.58, -6.5) * mm});
            skLineSegment(sketch, "E243.1.0.12", {"start": v(64.7, 12.5) * mm, "end": v(64.7, 1.02) * mm});
            skLineSegment(sketch, "E243.1.0.13", {"start": v(93.05, -12.5) * mm, "end": v(93.05, -0.42) * mm});
            skLineSegment(sketch, "E243.1.0.14", {"start": v(37.8, 2.47) * mm, "end": v(40.83, 2.47) * mm});
            skLineSegment(sketch, "E243.1.0.15", {"start": v(40.83, -12.5) * mm, "end": v(37.8, -12.5) * mm});
            skLineSegment(sketch, "E243.1.0.16", {"start": v(87.6, 2.51) * mm, "end": v(87.6, -0.42) * mm});
            skLineSegment(sketch, "E243.1.0.17", {"start": v(67.74, -3.5) * mm, "end": v(67.78, 12.5) * mm});
            skLineSegment(sketch, "E243.1.0.18", {"start": v(67.78, 12.5) * mm, "end": v(64.7, 12.5) * mm});
            skLineSegment(sketch, "E243.1.0.19", {"start": v(89.98, -12.5) * mm, "end": v(93.05, -12.5) * mm});
            skLineSegment(sketch, "E243.1.0.20", {"start": v(64.42, -6.5) * mm, "end": v(67.57, -6.5) * mm});
            skLineSegment(sketch, "E243.1.0.21", {"start": v(52.98, -6.5) * mm, "end": v(56.1, -6.5) * mm});
            skLineSegment(sketch, "E243.1.0.22", {"start": v(93.05, 12.5) * mm, "end": v(89.98, 12.5) * mm});
            skLineSegment(sketch, "E243.1.0.23", {"start": v(93.05, 2.44) * mm, "end": v(93.05, 12.5) * mm});
            skLineSegment(sketch, "E243.1.0.24", {"start": v(64.42, -3.5) * mm, "end": v(67.74, -3.5) * mm});
            skLineSegment(sketch, "E243.1.0.25", {"start": v(93.05, -0.42) * mm, "end": v(96.4, -0.42) * mm});
            skLineSegment(sketch, "E243.1.0.26", {"start": v(65.3, -10.52) * mm, "end": v(66.13, -9.62) * mm});
            skLineSegment(sketch, "E243.1.0.27", {"start": v(53.29, -2.32) * mm, "end": v(52.95, -3.5) * mm});
            skLineSegment(sketch, "E243.1.0.28", {"start": v(99.1, 7.95) * mm, "end": v(99.68, 8.34) * mm});
            skLineSegment(sketch, "E243.1.0.29", {"start": v(56.17, -6.7) * mm, "end": v(56.05, -6.4) * mm});
            skLineSegment(sketch, "E243.1.0.30", {"start": v(75.82, -8.68) * mm, "end": v(74.87, -7.82) * mm});
            skLineSegment(sketch, "E243.1.0.31", {"start": v(66.81, -8.6) * mm, "end": v(67.32, -7.48) * mm});
            skLineSegment(sketch, "E243.1.0.32", {"start": v(87.6, -0.42) * mm, "end": v(89.98, -0.42) * mm});
            skLineSegment(sketch, "E243.1.0.33", {"start": v(63.21, -11.86) * mm, "end": v(64.32, -11.27) * mm});
            skLineSegment(sketch, "E243.1.0.34", {"start": v(77.42, -0.64) * mm, "end": v(78.7, -0.58) * mm});
            skLineSegment(sketch, "E243.1.0.35", {"start": v(74.78, -11.6) * mm, "end": v(75.78, -12.03) * mm});
            skLineSegment(sketch, "E243.1.0.36", {"start": v(63.94, -7.47) * mm, "end": v(63.4, -8.13) * mm});
            skLineSegment(sketch, "E243.1.0.37", {"start": v(85.17, -2.08) * mm, "end": v(84.48, -0.82) * mm});
            skLineSegment(sketch, "E243.1.0.38", {"start": v(84.5, -9.14) * mm, "end": v(85.03, -8.2) * mm});
            skLineSegment(sketch, "E243.1.0.39", {"start": v(71.68, -8.5) * mm, "end": v(72.27, -9.43) * mm});
            skLineSegment(sketch, "E243.1.0.40", {"start": v(42.26, -1.93) * mm, "end": v(41.66, -2.69) * mm});
            skLineSegment(sketch, "E243.1.0.41", {"start": v(43, -1.35) * mm, "end": v(42.26, -1.93) * mm});
            skLineSegment(sketch, "E243.1.0.42", {"start": v(66.13, -9.62) * mm, "end": v(66.81, -8.6) * mm});
            skLineSegment(sketch, "E243.1.0.43", {"start": v(79.8, 2.33) * mm, "end": v(78.66, 2.48) * mm});
            skLineSegment(sketch, "E243.1.0.44", {"start": v(67.32, -7.48) * mm, "end": v(67.57, -6.5) * mm});
            skLineSegment(sketch, "E243.1.0.45", {"start": v(63.4, -8.13) * mm, "end": v(62.75, -8.67) * mm});
            skLineSegment(sketch, "E243.1.0.46", {"start": v(84.48, -0.82) * mm, "end": v(83.57, 0.3) * mm});
            skLineSegment(sketch, "E243.1.0.47", {"start": v(89.98, 2.51) * mm, "end": v(87.6, 2.51) * mm});
            skLineSegment(sketch, "E243.1.0.48", {"start": v(58.97, -9.24) * mm, "end": v(57.8, -8.68) * mm});
            skLineSegment(sketch, "E243.1.0.49", {"start": v(101.67, 7.95) * mm, "end": v(102.06, 7.37) * mm});
            skLineSegment(sketch, "E243.1.0.50", {"start": v(76.99, -9.23) * mm, "end": v(75.82, -8.68) * mm});
            skLineSegment(sketch, "E243.1.0.51", {"start": v(71.24, -7.5) * mm, "end": v(71.68, -8.5) * mm});
            skLineSegment(sketch, "E243.1.0.52", {"start": v(43.61, 2.35) * mm, "end": v(44.38, 2.52) * mm});
            skLineSegment(sketch, "E243.1.0.53", {"start": v(81.14, -11.9) * mm, "end": v(81.4, -11.79) * mm});
            skLineSegment(sketch, "E243.1.0.54", {"start": v(75.15, -1.86) * mm, "end": v(75.38, -1.63) * mm});
            skLineSegment(sketch, "E243.1.0.55", {"start": v(57.36, -1.63) * mm, "end": v(58.2, -1.08) * mm});
            skLineSegment(sketch, "E243.1.0.56", {"start": v(53.74, -8.65) * mm, "end": v(54.27, -9.45) * mm});
            skLineSegment(sketch, "E243.1.0.57", {"start": v(40.83, 0.52) * mm, "end": v(40.9, 0.65) * mm});
            skLineSegment(sketch, "E243.1.0.58", {"start": v(80.01, -9.08) * mm, "end": v(79.18, -9.34) * mm});
            skLineSegment(sketch, "E243.1.0.59", {"start": v(73.28, 0.55) * mm, "end": v(72.52, -0.23) * mm});
            skLineSegment(sketch, "E243.1.0.60", {"start": v(75.78, -12.03) * mm, "end": v(76.83, -12.32) * mm});
            skLineSegment(sketch, "E243.1.0.61", {"start": v(85.03, -8.2) * mm, "end": v(85.43, -7.18) * mm});
            skLineSegment(sketch, "E243.1.0.62", {"start": v(56.85, -7.82) * mm, "end": v(56.3, -7) * mm});
            skLineSegment(sketch, "E243.1.0.63", {"start": v(81.42, -8.13) * mm, "end": v(80.76, -8.67) * mm});
            skLineSegment(sketch, "E243.1.0.64", {"start": v(59.49, -12.42) * mm, "end": v(60.74, -12.45) * mm});
            skLineSegment(sketch, "E243.1.0.65", {"start": v(81.97, -2.53) * mm, "end": v(82.43, -3.5) * mm});
            skLineSegment(sketch, "E243.1.0.66", {"start": v(41.2, -3.62) * mm, "end": v(40.93, -4.74) * mm});
            skLineSegment(sketch, "E243.1.0.67", {"start": v(80.28, -1.02) * mm, "end": v(81.1, -1.57) * mm});
            skLineSegment(sketch, "E243.1.0.68", {"start": v(79.98, -0.9) * mm, "end": v(80.28, -1.02) * mm});
            skLineSegment(sketch, "E243.1.0.69", {"start": v(47.6, -9.37) * mm, "end": v(48.18, -8.98) * mm});
            skLineSegment(sketch, "E243.1.0.70", {"start": v(62.45, 2.15) * mm, "end": v(61.25, 2.42) * mm});
            skLineSegment(sketch, "E243.1.0.71", {"start": v(80.08, -12.25) * mm, "end": v(80.89, -12) * mm});
            skLineSegment(sketch, "E243.1.0.72", {"start": v(79, -12.43) * mm, "end": v(80.08, -12.25) * mm});
            skLineSegment(sketch, "E243.1.0.73", {"start": v(62.75, -8.67) * mm, "end": v(62, -9.08) * mm});
            skLineSegment(sketch, "E243.1.0.74", {"start": v(75.38, -1.63) * mm, "end": v(76.2, -1.08) * mm});
            skLineSegment(sketch, "E243.1.0.75", {"start": v(74.13, 1.22) * mm, "end": v(73.28, 0.55) * mm});
            skLineSegment(sketch, "E243.1.0.76", {"start": v(76.83, -12.32) * mm, "end": v(77.9, -12.46) * mm});
            skLineSegment(sketch, "E243.1.0.77", {"start": v(47.6, -11.93) * mm, "end": v(47.21, -11.36) * mm});
            skLineSegment(sketch, "E243.1.0.78", {"start": v(76.1, 2.15) * mm, "end": v(75.08, 1.76) * mm});
            skLineSegment(sketch, "E243.1.0.79", {"start": v(63.1, -1.58) * mm, "end": v(63.96, -2.53) * mm});
            skLineSegment(sketch, "E243.1.0.80", {"start": v(75.08, 1.76) * mm, "end": v(74.13, 1.22) * mm});
            skLineSegment(sketch, "E243.1.0.81", {"start": v(63.96, -2.53) * mm, "end": v(64.42, -3.5) * mm});
            skLineSegment(sketch, "E243.1.0.82", {"start": v(54.27, -9.45) * mm, "end": v(55.1, -10.39) * mm});
            skLineSegment(sketch, "E243.1.0.83", {"start": v(61.25, 2.42) * mm, "end": v(60.02, 2.48) * mm});
            skLineSegment(sketch, "E243.1.0.84", {"start": v(83.04, -10.75) * mm, "end": v(83.83, -10) * mm});
            skLineSegment(sketch, "E243.1.0.85", {"start": v(59.4, -0.65) * mm, "end": v(60.7, -0.58) * mm});
            skLineSegment(sketch, "E243.1.0.86", {"start": v(63.61, 1.69) * mm, "end": v(62.45, 2.15) * mm});
            skLineSegment(sketch, "E243.1.0.87", {"start": v(70.97, -6.5) * mm, "end": v(71.24, -7.5) * mm});
            skLineSegment(sketch, "E243.1.0.88", {"start": v(80.76, -8.67) * mm, "end": v(80.01, -9.08) * mm});
            skLineSegment(sketch, "E243.1.0.89", {"start": v(73.85, -11) * mm, "end": v(74.78, -11.6) * mm});
            skLineSegment(sketch, "E243.1.0.90", {"start": v(83.83, -10) * mm, "end": v(84.5, -9.14) * mm});
            skLineSegment(sketch, "E243.1.0.91", {"start": v(57.13, -1.86) * mm, "end": v(57.36, -1.63) * mm});
            skLineSegment(sketch, "E243.1.0.92", {"start": v(40.83, 2.47) * mm, "end": v(40.83, 0.52) * mm});
            skLineSegment(sketch, "E243.1.0.93", {"start": v(56.15, -3.5) * mm, "end": v(56.35, -2.92) * mm});
            skLineSegment(sketch, "E243.1.0.94", {"start": v(74.92, -2.09) * mm, "end": v(75.15, -1.86) * mm});
            skLineSegment(sketch, "E243.1.0.95", {"start": v(57.62, 2) * mm, "end": v(56.49, 1.45) * mm});
            skLineSegment(sketch, "E243.1.0.96", {"start": v(57.12, -11.77) * mm, "end": v(58.27, -12.2) * mm});
            skLineSegment(sketch, "E243.1.0.97", {"start": v(50.17, -11.93) * mm, "end": v(49.6, -12.32) * mm});
            skLineSegment(sketch, "E243.1.0.98", {"start": v(99.1, 5.38) * mm, "end": v(98.72, 5.96) * mm});
            skLineSegment(sketch, "E243.1.0.99", {"start": v(81.4, -11.79) * mm, "end": v(82.14, -11.4) * mm});
            skLineSegment(sketch, "E243.1.0.100", {"start": v(42.88, 2.1) * mm, "end": v(43.61, 2.35) * mm});
            skLineSegment(sketch, "E243.1.0.101", {"start": v(76.2, -1.08) * mm, "end": v(77.42, -0.64) * mm});
            skLineSegment(sketch, "E243.1.0.102", {"start": v(77.9, -12.46) * mm, "end": v(79, -12.43) * mm});
            skLineSegment(sketch, "E243.1.0.103", {"start": v(40.9, 0.65) * mm, "end": v(41.16, 1) * mm});
            skLineSegment(sketch, "E243.1.0.104", {"start": v(41.63, 1.44) * mm, "end": v(42.21, 1.8) * mm});
            skLineSegment(sketch, "E243.1.0.105", {"start": v(62.3, -12.19) * mm, "end": v(63.21, -11.86) * mm});
            skLineSegment(sketch, "E243.1.0.106", {"start": v(77.17, 2.4) * mm, "end": v(76.1, 2.15) * mm});
            skLineSegment(sketch, "E243.1.0.107", {"start": v(50.17, -9.37) * mm, "end": v(50.56, -9.94) * mm});
            skLineSegment(sketch, "E243.1.0.108", {"start": v(74.16, -3.5) * mm, "end": v(74.37, -2.91) * mm});
            skLineSegment(sketch, "E243.1.0.109", {"start": v(58.27, -12.2) * mm, "end": v(59.49, -12.42) * mm});
            skLineSegment(sketch, "E243.1.0.110", {"start": v(62.27, -1.02) * mm, "end": v(63.1, -1.58) * mm});
            skLineSegment(sketch, "E243.1.0.111", {"start": v(82.14, -11.4) * mm, "end": v(83.04, -10.75) * mm});
            skLineSegment(sketch, "E243.1.0.112", {"start": v(71.03, -3.2) * mm, "end": v(70.98, -3.5) * mm});
            skLineSegment(sketch, "E243.1.0.113", {"start": v(101.67, 5.38) * mm, "end": v(101.1, 5) * mm});
            skLineSegment(sketch, "E243.1.0.114", {"start": v(43.87, -0.94) * mm, "end": v(43, -1.35) * mm});
            skLineSegment(sketch, "E243.1.0.115", {"start": v(42.21, 1.8) * mm, "end": v(42.88, 2.1) * mm});
            skLineSegment(sketch, "E243.1.0.116", {"start": v(64.32, -11.27) * mm, "end": v(65.3, -10.52) * mm});
            skLineSegment(sketch, "E243.1.0.117", {"start": v(81.2, 1.9) * mm, "end": v(79.8, 2.33) * mm});
            skLineSegment(sketch, "E243.1.0.118", {"start": v(58.2, -1.08) * mm, "end": v(59.4, -0.65) * mm});
            skLineSegment(sketch, "E243.1.0.119", {"start": v(52.98, -6.5) * mm, "end": v(53.12, -7.18) * mm});
            skLineSegment(sketch, "E243.1.0.120", {"start": v(78.7, -0.58) * mm, "end": v(79.68, -0.77) * mm});
            skLineSegment(sketch, "E243.1.0.121", {"start": v(80.89, -12) * mm, "end": v(81.14, -11.9) * mm});
            skLineSegment(sketch, "E243.1.0.122", {"start": v(79.68, -0.77) * mm, "end": v(79.98, -0.9) * mm});
            skLineSegment(sketch, "E243.1.0.123", {"start": v(82.46, 1.2) * mm, "end": v(81.2, 1.9) * mm});
            skLineSegment(sketch, "E243.1.0.124", {"start": v(83.57, 0.3) * mm, "end": v(82.46, 1.2) * mm});
            skLineSegment(sketch, "E243.1.0.125", {"start": v(56.35, -2.92) * mm, "end": v(56.9, -2.1) * mm});
            skLineSegment(sketch, "E243.1.0.126", {"start": v(53.82, -1.21) * mm, "end": v(53.29, -2.32) * mm});
            skLineSegment(sketch, "E243.1.0.127", {"start": v(62, -9.08) * mm, "end": v(61.16, -9.34) * mm});
            skLineSegment(sketch, "E243.1.0.128", {"start": v(41.16, 1) * mm, "end": v(41.63, 1.44) * mm});
            skLineSegment(sketch, "E243.1.0.129", {"start": v(74.37, -2.91) * mm, "end": v(74.92, -2.09) * mm});
            skLineSegment(sketch, "E243.1.0.130", {"start": v(54.54, -0.19) * mm, "end": v(53.82, -1.21) * mm});
            skLineSegment(sketch, "E243.1.0.131", {"start": v(81.96, -7.47) * mm, "end": v(81.42, -8.13) * mm});
            skLineSegment(sketch, "E243.1.0.132", {"start": v(60.02, 2.48) * mm, "end": v(58.8, 2.33) * mm});
            skLineSegment(sketch, "E243.1.0.133", {"start": v(56.06, -11.16) * mm, "end": v(57.12, -11.77) * mm});
            skLineSegment(sketch, "E243.1.0.134", {"start": v(58.8, 2.33) * mm, "end": v(57.62, 2) * mm});
            skLineSegment(sketch, "E243.1.0.135", {"start": v(81.1, -1.57) * mm, "end": v(81.97, -2.53) * mm});
            skLineSegment(sketch, "E243.1.0.136", {"start": v(56.9, -2.1) * mm, "end": v(57.13, -1.86) * mm});
            skLineSegment(sketch, "E243.1.0.137", {"start": v(56.3, -7) * mm, "end": v(56.17, -6.7) * mm});
            skLineSegment(sketch, "E243.1.0.138", {"start": v(72.52, -0.23) * mm, "end": v(71.89, -1.13) * mm});
            skLineSegment(sketch, "E243.1.0.139", {"start": v(85.43, -7.18) * mm, "end": v(85.58, -6.5) * mm});
            skLineSegment(sketch, "E243.1.0.140", {"start": v(57.8, -8.68) * mm, "end": v(56.85, -7.82) * mm});
            skLineSegment(sketch, "E243.1.0.141", {"start": v(55.1, -10.39) * mm, "end": v(56.06, -11.16) * mm});
            skLineSegment(sketch, "E243.1.0.142", {"start": v(41.66, -2.69) * mm, "end": v(41.2, -3.62) * mm});
            skLineSegment(sketch, "E243.1.0.143", {"start": v(98.72, 7.37) * mm, "end": v(99.1, 7.95) * mm});
            skLineSegment(sketch, "E243.1.0.144", {"start": v(85.6, -3.49) * mm, "end": v(85.17, -2.08) * mm});
            skLineSegment(sketch, "E243.1.0.145", {"start": v(47.21, -9.94) * mm, "end": v(47.6, -9.37) * mm});
            skLineSegment(sketch, "E243.1.0.146", {"start": v(99.68, 5) * mm, "end": v(99.1, 5.38) * mm});
            skLineSegment(sketch, "E243.1.0.147", {"start": v(71.28, -2.4) * mm, "end": v(71.03, -3.2) * mm});
            skLineSegment(sketch, "E243.1.0.148", {"start": v(50.56, -11.36) * mm, "end": v(50.17, -11.93) * mm});
            skLineSegment(sketch, "E243.1.0.149", {"start": v(49.6, -8.98) * mm, "end": v(50.17, -9.37) * mm});
            skLineSegment(sketch, "E243.1.0.150", {"start": v(101.1, 8.34) * mm, "end": v(101.67, 7.95) * mm});
            skLineSegment(sketch, "E243.1.0.151", {"start": v(44.38, 2.52) * mm, "end": v(45.16, 2.63) * mm});
            skLineSegment(sketch, "E243.1.0.152", {"start": v(102.06, 5.96) * mm, "end": v(101.67, 5.38) * mm});
            skLineSegment(sketch, "E243.1.0.153", {"start": v(44.84, -0.7) * mm, "end": v(43.87, -0.94) * mm});
            skLineSegment(sketch, "E243.1.0.154", {"start": v(48.18, -12.32) * mm, "end": v(47.6, -11.93) * mm});
            skLineSegment(sketch, "E243.1.0.155", {"start": v(73.2, -10.47) * mm, "end": v(73.85, -11) * mm});
            skLineSegment(sketch, "E243.1.0.156", {"start": v(46.67, 2.61) * mm, "end": v(47.2, 2.48) * mm});
            skLineSegment(sketch, "E243.1.0.157", {"start": v(78.29, 2.48) * mm, "end": v(78, 2.48) * mm});
            skLineSegment(sketch, "E243.1.0.158", {"start": v(59.94, -9.43) * mm, "end": v(58.97, -9.24) * mm});
            skLineSegment(sketch, "E243.1.0.159", {"start": v(78.66, 2.48) * mm, "end": v(78.29, 2.48) * mm});
            skLineSegment(sketch, "E243.1.0.160", {"start": v(99.68, 8.34) * mm, "end": v(100.21, 8.48) * mm});
            skLineSegment(sketch, "E243.1.0.161", {"start": v(78.5, -9.43) * mm, "end": v(78.29, -9.43) * mm});
            skLineSegment(sketch, "E243.1.0.162", {"start": v(71.89, -1.13) * mm, "end": v(71.49, -1.87) * mm});
            skLineSegment(sketch, "E243.1.0.163", {"start": v(45.92, 2.66) * mm, "end": v(46.1, 2.66) * mm});
            skLineSegment(sketch, "E243.1.0.164", {"start": v(50.7, -10.47) * mm, "end": v(50.7, -10.65) * mm});
            skLineSegment(sketch, "E243.1.0.165", {"start": v(72.8, -10.08) * mm, "end": v(73, -10.28) * mm});
            skLineSegment(sketch, "E243.1.0.166", {"start": v(100.21, 4.85) * mm, "end": v(99.68, 5) * mm});
            skLineSegment(sketch, "E243.1.0.167", {"start": v(46.62, -0.65) * mm, "end": v(46.04, -0.61) * mm});
            skLineSegment(sketch, "E243.1.0.168", {"start": v(50.56, -9.94) * mm, "end": v(50.7, -10.47) * mm});
            skLineSegment(sketch, "E243.1.0.169", {"start": v(100.21, 8.48) * mm, "end": v(100.39, 8.48) * mm});
            skLineSegment(sketch, "E243.1.0.170", {"start": v(79.18, -9.34) * mm, "end": v(78.5, -9.43) * mm});
            skLineSegment(sketch, "E243.1.0.171", {"start": v(60.74, -12.45) * mm, "end": v(61.7, -12.34) * mm});
            skLineSegment(sketch, "E243.1.0.172", {"start": v(47.2, 2.48) * mm, "end": v(47.3, 2.44) * mm});
            skLineSegment(sketch, "E243.1.0.173", {"start": v(64.42, -6.5) * mm, "end": v(64.35, -6.72) * mm});
            skLineSegment(sketch, "E243.1.0.174", {"start": v(55.69, 0.92) * mm, "end": v(55.45, 0.71) * mm});
            skLineSegment(sketch, "E243.1.0.175", {"start": v(46.1, 2.66) * mm, "end": v(46.67, 2.61) * mm});
            skLineSegment(sketch, "E243.1.0.176", {"start": v(45.16, 2.63) * mm, "end": v(45.73, 2.66) * mm});
            skLineSegment(sketch, "E243.1.0.177", {"start": v(45.73, 2.66) * mm, "end": v(45.92, 2.66) * mm});
            skLineSegment(sketch, "E243.1.0.178", {"start": v(40.93, -4.74) * mm, "end": v(40.83, -5.72) * mm});
            skLineSegment(sketch, "E243.1.0.179", {"start": v(100.57, 8.48) * mm, "end": v(101.1, 8.34) * mm});
            skLineSegment(sketch, "E243.1.0.180", {"start": v(77.96, -9.43) * mm, "end": v(76.99, -9.23) * mm});
            skLineSegment(sketch, "E243.1.0.181", {"start": v(61.67, -0.78) * mm, "end": v(61.97, -0.9) * mm});
            skLineSegment(sketch, "E243.1.0.182", {"start": v(64.45, 1.21) * mm, "end": v(63.61, 1.69) * mm});
            skLineSegment(sketch, "E243.1.0.183", {"start": v(64.7, 1.02) * mm, "end": v(64.45, 1.21) * mm});
            skLineSegment(sketch, "E243.1.0.184", {"start": v(45.65, -0.61) * mm, "end": v(44.84, -0.7) * mm});
            skLineSegment(sketch, "E243.1.0.185", {"start": v(100.39, 4.85) * mm, "end": v(100.21, 4.85) * mm});
            skLineSegment(sketch, "E243.1.0.186", {"start": v(100.57, 4.85) * mm, "end": v(100.39, 4.85) * mm});
            skLineSegment(sketch, "E243.1.0.187", {"start": v(74.19, -6.69) * mm, "end": v(74.11, -6.5) * mm});
            skLineSegment(sketch, "E243.1.0.188", {"start": v(56.49, 1.45) * mm, "end": v(55.69, 0.92) * mm});
            skLineSegment(sketch, "E243.1.0.189", {"start": v(50.7, -10.65) * mm, "end": v(50.7, -10.83) * mm});
            skLineSegment(sketch, "E243.1.0.190", {"start": v(53.6, -8.36) * mm, "end": v(53.74, -8.65) * mm});
            skLineSegment(sketch, "E243.1.0.191", {"start": v(47.07, -10.83) * mm, "end": v(47.07, -10.65) * mm});
            skLineSegment(sketch, "E243.1.0.192", {"start": v(61.7, -12.34) * mm, "end": v(62, -12.26) * mm});
            skLineSegment(sketch, "E243.1.0.193", {"start": v(78, 2.48) * mm, "end": v(77.17, 2.4) * mm});
            skLineSegment(sketch, "E243.1.0.194", {"start": v(53.46, -8.08) * mm, "end": v(53.6, -8.36) * mm});
            skLineSegment(sketch, "E243.1.0.195", {"start": v(47.07, -10.47) * mm, "end": v(47.21, -9.94) * mm});
            skLineSegment(sketch, "E243.1.0.196", {"start": v(71.38, -2.13) * mm, "end": v(71.28, -2.4) * mm});
            skLineSegment(sketch, "E243.1.0.197", {"start": v(40.83, -5.72) * mm, "end": v(40.83, -6.04) * mm});
            skLineSegment(sketch, "E243.1.0.198", {"start": v(85.6, -3.5) * mm, "end": v(85.6, -3.49) * mm});
            skLineSegment(sketch, "E243.1.0.199", {"start": v(62, -12.26) * mm, "end": v(62.3, -12.19) * mm});
            skLineSegment(sketch, "E243.1.0.200", {"start": v(47.21, -11.36) * mm, "end": v(47.07, -10.83) * mm});
            skLineSegment(sketch, "E243.1.0.201", {"start": v(55.2, 0.5) * mm, "end": v(54.54, -0.19) * mm});
            skLineSegment(sketch, "E243.1.0.202", {"start": v(82.37, -6.72) * mm, "end": v(81.96, -7.47) * mm});
            skLineSegment(sketch, "E243.1.0.203", {"start": v(74.87, -7.82) * mm, "end": v(74.31, -6.99) * mm});
            skLineSegment(sketch, "E243.1.0.204", {"start": v(61.97, -0.9) * mm, "end": v(62.27, -1.02) * mm});
            skLineSegment(sketch, "E243.1.0.205", {"start": v(100.39, 8.48) * mm, "end": v(100.57, 8.48) * mm});
            skLineSegment(sketch, "E243.1.0.206", {"start": v(60.7, -0.58) * mm, "end": v(61.67, -0.78) * mm});
            skLineSegment(sketch, "E243.1.0.207", {"start": v(78.29, -9.43) * mm, "end": v(77.96, -9.43) * mm});
            skLineSegment(sketch, "E243.1.0.208", {"start": v(53.12, -7.18) * mm, "end": v(53.46, -8.08) * mm});
            skLineSegment(sketch, "E243.1.0.209", {"start": v(71.49, -1.87) * mm, "end": v(71.38, -2.13) * mm});
            skLineSegment(sketch, "E243.1.0.210", {"start": v(46.04, -0.61) * mm, "end": v(45.92, -0.61) * mm});
            skLineSegment(sketch, "E243.1.0.211", {"start": v(101.1, 5) * mm, "end": v(100.57, 4.85) * mm});
            skLineSegment(sketch, "E243.1.0.212", {"start": v(64.35, -6.72) * mm, "end": v(63.94, -7.47) * mm});
            skLineSegment(sketch, "E243.1.0.213", {"start": v(47.19, -0.75) * mm, "end": v(46.62, -0.65) * mm});
            skLineSegment(sketch, "E243.1.0.214", {"start": v(74.31, -6.99) * mm, "end": v(74.19, -6.69) * mm});
            skLineSegment(sketch, "E243.1.0.215", {"start": v(72.27, -9.43) * mm, "end": v(72.8, -10.08) * mm});
            skLineSegment(sketch, "E243.1.0.216", {"start": v(50.7, -10.83) * mm, "end": v(50.56, -11.36) * mm});
            skLineSegment(sketch, "E243.1.0.217", {"start": v(82.44, -6.5) * mm, "end": v(82.37, -6.72) * mm});
            skLineSegment(sketch, "E243.1.0.218", {"start": v(73, -10.28) * mm, "end": v(73.2, -10.47) * mm});
            skLineSegment(sketch, "E243.1.0.219", {"start": v(47.07, -10.65) * mm, "end": v(47.07, -10.47) * mm});
            skLineSegment(sketch, "E243.1.0.220", {"start": v(55.45, 0.71) * mm, "end": v(55.2, 0.5) * mm});
            skLineSegment(sketch, "E243.1.0.221", {"start": v(47.3, -0.77) * mm, "end": v(47.19, -0.75) * mm});
            skLineSegment(sketch, "E243.1.0.222", {"start": v(45.92, -0.61) * mm, "end": v(45.65, -0.61) * mm});
            skLineSegment(sketch, "E243.1.0.223", {"start": v(61.16, -9.34) * mm, "end": v(60.5, -9.43) * mm});
            skLineSegment(sketch, "E243.1.0.224", {"start": v(48.18, -8.98) * mm, "end": v(48.71, -8.83) * mm});
            skLineSegment(sketch, "E243.1.0.225", {"start": v(102.2, 6.49) * mm, "end": v(102.06, 5.96) * mm});
            skLineSegment(sketch, "E243.1.0.226", {"start": v(48.71, -8.83) * mm, "end": v(48.89, -8.83) * mm});
            skLineSegment(sketch, "E243.1.0.227", {"start": v(48.71, -12.47) * mm, "end": v(48.18, -12.32) * mm});
            skLineSegment(sketch, "E243.1.0.228", {"start": v(49.6, -12.32) * mm, "end": v(49.06, -12.47) * mm});
            skLineSegment(sketch, "E243.1.0.229", {"start": v(60.27, -9.43) * mm, "end": v(60.27, -9.43) * mm});
            skLineSegment(sketch, "E243.1.0.230", {"start": v(98.57, 6.84) * mm, "end": v(98.72, 7.37) * mm});
            skLineSegment(sketch, "E243.1.0.231", {"start": v(60.5, -9.43) * mm, "end": v(60.27, -9.43) * mm});
            skLineSegment(sketch, "E243.1.0.232", {"start": v(49.06, -8.83) * mm, "end": v(49.6, -8.98) * mm});
            skLineSegment(sketch, "E243.1.0.233", {"start": v(98.57, 6.66) * mm, "end": v(98.57, 6.84) * mm});
            skLineSegment(sketch, "E243.1.0.234", {"start": v(98.72, 5.96) * mm, "end": v(98.57, 6.49) * mm});
            skLineSegment(sketch, "E243.1.0.235", {"start": v(102.2, 6.84) * mm, "end": v(102.2, 6.66) * mm});
            skLineSegment(sketch, "E243.1.0.236", {"start": v(48.89, -12.47) * mm, "end": v(48.71, -12.47) * mm});
            skLineSegment(sketch, "E243.1.0.237", {"start": v(102.06, 7.37) * mm, "end": v(102.2, 6.84) * mm});
            skLineSegment(sketch, "E243.1.0.238", {"start": v(49.06, -12.47) * mm, "end": v(48.89, -12.47) * mm});
            skLineSegment(sketch, "E243.1.0.239", {"start": v(48.89, -8.83) * mm, "end": v(49.06, -8.83) * mm});
            skLineSegment(sketch, "E243.1.0.240", {"start": v(60.27, -9.43) * mm, "end": v(59.94, -9.43) * mm});
            skLineSegment(sketch, "E243.1.0.241", {"start": v(98.57, 6.49) * mm, "end": v(98.57, 6.66) * mm});
            skLineSegment(sketch, "E243.1.0.242", {"start": v(102.2, 6.66) * mm, "end": v(102.2, 6.49) * mm});
            skLineSegment(sketch, "E243.1.1.0", {"start": v(89.98, 29.58) * mm, "end": v(89.98, 17.5) * mm});
            skLineSegment(sketch, "E243.1.1.1", {"start": v(89.98, 42.5) * mm, "end": v(89.98, 32.51) * mm});
            skLineSegment(sketch, "E243.1.1.2", {"start": v(47.3, 32.44) * mm, "end": v(47.3, 29.23) * mm});
            skLineSegment(sketch, "E243.1.1.3", {"start": v(96.4, 29.58) * mm, "end": v(96.4, 32.44) * mm});
            skLineSegment(sketch, "E243.1.1.4", {"start": v(96.4, 32.44) * mm, "end": v(93.05, 32.44) * mm});
            skLineSegment(sketch, "E243.1.1.5", {"start": v(82.43, 26.5) * mm, "end": v(85.6, 26.5) * mm});
            skLineSegment(sketch, "E243.1.1.6", {"start": v(52.95, 26.5) * mm, "end": v(56.15, 26.5) * mm});
            skLineSegment(sketch, "E243.1.1.7", {"start": v(37.8, 17.5) * mm, "end": v(37.8, 32.47) * mm});
            skLineSegment(sketch, "E243.1.1.8", {"start": v(40.83, 23.96) * mm, "end": v(40.83, 17.5) * mm});
            skLineSegment(sketch, "E243.1.1.9", {"start": v(70.98, 26.5) * mm, "end": v(74.16, 26.5) * mm});
            skLineSegment(sketch, "E243.1.1.10", {"start": v(70.97, 23.5) * mm, "end": v(74.11, 23.5) * mm});
            skLineSegment(sketch, "E243.1.1.11", {"start": v(82.44, 23.5) * mm, "end": v(85.58, 23.5) * mm});
            skLineSegment(sketch, "E243.1.1.12", {"start": v(64.7, 42.5) * mm, "end": v(64.7, 31.02) * mm});
            skLineSegment(sketch, "E243.1.1.13", {"start": v(93.05, 17.5) * mm, "end": v(93.05, 29.58) * mm});
            skLineSegment(sketch, "E243.1.1.14", {"start": v(37.8, 32.47) * mm, "end": v(40.83, 32.47) * mm});
            skLineSegment(sketch, "E243.1.1.15", {"start": v(40.83, 17.5) * mm, "end": v(37.8, 17.5) * mm});
            skLineSegment(sketch, "E243.1.1.16", {"start": v(87.6, 32.51) * mm, "end": v(87.6, 29.58) * mm});
            skLineSegment(sketch, "E243.1.1.17", {"start": v(67.74, 26.5) * mm, "end": v(67.78, 42.5) * mm});
            skLineSegment(sketch, "E243.1.1.18", {"start": v(67.78, 42.5) * mm, "end": v(64.7, 42.5) * mm});
            skLineSegment(sketch, "E243.1.1.19", {"start": v(89.98, 17.5) * mm, "end": v(93.05, 17.5) * mm});
            skLineSegment(sketch, "E243.1.1.20", {"start": v(64.42, 23.5) * mm, "end": v(67.57, 23.5) * mm});
            skLineSegment(sketch, "E243.1.1.21", {"start": v(52.98, 23.5) * mm, "end": v(56.1, 23.5) * mm});
            skLineSegment(sketch, "E243.1.1.22", {"start": v(93.05, 42.5) * mm, "end": v(89.98, 42.5) * mm});
            skLineSegment(sketch, "E243.1.1.23", {"start": v(93.05, 32.44) * mm, "end": v(93.05, 42.5) * mm});
            skLineSegment(sketch, "E243.1.1.24", {"start": v(64.42, 26.5) * mm, "end": v(67.74, 26.5) * mm});
            skLineSegment(sketch, "E243.1.1.25", {"start": v(93.05, 29.58) * mm, "end": v(96.4, 29.58) * mm});
            skLineSegment(sketch, "E243.1.1.26", {"start": v(65.3, 19.48) * mm, "end": v(66.13, 20.38) * mm});
            skLineSegment(sketch, "E243.1.1.27", {"start": v(53.29, 27.68) * mm, "end": v(52.95, 26.5) * mm});
            skLineSegment(sketch, "E243.1.1.28", {"start": v(99.1, 37.95) * mm, "end": v(99.68, 38.34) * mm});
            skLineSegment(sketch, "E243.1.1.29", {"start": v(56.17, 23.3) * mm, "end": v(56.05, 23.6) * mm});
            skLineSegment(sketch, "E243.1.1.30", {"start": v(75.82, 21.32) * mm, "end": v(74.87, 22.18) * mm});
            skLineSegment(sketch, "E243.1.1.31", {"start": v(66.81, 21.4) * mm, "end": v(67.32, 22.52) * mm});
            skLineSegment(sketch, "E243.1.1.32", {"start": v(87.6, 29.58) * mm, "end": v(89.98, 29.58) * mm});
            skLineSegment(sketch, "E243.1.1.33", {"start": v(63.21, 18.14) * mm, "end": v(64.32, 18.73) * mm});
            skLineSegment(sketch, "E243.1.1.34", {"start": v(77.42, 29.36) * mm, "end": v(78.7, 29.42) * mm});
            skLineSegment(sketch, "E243.1.1.35", {"start": v(74.78, 18.4) * mm, "end": v(75.78, 17.97) * mm});
            skLineSegment(sketch, "E243.1.1.36", {"start": v(63.94, 22.53) * mm, "end": v(63.4, 21.87) * mm});
            skLineSegment(sketch, "E243.1.1.37", {"start": v(85.17, 27.92) * mm, "end": v(84.48, 29.18) * mm});
            skLineSegment(sketch, "E243.1.1.38", {"start": v(84.5, 20.86) * mm, "end": v(85.03, 21.8) * mm});
            skLineSegment(sketch, "E243.1.1.39", {"start": v(71.68, 21.5) * mm, "end": v(72.27, 20.57) * mm});
            skLineSegment(sketch, "E243.1.1.40", {"start": v(42.26, 28.07) * mm, "end": v(41.66, 27.31) * mm});
            skLineSegment(sketch, "E243.1.1.41", {"start": v(43, 28.65) * mm, "end": v(42.26, 28.07) * mm});
            skLineSegment(sketch, "E243.1.1.42", {"start": v(66.13, 20.38) * mm, "end": v(66.81, 21.4) * mm});
            skLineSegment(sketch, "E243.1.1.43", {"start": v(79.8, 32.33) * mm, "end": v(78.66, 32.48) * mm});
            skLineSegment(sketch, "E243.1.1.44", {"start": v(67.32, 22.52) * mm, "end": v(67.57, 23.5) * mm});
            skLineSegment(sketch, "E243.1.1.45", {"start": v(63.4, 21.87) * mm, "end": v(62.75, 21.33) * mm});
            skLineSegment(sketch, "E243.1.1.46", {"start": v(84.48, 29.18) * mm, "end": v(83.57, 30.3) * mm});
            skLineSegment(sketch, "E243.1.1.47", {"start": v(89.98, 32.51) * mm, "end": v(87.6, 32.51) * mm});
            skLineSegment(sketch, "E243.1.1.48", {"start": v(58.97, 20.76) * mm, "end": v(57.8, 21.32) * mm});
            skLineSegment(sketch, "E243.1.1.49", {"start": v(101.67, 37.95) * mm, "end": v(102.06, 37.37) * mm});
            skLineSegment(sketch, "E243.1.1.50", {"start": v(76.99, 20.77) * mm, "end": v(75.82, 21.32) * mm});
            skLineSegment(sketch, "E243.1.1.51", {"start": v(71.24, 22.5) * mm, "end": v(71.68, 21.5) * mm});
            skLineSegment(sketch, "E243.1.1.52", {"start": v(43.61, 32.35) * mm, "end": v(44.38, 32.52) * mm});
            skLineSegment(sketch, "E243.1.1.53", {"start": v(81.14, 18.1) * mm, "end": v(81.4, 18.21) * mm});
            skLineSegment(sketch, "E243.1.1.54", {"start": v(75.15, 28.14) * mm, "end": v(75.38, 28.37) * mm});
            skLineSegment(sketch, "E243.1.1.55", {"start": v(57.36, 28.37) * mm, "end": v(58.2, 28.92) * mm});
            skLineSegment(sketch, "E243.1.1.56", {"start": v(53.74, 21.35) * mm, "end": v(54.27, 20.55) * mm});
            skLineSegment(sketch, "E243.1.1.57", {"start": v(40.83, 30.52) * mm, "end": v(40.9, 30.65) * mm});
            skLineSegment(sketch, "E243.1.1.58", {"start": v(80.01, 20.92) * mm, "end": v(79.18, 20.66) * mm});
            skLineSegment(sketch, "E243.1.1.59", {"start": v(73.28, 30.55) * mm, "end": v(72.52, 29.77) * mm});
            skLineSegment(sketch, "E243.1.1.60", {"start": v(75.78, 17.97) * mm, "end": v(76.83, 17.68) * mm});
            skLineSegment(sketch, "E243.1.1.61", {"start": v(85.03, 21.8) * mm, "end": v(85.43, 22.82) * mm});
            skLineSegment(sketch, "E243.1.1.62", {"start": v(56.85, 22.18) * mm, "end": v(56.3, 23) * mm});
            skLineSegment(sketch, "E243.1.1.63", {"start": v(81.42, 21.87) * mm, "end": v(80.76, 21.33) * mm});
            skLineSegment(sketch, "E243.1.1.64", {"start": v(59.49, 17.58) * mm, "end": v(60.74, 17.55) * mm});
            skLineSegment(sketch, "E243.1.1.65", {"start": v(81.97, 27.47) * mm, "end": v(82.43, 26.5) * mm});
            skLineSegment(sketch, "E243.1.1.66", {"start": v(41.2, 26.38) * mm, "end": v(40.93, 25.26) * mm});
            skLineSegment(sketch, "E243.1.1.67", {"start": v(80.28, 28.98) * mm, "end": v(81.1, 28.43) * mm});
            skLineSegment(sketch, "E243.1.1.68", {"start": v(79.98, 29.1) * mm, "end": v(80.28, 28.98) * mm});
            skLineSegment(sketch, "E243.1.1.69", {"start": v(47.6, 20.63) * mm, "end": v(48.18, 21.02) * mm});
            skLineSegment(sketch, "E243.1.1.70", {"start": v(62.45, 32.15) * mm, "end": v(61.25, 32.42) * mm});
            skLineSegment(sketch, "E243.1.1.71", {"start": v(80.08, 17.75) * mm, "end": v(80.89, 18) * mm});
            skLineSegment(sketch, "E243.1.1.72", {"start": v(79, 17.57) * mm, "end": v(80.08, 17.75) * mm});
            skLineSegment(sketch, "E243.1.1.73", {"start": v(62.75, 21.33) * mm, "end": v(62, 20.92) * mm});
            skLineSegment(sketch, "E243.1.1.74", {"start": v(75.38, 28.37) * mm, "end": v(76.2, 28.92) * mm});
            skLineSegment(sketch, "E243.1.1.75", {"start": v(74.13, 31.22) * mm, "end": v(73.28, 30.55) * mm});
            skLineSegment(sketch, "E243.1.1.76", {"start": v(76.83, 17.68) * mm, "end": v(77.9, 17.54) * mm});
            skLineSegment(sketch, "E243.1.1.77", {"start": v(47.6, 18.07) * mm, "end": v(47.21, 18.64) * mm});
            skLineSegment(sketch, "E243.1.1.78", {"start": v(76.1, 32.15) * mm, "end": v(75.08, 31.76) * mm});
            skLineSegment(sketch, "E243.1.1.79", {"start": v(63.1, 28.42) * mm, "end": v(63.96, 27.47) * mm});
            skLineSegment(sketch, "E243.1.1.80", {"start": v(75.08, 31.76) * mm, "end": v(74.13, 31.22) * mm});
            skLineSegment(sketch, "E243.1.1.81", {"start": v(63.96, 27.47) * mm, "end": v(64.42, 26.5) * mm});
            skLineSegment(sketch, "E243.1.1.82", {"start": v(54.27, 20.55) * mm, "end": v(55.1, 19.61) * mm});
            skLineSegment(sketch, "E243.1.1.83", {"start": v(61.25, 32.42) * mm, "end": v(60.02, 32.48) * mm});
            skLineSegment(sketch, "E243.1.1.84", {"start": v(83.04, 19.25) * mm, "end": v(83.83, 20) * mm});
            skLineSegment(sketch, "E243.1.1.85", {"start": v(59.4, 29.35) * mm, "end": v(60.7, 29.42) * mm});
            skLineSegment(sketch, "E243.1.1.86", {"start": v(63.61, 31.69) * mm, "end": v(62.45, 32.15) * mm});
            skLineSegment(sketch, "E243.1.1.87", {"start": v(70.97, 23.5) * mm, "end": v(71.24, 22.5) * mm});
            skLineSegment(sketch, "E243.1.1.88", {"start": v(80.76, 21.33) * mm, "end": v(80.01, 20.92) * mm});
            skLineSegment(sketch, "E243.1.1.89", {"start": v(73.85, 19) * mm, "end": v(74.78, 18.4) * mm});
            skLineSegment(sketch, "E243.1.1.90", {"start": v(83.83, 20) * mm, "end": v(84.5, 20.86) * mm});
            skLineSegment(sketch, "E243.1.1.91", {"start": v(57.13, 28.14) * mm, "end": v(57.36, 28.37) * mm});
            skLineSegment(sketch, "E243.1.1.92", {"start": v(40.83, 32.47) * mm, "end": v(40.83, 30.52) * mm});
            skLineSegment(sketch, "E243.1.1.93", {"start": v(56.15, 26.5) * mm, "end": v(56.35, 27.08) * mm});
            skLineSegment(sketch, "E243.1.1.94", {"start": v(74.92, 27.91) * mm, "end": v(75.15, 28.14) * mm});
            skLineSegment(sketch, "E243.1.1.95", {"start": v(57.62, 32) * mm, "end": v(56.49, 31.45) * mm});
            skLineSegment(sketch, "E243.1.1.96", {"start": v(57.12, 18.23) * mm, "end": v(58.27, 17.8) * mm});
            skLineSegment(sketch, "E243.1.1.97", {"start": v(50.17, 18.07) * mm, "end": v(49.6, 17.68) * mm});
            skLineSegment(sketch, "E243.1.1.98", {"start": v(99.1, 35.38) * mm, "end": v(98.72, 35.96) * mm});
            skLineSegment(sketch, "E243.1.1.99", {"start": v(81.4, 18.21) * mm, "end": v(82.14, 18.6) * mm});
            skLineSegment(sketch, "E243.1.1.100", {"start": v(42.88, 32.1) * mm, "end": v(43.61, 32.35) * mm});
            skLineSegment(sketch, "E243.1.1.101", {"start": v(76.2, 28.92) * mm, "end": v(77.42, 29.36) * mm});
            skLineSegment(sketch, "E243.1.1.102", {"start": v(77.9, 17.54) * mm, "end": v(79, 17.57) * mm});
            skLineSegment(sketch, "E243.1.1.103", {"start": v(40.9, 30.65) * mm, "end": v(41.16, 31) * mm});
            skLineSegment(sketch, "E243.1.1.104", {"start": v(41.63, 31.44) * mm, "end": v(42.21, 31.8) * mm});
            skLineSegment(sketch, "E243.1.1.105", {"start": v(62.3, 17.81) * mm, "end": v(63.21, 18.14) * mm});
            skLineSegment(sketch, "E243.1.1.106", {"start": v(77.17, 32.4) * mm, "end": v(76.1, 32.15) * mm});
            skLineSegment(sketch, "E243.1.1.107", {"start": v(50.17, 20.63) * mm, "end": v(50.56, 20.06) * mm});
            skLineSegment(sketch, "E243.1.1.108", {"start": v(74.16, 26.5) * mm, "end": v(74.37, 27.09) * mm});
            skLineSegment(sketch, "E243.1.1.109", {"start": v(58.27, 17.8) * mm, "end": v(59.49, 17.58) * mm});
            skLineSegment(sketch, "E243.1.1.110", {"start": v(62.27, 28.98) * mm, "end": v(63.1, 28.42) * mm});
            skLineSegment(sketch, "E243.1.1.111", {"start": v(82.14, 18.6) * mm, "end": v(83.04, 19.25) * mm});
            skLineSegment(sketch, "E243.1.1.112", {"start": v(71.03, 26.8) * mm, "end": v(70.98, 26.5) * mm});
            skLineSegment(sketch, "E243.1.1.113", {"start": v(101.67, 35.38) * mm, "end": v(101.1, 35) * mm});
            skLineSegment(sketch, "E243.1.1.114", {"start": v(43.87, 29.06) * mm, "end": v(43, 28.65) * mm});
            skLineSegment(sketch, "E243.1.1.115", {"start": v(42.21, 31.8) * mm, "end": v(42.88, 32.1) * mm});
            skLineSegment(sketch, "E243.1.1.116", {"start": v(64.32, 18.73) * mm, "end": v(65.3, 19.48) * mm});
            skLineSegment(sketch, "E243.1.1.117", {"start": v(81.2, 31.9) * mm, "end": v(79.8, 32.33) * mm});
            skLineSegment(sketch, "E243.1.1.118", {"start": v(58.2, 28.92) * mm, "end": v(59.4, 29.35) * mm});
            skLineSegment(sketch, "E243.1.1.119", {"start": v(52.98, 23.5) * mm, "end": v(53.12, 22.82) * mm});
            skLineSegment(sketch, "E243.1.1.120", {"start": v(78.7, 29.42) * mm, "end": v(79.68, 29.23) * mm});
            skLineSegment(sketch, "E243.1.1.121", {"start": v(80.89, 18) * mm, "end": v(81.14, 18.1) * mm});
            skLineSegment(sketch, "E243.1.1.122", {"start": v(79.68, 29.23) * mm, "end": v(79.98, 29.1) * mm});
            skLineSegment(sketch, "E243.1.1.123", {"start": v(82.46, 31.2) * mm, "end": v(81.2, 31.9) * mm});
            skLineSegment(sketch, "E243.1.1.124", {"start": v(83.57, 30.3) * mm, "end": v(82.46, 31.2) * mm});
            skLineSegment(sketch, "E243.1.1.125", {"start": v(56.35, 27.08) * mm, "end": v(56.9, 27.9) * mm});
            skLineSegment(sketch, "E243.1.1.126", {"start": v(53.82, 28.79) * mm, "end": v(53.29, 27.68) * mm});
            skLineSegment(sketch, "E243.1.1.127", {"start": v(62, 20.92) * mm, "end": v(61.16, 20.66) * mm});
            skLineSegment(sketch, "E243.1.1.128", {"start": v(41.16, 31) * mm, "end": v(41.63, 31.44) * mm});
            skLineSegment(sketch, "E243.1.1.129", {"start": v(74.37, 27.09) * mm, "end": v(74.92, 27.91) * mm});
            skLineSegment(sketch, "E243.1.1.130", {"start": v(54.54, 29.81) * mm, "end": v(53.82, 28.79) * mm});
            skLineSegment(sketch, "E243.1.1.131", {"start": v(81.96, 22.53) * mm, "end": v(81.42, 21.87) * mm});
            skLineSegment(sketch, "E243.1.1.132", {"start": v(60.02, 32.48) * mm, "end": v(58.8, 32.33) * mm});
            skLineSegment(sketch, "E243.1.1.133", {"start": v(56.06, 18.84) * mm, "end": v(57.12, 18.23) * mm});
            skLineSegment(sketch, "E243.1.1.134", {"start": v(58.8, 32.33) * mm, "end": v(57.62, 32) * mm});
            skLineSegment(sketch, "E243.1.1.135", {"start": v(81.1, 28.43) * mm, "end": v(81.97, 27.47) * mm});
            skLineSegment(sketch, "E243.1.1.136", {"start": v(56.9, 27.9) * mm, "end": v(57.13, 28.14) * mm});
            skLineSegment(sketch, "E243.1.1.137", {"start": v(56.3, 23) * mm, "end": v(56.17, 23.3) * mm});
            skLineSegment(sketch, "E243.1.1.138", {"start": v(72.52, 29.77) * mm, "end": v(71.89, 28.87) * mm});
            skLineSegment(sketch, "E243.1.1.139", {"start": v(85.43, 22.82) * mm, "end": v(85.58, 23.5) * mm});
            skLineSegment(sketch, "E243.1.1.140", {"start": v(57.8, 21.32) * mm, "end": v(56.85, 22.18) * mm});
            skLineSegment(sketch, "E243.1.1.141", {"start": v(55.1, 19.61) * mm, "end": v(56.06, 18.84) * mm});
            skLineSegment(sketch, "E243.1.1.142", {"start": v(41.66, 27.31) * mm, "end": v(41.2, 26.38) * mm});
            skLineSegment(sketch, "E243.1.1.143", {"start": v(98.72, 37.37) * mm, "end": v(99.1, 37.95) * mm});
            skLineSegment(sketch, "E243.1.1.144", {"start": v(85.6, 26.51) * mm, "end": v(85.17, 27.92) * mm});
            skLineSegment(sketch, "E243.1.1.145", {"start": v(47.21, 20.06) * mm, "end": v(47.6, 20.63) * mm});
            skLineSegment(sketch, "E243.1.1.146", {"start": v(99.68, 35) * mm, "end": v(99.1, 35.38) * mm});
            skLineSegment(sketch, "E243.1.1.147", {"start": v(71.28, 27.6) * mm, "end": v(71.03, 26.8) * mm});
            skLineSegment(sketch, "E243.1.1.148", {"start": v(50.56, 18.64) * mm, "end": v(50.17, 18.07) * mm});
            skLineSegment(sketch, "E243.1.1.149", {"start": v(49.6, 21.02) * mm, "end": v(50.17, 20.63) * mm});
            skLineSegment(sketch, "E243.1.1.150", {"start": v(101.1, 38.34) * mm, "end": v(101.67, 37.95) * mm});
            skLineSegment(sketch, "E243.1.1.151", {"start": v(44.38, 32.52) * mm, "end": v(45.16, 32.63) * mm});
            skLineSegment(sketch, "E243.1.1.152", {"start": v(102.06, 35.96) * mm, "end": v(101.67, 35.38) * mm});
            skLineSegment(sketch, "E243.1.1.153", {"start": v(44.84, 29.3) * mm, "end": v(43.87, 29.06) * mm});
            skLineSegment(sketch, "E243.1.1.154", {"start": v(48.18, 17.68) * mm, "end": v(47.6, 18.07) * mm});
            skLineSegment(sketch, "E243.1.1.155", {"start": v(73.2, 19.53) * mm, "end": v(73.85, 19) * mm});
            skLineSegment(sketch, "E243.1.1.156", {"start": v(46.67, 32.61) * mm, "end": v(47.2, 32.48) * mm});
            skLineSegment(sketch, "E243.1.1.157", {"start": v(78.29, 32.48) * mm, "end": v(78, 32.48) * mm});
            skLineSegment(sketch, "E243.1.1.158", {"start": v(59.94, 20.57) * mm, "end": v(58.97, 20.76) * mm});
            skLineSegment(sketch, "E243.1.1.159", {"start": v(78.66, 32.48) * mm, "end": v(78.29, 32.48) * mm});
            skLineSegment(sketch, "E243.1.1.160", {"start": v(99.68, 38.34) * mm, "end": v(100.21, 38.48) * mm});
            skLineSegment(sketch, "E243.1.1.161", {"start": v(78.5, 20.57) * mm, "end": v(78.29, 20.57) * mm});
            skLineSegment(sketch, "E243.1.1.162", {"start": v(71.89, 28.87) * mm, "end": v(71.49, 28.13) * mm});
            skLineSegment(sketch, "E243.1.1.163", {"start": v(45.92, 32.66) * mm, "end": v(46.1, 32.66) * mm});
            skLineSegment(sketch, "E243.1.1.164", {"start": v(50.7, 19.53) * mm, "end": v(50.7, 19.35) * mm});
            skLineSegment(sketch, "E243.1.1.165", {"start": v(72.8, 19.92) * mm, "end": v(73, 19.72) * mm});
            skLineSegment(sketch, "E243.1.1.166", {"start": v(100.21, 34.85) * mm, "end": v(99.68, 35) * mm});
            skLineSegment(sketch, "E243.1.1.167", {"start": v(46.62, 29.35) * mm, "end": v(46.04, 29.39) * mm});
            skLineSegment(sketch, "E243.1.1.168", {"start": v(50.56, 20.06) * mm, "end": v(50.7, 19.53) * mm});
            skLineSegment(sketch, "E243.1.1.169", {"start": v(100.21, 38.48) * mm, "end": v(100.39, 38.48) * mm});
            skLineSegment(sketch, "E243.1.1.170", {"start": v(79.18, 20.66) * mm, "end": v(78.5, 20.57) * mm});
            skLineSegment(sketch, "E243.1.1.171", {"start": v(60.74, 17.55) * mm, "end": v(61.7, 17.66) * mm});
            skLineSegment(sketch, "E243.1.1.172", {"start": v(47.2, 32.48) * mm, "end": v(47.3, 32.44) * mm});
            skLineSegment(sketch, "E243.1.1.173", {"start": v(64.42, 23.5) * mm, "end": v(64.35, 23.28) * mm});
            skLineSegment(sketch, "E243.1.1.174", {"start": v(55.69, 30.92) * mm, "end": v(55.45, 30.71) * mm});
            skLineSegment(sketch, "E243.1.1.175", {"start": v(46.1, 32.66) * mm, "end": v(46.67, 32.61) * mm});
            skLineSegment(sketch, "E243.1.1.176", {"start": v(45.16, 32.63) * mm, "end": v(45.73, 32.66) * mm});
            skLineSegment(sketch, "E243.1.1.177", {"start": v(45.73, 32.66) * mm, "end": v(45.92, 32.66) * mm});
            skLineSegment(sketch, "E243.1.1.178", {"start": v(40.93, 25.26) * mm, "end": v(40.83, 24.28) * mm});
            skLineSegment(sketch, "E243.1.1.179", {"start": v(100.57, 38.48) * mm, "end": v(101.1, 38.34) * mm});
            skLineSegment(sketch, "E243.1.1.180", {"start": v(77.96, 20.57) * mm, "end": v(76.99, 20.77) * mm});
            skLineSegment(sketch, "E243.1.1.181", {"start": v(61.67, 29.22) * mm, "end": v(61.97, 29.1) * mm});
            skLineSegment(sketch, "E243.1.1.182", {"start": v(64.45, 31.21) * mm, "end": v(63.61, 31.69) * mm});
            skLineSegment(sketch, "E243.1.1.183", {"start": v(64.7, 31.02) * mm, "end": v(64.45, 31.21) * mm});
            skLineSegment(sketch, "E243.1.1.184", {"start": v(45.65, 29.39) * mm, "end": v(44.84, 29.3) * mm});
            skLineSegment(sketch, "E243.1.1.185", {"start": v(100.39, 34.85) * mm, "end": v(100.21, 34.85) * mm});
            skLineSegment(sketch, "E243.1.1.186", {"start": v(100.57, 34.85) * mm, "end": v(100.39, 34.85) * mm});
            skLineSegment(sketch, "E243.1.1.187", {"start": v(74.19, 23.31) * mm, "end": v(74.11, 23.5) * mm});
            skLineSegment(sketch, "E243.1.1.188", {"start": v(56.49, 31.45) * mm, "end": v(55.69, 30.92) * mm});
            skLineSegment(sketch, "E243.1.1.189", {"start": v(50.7, 19.35) * mm, "end": v(50.7, 19.17) * mm});
            skLineSegment(sketch, "E243.1.1.190", {"start": v(53.6, 21.64) * mm, "end": v(53.74, 21.35) * mm});
            skLineSegment(sketch, "E243.1.1.191", {"start": v(47.07, 19.17) * mm, "end": v(47.07, 19.35) * mm});
            skLineSegment(sketch, "E243.1.1.192", {"start": v(61.7, 17.66) * mm, "end": v(62, 17.74) * mm});
            skLineSegment(sketch, "E243.1.1.193", {"start": v(78, 32.48) * mm, "end": v(77.17, 32.4) * mm});
            skLineSegment(sketch, "E243.1.1.194", {"start": v(53.46, 21.92) * mm, "end": v(53.6, 21.64) * mm});
            skLineSegment(sketch, "E243.1.1.195", {"start": v(47.07, 19.53) * mm, "end": v(47.21, 20.06) * mm});
            skLineSegment(sketch, "E243.1.1.196", {"start": v(71.38, 27.87) * mm, "end": v(71.28, 27.6) * mm});
            skLineSegment(sketch, "E243.1.1.197", {"start": v(40.83, 24.28) * mm, "end": v(40.83, 23.96) * mm});
            skLineSegment(sketch, "E243.1.1.198", {"start": v(85.6, 26.5) * mm, "end": v(85.6, 26.51) * mm});
            skLineSegment(sketch, "E243.1.1.199", {"start": v(62, 17.74) * mm, "end": v(62.3, 17.81) * mm});
            skLineSegment(sketch, "E243.1.1.200", {"start": v(47.21, 18.64) * mm, "end": v(47.07, 19.17) * mm});
            skLineSegment(sketch, "E243.1.1.201", {"start": v(55.2, 30.5) * mm, "end": v(54.54, 29.81) * mm});
            skLineSegment(sketch, "E243.1.1.202", {"start": v(82.37, 23.28) * mm, "end": v(81.96, 22.53) * mm});
            skLineSegment(sketch, "E243.1.1.203", {"start": v(74.87, 22.18) * mm, "end": v(74.31, 23.01) * mm});
            skLineSegment(sketch, "E243.1.1.204", {"start": v(61.97, 29.1) * mm, "end": v(62.27, 28.98) * mm});
            skLineSegment(sketch, "E243.1.1.205", {"start": v(100.39, 38.48) * mm, "end": v(100.57, 38.48) * mm});
            skLineSegment(sketch, "E243.1.1.206", {"start": v(60.7, 29.42) * mm, "end": v(61.67, 29.22) * mm});
            skLineSegment(sketch, "E243.1.1.207", {"start": v(78.29, 20.57) * mm, "end": v(77.96, 20.57) * mm});
            skLineSegment(sketch, "E243.1.1.208", {"start": v(53.12, 22.82) * mm, "end": v(53.46, 21.92) * mm});
            skLineSegment(sketch, "E243.1.1.209", {"start": v(71.49, 28.13) * mm, "end": v(71.38, 27.87) * mm});
            skLineSegment(sketch, "E243.1.1.210", {"start": v(46.04, 29.39) * mm, "end": v(45.92, 29.39) * mm});
            skLineSegment(sketch, "E243.1.1.211", {"start": v(101.1, 35) * mm, "end": v(100.57, 34.85) * mm});
            skLineSegment(sketch, "E243.1.1.212", {"start": v(64.35, 23.28) * mm, "end": v(63.94, 22.53) * mm});
            skLineSegment(sketch, "E243.1.1.213", {"start": v(47.19, 29.25) * mm, "end": v(46.62, 29.35) * mm});
            skLineSegment(sketch, "E243.1.1.214", {"start": v(74.31, 23.01) * mm, "end": v(74.19, 23.31) * mm});
            skLineSegment(sketch, "E243.1.1.215", {"start": v(72.27, 20.57) * mm, "end": v(72.8, 19.92) * mm});
            skLineSegment(sketch, "E243.1.1.216", {"start": v(50.7, 19.17) * mm, "end": v(50.56, 18.64) * mm});
            skLineSegment(sketch, "E243.1.1.217", {"start": v(82.44, 23.5) * mm, "end": v(82.37, 23.28) * mm});
            skLineSegment(sketch, "E243.1.1.218", {"start": v(73, 19.72) * mm, "end": v(73.2, 19.53) * mm});
            skLineSegment(sketch, "E243.1.1.219", {"start": v(47.07, 19.35) * mm, "end": v(47.07, 19.53) * mm});
            skLineSegment(sketch, "E243.1.1.220", {"start": v(55.45, 30.71) * mm, "end": v(55.2, 30.5) * mm});
            skLineSegment(sketch, "E243.1.1.221", {"start": v(47.3, 29.23) * mm, "end": v(47.19, 29.25) * mm});
            skLineSegment(sketch, "E243.1.1.222", {"start": v(45.92, 29.39) * mm, "end": v(45.65, 29.39) * mm});
            skLineSegment(sketch, "E243.1.1.223", {"start": v(61.16, 20.66) * mm, "end": v(60.5, 20.57) * mm});
            skLineSegment(sketch, "E243.1.1.224", {"start": v(48.18, 21.02) * mm, "end": v(48.71, 21.17) * mm});
            skLineSegment(sketch, "E243.1.1.225", {"start": v(102.2, 36.49) * mm, "end": v(102.06, 35.96) * mm});
            skLineSegment(sketch, "E243.1.1.226", {"start": v(48.71, 21.17) * mm, "end": v(48.89, 21.17) * mm});
            skLineSegment(sketch, "E243.1.1.227", {"start": v(48.71, 17.53) * mm, "end": v(48.18, 17.68) * mm});
            skLineSegment(sketch, "E243.1.1.228", {"start": v(49.6, 17.68) * mm, "end": v(49.06, 17.53) * mm});
            skLineSegment(sketch, "E243.1.1.229", {"start": v(60.27, 20.57) * mm, "end": v(60.27, 20.57) * mm});
            skLineSegment(sketch, "E243.1.1.230", {"start": v(98.57, 36.84) * mm, "end": v(98.72, 37.37) * mm});
            skLineSegment(sketch, "E243.1.1.231", {"start": v(60.5, 20.57) * mm, "end": v(60.27, 20.57) * mm});
            skLineSegment(sketch, "E243.1.1.232", {"start": v(49.06, 21.17) * mm, "end": v(49.6, 21.02) * mm});
            skLineSegment(sketch, "E243.1.1.233", {"start": v(98.57, 36.66) * mm, "end": v(98.57, 36.84) * mm});
            skLineSegment(sketch, "E243.1.1.234", {"start": v(98.72, 35.96) * mm, "end": v(98.57, 36.49) * mm});
            skLineSegment(sketch, "E243.1.1.235", {"start": v(102.2, 36.84) * mm, "end": v(102.2, 36.66) * mm});
            skLineSegment(sketch, "E243.1.1.236", {"start": v(48.89, 17.53) * mm, "end": v(48.71, 17.53) * mm});
            skLineSegment(sketch, "E243.1.1.237", {"start": v(102.06, 37.37) * mm, "end": v(102.2, 36.84) * mm});
            skLineSegment(sketch, "E243.1.1.238", {"start": v(49.06, 17.53) * mm, "end": v(48.89, 17.53) * mm});
            skLineSegment(sketch, "E243.1.1.239", {"start": v(48.89, 21.17) * mm, "end": v(49.06, 21.17) * mm});
            skLineSegment(sketch, "E243.1.1.240", {"start": v(60.27, 20.57) * mm, "end": v(59.94, 20.57) * mm});
            skLineSegment(sketch, "E243.1.1.241", {"start": v(98.57, 36.49) * mm, "end": v(98.57, 36.66) * mm});
            skLineSegment(sketch, "E243.1.1.242", {"start": v(102.2, 36.66) * mm, "end": v(102.2, 36.49) * mm});
            skLineSegment(sketch, "E243.1.2.0", {"start": v(89.98, 59.58) * mm, "end": v(89.98, 47.5) * mm});
            skLineSegment(sketch, "E243.1.2.1", {"start": v(89.98, 72.5) * mm, "end": v(89.98, 62.51) * mm});
            skLineSegment(sketch, "E243.1.2.2", {"start": v(47.3, 62.44) * mm, "end": v(47.3, 59.23) * mm});
            skLineSegment(sketch, "E243.1.2.3", {"start": v(96.4, 59.58) * mm, "end": v(96.4, 62.44) * mm});
            skLineSegment(sketch, "E243.1.2.4", {"start": v(96.4, 62.44) * mm, "end": v(93.05, 62.44) * mm});
            skLineSegment(sketch, "E243.1.2.5", {"start": v(82.43, 56.5) * mm, "end": v(85.6, 56.5) * mm});
            skLineSegment(sketch, "E243.1.2.6", {"start": v(52.95, 56.5) * mm, "end": v(56.15, 56.5) * mm});
            skLineSegment(sketch, "E243.1.2.7", {"start": v(37.8, 47.5) * mm, "end": v(37.8, 62.47) * mm});
            skLineSegment(sketch, "E243.1.2.8", {"start": v(40.83, 53.96) * mm, "end": v(40.83, 47.5) * mm});
            skLineSegment(sketch, "E243.1.2.9", {"start": v(70.98, 56.5) * mm, "end": v(74.16, 56.5) * mm});
            skLineSegment(sketch, "E243.1.2.10", {"start": v(70.97, 53.5) * mm, "end": v(74.11, 53.5) * mm});
            skLineSegment(sketch, "E243.1.2.11", {"start": v(82.44, 53.5) * mm, "end": v(85.58, 53.5) * mm});
            skLineSegment(sketch, "E243.1.2.12", {"start": v(64.7, 72.5) * mm, "end": v(64.7, 61.02) * mm});
            skLineSegment(sketch, "E243.1.2.13", {"start": v(93.05, 47.5) * mm, "end": v(93.05, 59.58) * mm});
            skLineSegment(sketch, "E243.1.2.14", {"start": v(37.8, 62.47) * mm, "end": v(40.83, 62.47) * mm});
            skLineSegment(sketch, "E243.1.2.15", {"start": v(40.83, 47.5) * mm, "end": v(37.8, 47.5) * mm});
            skLineSegment(sketch, "E243.1.2.16", {"start": v(87.6, 62.51) * mm, "end": v(87.6, 59.58) * mm});
            skLineSegment(sketch, "E243.1.2.17", {"start": v(67.74, 56.5) * mm, "end": v(67.78, 72.5) * mm});
            skLineSegment(sketch, "E243.1.2.18", {"start": v(67.78, 72.5) * mm, "end": v(64.7, 72.5) * mm});
            skLineSegment(sketch, "E243.1.2.19", {"start": v(89.98, 47.5) * mm, "end": v(93.05, 47.5) * mm});
            skLineSegment(sketch, "E243.1.2.20", {"start": v(64.42, 53.5) * mm, "end": v(67.57, 53.5) * mm});
            skLineSegment(sketch, "E243.1.2.21", {"start": v(52.98, 53.5) * mm, "end": v(56.1, 53.5) * mm});
            skLineSegment(sketch, "E243.1.2.22", {"start": v(93.05, 72.5) * mm, "end": v(89.98, 72.5) * mm});
            skLineSegment(sketch, "E243.1.2.23", {"start": v(93.05, 62.44) * mm, "end": v(93.05, 72.5) * mm});
            skLineSegment(sketch, "E243.1.2.24", {"start": v(64.42, 56.5) * mm, "end": v(67.74, 56.5) * mm});
            skLineSegment(sketch, "E243.1.2.25", {"start": v(93.05, 59.58) * mm, "end": v(96.4, 59.58) * mm});
            skLineSegment(sketch, "E243.1.2.26", {"start": v(65.3, 49.48) * mm, "end": v(66.13, 50.38) * mm});
            skLineSegment(sketch, "E243.1.2.27", {"start": v(53.29, 57.68) * mm, "end": v(52.95, 56.5) * mm});
            skLineSegment(sketch, "E243.1.2.28", {"start": v(99.1, 67.95) * mm, "end": v(99.68, 68.34) * mm});
            skLineSegment(sketch, "E243.1.2.29", {"start": v(56.17, 53.3) * mm, "end": v(56.05, 53.6) * mm});
            skLineSegment(sketch, "E243.1.2.30", {"start": v(75.82, 51.32) * mm, "end": v(74.87, 52.18) * mm});
            skLineSegment(sketch, "E243.1.2.31", {"start": v(66.81, 51.4) * mm, "end": v(67.32, 52.52) * mm});
            skLineSegment(sketch, "E243.1.2.32", {"start": v(87.6, 59.58) * mm, "end": v(89.98, 59.58) * mm});
            skLineSegment(sketch, "E243.1.2.33", {"start": v(63.21, 48.14) * mm, "end": v(64.32, 48.73) * mm});
            skLineSegment(sketch, "E243.1.2.34", {"start": v(77.42, 59.36) * mm, "end": v(78.7, 59.42) * mm});
            skLineSegment(sketch, "E243.1.2.35", {"start": v(74.78, 48.4) * mm, "end": v(75.78, 47.97) * mm});
            skLineSegment(sketch, "E243.1.2.36", {"start": v(63.94, 52.53) * mm, "end": v(63.4, 51.87) * mm});
            skLineSegment(sketch, "E243.1.2.37", {"start": v(85.17, 57.92) * mm, "end": v(84.48, 59.18) * mm});
            skLineSegment(sketch, "E243.1.2.38", {"start": v(84.5, 50.86) * mm, "end": v(85.03, 51.8) * mm});
            skLineSegment(sketch, "E243.1.2.39", {"start": v(71.68, 51.5) * mm, "end": v(72.27, 50.57) * mm});
            skLineSegment(sketch, "E243.1.2.40", {"start": v(42.26, 58.07) * mm, "end": v(41.66, 57.31) * mm});
            skLineSegment(sketch, "E243.1.2.41", {"start": v(43, 58.65) * mm, "end": v(42.26, 58.07) * mm});
            skLineSegment(sketch, "E243.1.2.42", {"start": v(66.13, 50.38) * mm, "end": v(66.81, 51.4) * mm});
            skLineSegment(sketch, "E243.1.2.43", {"start": v(79.8, 62.33) * mm, "end": v(78.66, 62.48) * mm});
            skLineSegment(sketch, "E243.1.2.44", {"start": v(67.32, 52.52) * mm, "end": v(67.57, 53.5) * mm});
            skLineSegment(sketch, "E243.1.2.45", {"start": v(63.4, 51.87) * mm, "end": v(62.75, 51.33) * mm});
            skLineSegment(sketch, "E243.1.2.46", {"start": v(84.48, 59.18) * mm, "end": v(83.57, 60.3) * mm});
            skLineSegment(sketch, "E243.1.2.47", {"start": v(89.98, 62.51) * mm, "end": v(87.6, 62.51) * mm});
            skLineSegment(sketch, "E243.1.2.48", {"start": v(58.97, 50.76) * mm, "end": v(57.8, 51.32) * mm});
            skLineSegment(sketch, "E243.1.2.49", {"start": v(101.67, 67.95) * mm, "end": v(102.06, 67.37) * mm});
            skLineSegment(sketch, "E243.1.2.50", {"start": v(76.99, 50.77) * mm, "end": v(75.82, 51.32) * mm});
            skLineSegment(sketch, "E243.1.2.51", {"start": v(71.24, 52.5) * mm, "end": v(71.68, 51.5) * mm});
            skLineSegment(sketch, "E243.1.2.52", {"start": v(43.61, 62.35) * mm, "end": v(44.38, 62.52) * mm});
            skLineSegment(sketch, "E243.1.2.53", {"start": v(81.14, 48.1) * mm, "end": v(81.4, 48.21) * mm});
            skLineSegment(sketch, "E243.1.2.54", {"start": v(75.15, 58.14) * mm, "end": v(75.38, 58.37) * mm});
            skLineSegment(sketch, "E243.1.2.55", {"start": v(57.36, 58.37) * mm, "end": v(58.2, 58.92) * mm});
            skLineSegment(sketch, "E243.1.2.56", {"start": v(53.74, 51.35) * mm, "end": v(54.27, 50.55) * mm});
            skLineSegment(sketch, "E243.1.2.57", {"start": v(40.83, 60.52) * mm, "end": v(40.9, 60.65) * mm});
            skLineSegment(sketch, "E243.1.2.58", {"start": v(80.01, 50.92) * mm, "end": v(79.18, 50.66) * mm});
            skLineSegment(sketch, "E243.1.2.59", {"start": v(73.28, 60.55) * mm, "end": v(72.52, 59.77) * mm});
            skLineSegment(sketch, "E243.1.2.60", {"start": v(75.78, 47.97) * mm, "end": v(76.83, 47.68) * mm});
            skLineSegment(sketch, "E243.1.2.61", {"start": v(85.03, 51.8) * mm, "end": v(85.43, 52.82) * mm});
            skLineSegment(sketch, "E243.1.2.62", {"start": v(56.85, 52.18) * mm, "end": v(56.3, 53) * mm});
            skLineSegment(sketch, "E243.1.2.63", {"start": v(81.42, 51.87) * mm, "end": v(80.76, 51.33) * mm});
            skLineSegment(sketch, "E243.1.2.64", {"start": v(59.49, 47.58) * mm, "end": v(60.74, 47.55) * mm});
            skLineSegment(sketch, "E243.1.2.65", {"start": v(81.97, 57.47) * mm, "end": v(82.43, 56.5) * mm});
            skLineSegment(sketch, "E243.1.2.66", {"start": v(41.2, 56.38) * mm, "end": v(40.93, 55.26) * mm});
            skLineSegment(sketch, "E243.1.2.67", {"start": v(80.28, 58.98) * mm, "end": v(81.1, 58.43) * mm});
            skLineSegment(sketch, "E243.1.2.68", {"start": v(79.98, 59.1) * mm, "end": v(80.28, 58.98) * mm});
            skLineSegment(sketch, "E243.1.2.69", {"start": v(47.6, 50.63) * mm, "end": v(48.18, 51.02) * mm});
            skLineSegment(sketch, "E243.1.2.70", {"start": v(62.45, 62.15) * mm, "end": v(61.25, 62.42) * mm});
            skLineSegment(sketch, "E243.1.2.71", {"start": v(80.08, 47.75) * mm, "end": v(80.89, 48) * mm});
            skLineSegment(sketch, "E243.1.2.72", {"start": v(79, 47.57) * mm, "end": v(80.08, 47.75) * mm});
            skLineSegment(sketch, "E243.1.2.73", {"start": v(62.75, 51.33) * mm, "end": v(62, 50.92) * mm});
            skLineSegment(sketch, "E243.1.2.74", {"start": v(75.38, 58.37) * mm, "end": v(76.2, 58.92) * mm});
            skLineSegment(sketch, "E243.1.2.75", {"start": v(74.13, 61.22) * mm, "end": v(73.28, 60.55) * mm});
            skLineSegment(sketch, "E243.1.2.76", {"start": v(76.83, 47.68) * mm, "end": v(77.9, 47.54) * mm});
            skLineSegment(sketch, "E243.1.2.77", {"start": v(47.6, 48.07) * mm, "end": v(47.21, 48.64) * mm});
            skLineSegment(sketch, "E243.1.2.78", {"start": v(76.1, 62.15) * mm, "end": v(75.08, 61.76) * mm});
            skLineSegment(sketch, "E243.1.2.79", {"start": v(63.1, 58.42) * mm, "end": v(63.96, 57.47) * mm});
            skLineSegment(sketch, "E243.1.2.80", {"start": v(75.08, 61.76) * mm, "end": v(74.13, 61.22) * mm});
            skLineSegment(sketch, "E243.1.2.81", {"start": v(63.96, 57.47) * mm, "end": v(64.42, 56.5) * mm});
            skLineSegment(sketch, "E243.1.2.82", {"start": v(54.27, 50.55) * mm, "end": v(55.1, 49.61) * mm});
            skLineSegment(sketch, "E243.1.2.83", {"start": v(61.25, 62.42) * mm, "end": v(60.02, 62.48) * mm});
            skLineSegment(sketch, "E243.1.2.84", {"start": v(83.04, 49.25) * mm, "end": v(83.83, 50) * mm});
            skLineSegment(sketch, "E243.1.2.85", {"start": v(59.4, 59.35) * mm, "end": v(60.7, 59.42) * mm});
            skLineSegment(sketch, "E243.1.2.86", {"start": v(63.61, 61.69) * mm, "end": v(62.45, 62.15) * mm});
            skLineSegment(sketch, "E243.1.2.87", {"start": v(70.97, 53.5) * mm, "end": v(71.24, 52.5) * mm});
            skLineSegment(sketch, "E243.1.2.88", {"start": v(80.76, 51.33) * mm, "end": v(80.01, 50.92) * mm});
            skLineSegment(sketch, "E243.1.2.89", {"start": v(73.85, 49) * mm, "end": v(74.78, 48.4) * mm});
            skLineSegment(sketch, "E243.1.2.90", {"start": v(83.83, 50) * mm, "end": v(84.5, 50.86) * mm});
            skLineSegment(sketch, "E243.1.2.91", {"start": v(57.13, 58.14) * mm, "end": v(57.36, 58.37) * mm});
            skLineSegment(sketch, "E243.1.2.92", {"start": v(40.83, 62.47) * mm, "end": v(40.83, 60.52) * mm});
            skLineSegment(sketch, "E243.1.2.93", {"start": v(56.15, 56.5) * mm, "end": v(56.35, 57.08) * mm});
            skLineSegment(sketch, "E243.1.2.94", {"start": v(74.92, 57.91) * mm, "end": v(75.15, 58.14) * mm});
            skLineSegment(sketch, "E243.1.2.95", {"start": v(57.62, 62) * mm, "end": v(56.49, 61.45) * mm});
            skLineSegment(sketch, "E243.1.2.96", {"start": v(57.12, 48.23) * mm, "end": v(58.27, 47.8) * mm});
            skLineSegment(sketch, "E243.1.2.97", {"start": v(50.17, 48.07) * mm, "end": v(49.6, 47.68) * mm});
            skLineSegment(sketch, "E243.1.2.98", {"start": v(99.1, 65.38) * mm, "end": v(98.72, 65.96) * mm});
            skLineSegment(sketch, "E243.1.2.99", {"start": v(81.4, 48.21) * mm, "end": v(82.14, 48.6) * mm});
            skLineSegment(sketch, "E243.1.2.100", {"start": v(42.88, 62.1) * mm, "end": v(43.61, 62.35) * mm});
            skLineSegment(sketch, "E243.1.2.101", {"start": v(76.2, 58.92) * mm, "end": v(77.42, 59.36) * mm});
            skLineSegment(sketch, "E243.1.2.102", {"start": v(77.9, 47.54) * mm, "end": v(79, 47.57) * mm});
            skLineSegment(sketch, "E243.1.2.103", {"start": v(40.9, 60.65) * mm, "end": v(41.16, 61) * mm});
            skLineSegment(sketch, "E243.1.2.104", {"start": v(41.63, 61.44) * mm, "end": v(42.21, 61.8) * mm});
            skLineSegment(sketch, "E243.1.2.105", {"start": v(62.3, 47.81) * mm, "end": v(63.21, 48.14) * mm});
            skLineSegment(sketch, "E243.1.2.106", {"start": v(77.17, 62.4) * mm, "end": v(76.1, 62.15) * mm});
            skLineSegment(sketch, "E243.1.2.107", {"start": v(50.17, 50.63) * mm, "end": v(50.56, 50.06) * mm});
            skLineSegment(sketch, "E243.1.2.108", {"start": v(74.16, 56.5) * mm, "end": v(74.37, 57.09) * mm});
            skLineSegment(sketch, "E243.1.2.109", {"start": v(58.27, 47.8) * mm, "end": v(59.49, 47.58) * mm});
            skLineSegment(sketch, "E243.1.2.110", {"start": v(62.27, 58.98) * mm, "end": v(63.1, 58.42) * mm});
            skLineSegment(sketch, "E243.1.2.111", {"start": v(82.14, 48.6) * mm, "end": v(83.04, 49.25) * mm});
            skLineSegment(sketch, "E243.1.2.112", {"start": v(71.03, 56.8) * mm, "end": v(70.98, 56.5) * mm});
            skLineSegment(sketch, "E243.1.2.113", {"start": v(101.67, 65.38) * mm, "end": v(101.1, 65) * mm});
            skLineSegment(sketch, "E243.1.2.114", {"start": v(43.87, 59.06) * mm, "end": v(43, 58.65) * mm});
            skLineSegment(sketch, "E243.1.2.115", {"start": v(42.21, 61.8) * mm, "end": v(42.88, 62.1) * mm});
            skLineSegment(sketch, "E243.1.2.116", {"start": v(64.32, 48.73) * mm, "end": v(65.3, 49.48) * mm});
            skLineSegment(sketch, "E243.1.2.117", {"start": v(81.2, 61.9) * mm, "end": v(79.8, 62.33) * mm});
            skLineSegment(sketch, "E243.1.2.118", {"start": v(58.2, 58.92) * mm, "end": v(59.4, 59.35) * mm});
            skLineSegment(sketch, "E243.1.2.119", {"start": v(52.98, 53.5) * mm, "end": v(53.12, 52.82) * mm});
            skLineSegment(sketch, "E243.1.2.120", {"start": v(78.7, 59.42) * mm, "end": v(79.68, 59.23) * mm});
            skLineSegment(sketch, "E243.1.2.121", {"start": v(80.89, 48) * mm, "end": v(81.14, 48.1) * mm});
            skLineSegment(sketch, "E243.1.2.122", {"start": v(79.68, 59.23) * mm, "end": v(79.98, 59.1) * mm});
            skLineSegment(sketch, "E243.1.2.123", {"start": v(82.46, 61.2) * mm, "end": v(81.2, 61.9) * mm});
            skLineSegment(sketch, "E243.1.2.124", {"start": v(83.57, 60.3) * mm, "end": v(82.46, 61.2) * mm});
            skLineSegment(sketch, "E243.1.2.125", {"start": v(56.35, 57.08) * mm, "end": v(56.9, 57.9) * mm});
            skLineSegment(sketch, "E243.1.2.126", {"start": v(53.82, 58.79) * mm, "end": v(53.29, 57.68) * mm});
            skLineSegment(sketch, "E243.1.2.127", {"start": v(62, 50.92) * mm, "end": v(61.16, 50.66) * mm});
            skLineSegment(sketch, "E243.1.2.128", {"start": v(41.16, 61) * mm, "end": v(41.63, 61.44) * mm});
            skLineSegment(sketch, "E243.1.2.129", {"start": v(74.37, 57.09) * mm, "end": v(74.92, 57.91) * mm});
            skLineSegment(sketch, "E243.1.2.130", {"start": v(54.54, 59.81) * mm, "end": v(53.82, 58.79) * mm});
            skLineSegment(sketch, "E243.1.2.131", {"start": v(81.96, 52.53) * mm, "end": v(81.42, 51.87) * mm});
            skLineSegment(sketch, "E243.1.2.132", {"start": v(60.02, 62.48) * mm, "end": v(58.8, 62.33) * mm});
            skLineSegment(sketch, "E243.1.2.133", {"start": v(56.06, 48.84) * mm, "end": v(57.12, 48.23) * mm});
            skLineSegment(sketch, "E243.1.2.134", {"start": v(58.8, 62.33) * mm, "end": v(57.62, 62) * mm});
            skLineSegment(sketch, "E243.1.2.135", {"start": v(81.1, 58.43) * mm, "end": v(81.97, 57.47) * mm});
            skLineSegment(sketch, "E243.1.2.136", {"start": v(56.9, 57.9) * mm, "end": v(57.13, 58.14) * mm});
            skLineSegment(sketch, "E243.1.2.137", {"start": v(56.3, 53) * mm, "end": v(56.17, 53.3) * mm});
            skLineSegment(sketch, "E243.1.2.138", {"start": v(72.52, 59.77) * mm, "end": v(71.89, 58.87) * mm});
            skLineSegment(sketch, "E243.1.2.139", {"start": v(85.43, 52.82) * mm, "end": v(85.58, 53.5) * mm});
            skLineSegment(sketch, "E243.1.2.140", {"start": v(57.8, 51.32) * mm, "end": v(56.85, 52.18) * mm});
            skLineSegment(sketch, "E243.1.2.141", {"start": v(55.1, 49.61) * mm, "end": v(56.06, 48.84) * mm});
            skLineSegment(sketch, "E243.1.2.142", {"start": v(41.66, 57.31) * mm, "end": v(41.2, 56.38) * mm});
            skLineSegment(sketch, "E243.1.2.143", {"start": v(98.72, 67.37) * mm, "end": v(99.1, 67.95) * mm});
            skLineSegment(sketch, "E243.1.2.144", {"start": v(85.6, 56.51) * mm, "end": v(85.17, 57.92) * mm});
            skLineSegment(sketch, "E243.1.2.145", {"start": v(47.21, 50.06) * mm, "end": v(47.6, 50.63) * mm});
            skLineSegment(sketch, "E243.1.2.146", {"start": v(99.68, 65) * mm, "end": v(99.1, 65.38) * mm});
            skLineSegment(sketch, "E243.1.2.147", {"start": v(71.28, 57.6) * mm, "end": v(71.03, 56.8) * mm});
            skLineSegment(sketch, "E243.1.2.148", {"start": v(50.56, 48.64) * mm, "end": v(50.17, 48.07) * mm});
            skLineSegment(sketch, "E243.1.2.149", {"start": v(49.6, 51.02) * mm, "end": v(50.17, 50.63) * mm});
            skLineSegment(sketch, "E243.1.2.150", {"start": v(101.1, 68.34) * mm, "end": v(101.67, 67.95) * mm});
            skLineSegment(sketch, "E243.1.2.151", {"start": v(44.38, 62.52) * mm, "end": v(45.16, 62.63) * mm});
            skLineSegment(sketch, "E243.1.2.152", {"start": v(102.06, 65.96) * mm, "end": v(101.67, 65.38) * mm});
            skLineSegment(sketch, "E243.1.2.153", {"start": v(44.84, 59.3) * mm, "end": v(43.87, 59.06) * mm});
            skLineSegment(sketch, "E243.1.2.154", {"start": v(48.18, 47.68) * mm, "end": v(47.6, 48.07) * mm});
            skLineSegment(sketch, "E243.1.2.155", {"start": v(73.2, 49.53) * mm, "end": v(73.85, 49) * mm});
            skLineSegment(sketch, "E243.1.2.156", {"start": v(46.67, 62.61) * mm, "end": v(47.2, 62.48) * mm});
            skLineSegment(sketch, "E243.1.2.157", {"start": v(78.29, 62.48) * mm, "end": v(78, 62.48) * mm});
            skLineSegment(sketch, "E243.1.2.158", {"start": v(59.94, 50.57) * mm, "end": v(58.97, 50.76) * mm});
            skLineSegment(sketch, "E243.1.2.159", {"start": v(78.66, 62.48) * mm, "end": v(78.29, 62.48) * mm});
            skLineSegment(sketch, "E243.1.2.160", {"start": v(99.68, 68.34) * mm, "end": v(100.21, 68.48) * mm});
            skLineSegment(sketch, "E243.1.2.161", {"start": v(78.5, 50.57) * mm, "end": v(78.29, 50.57) * mm});
            skLineSegment(sketch, "E243.1.2.162", {"start": v(71.89, 58.87) * mm, "end": v(71.49, 58.13) * mm});
            skLineSegment(sketch, "E243.1.2.163", {"start": v(45.92, 62.66) * mm, "end": v(46.1, 62.66) * mm});
            skLineSegment(sketch, "E243.1.2.164", {"start": v(50.7, 49.53) * mm, "end": v(50.7, 49.35) * mm});
            skLineSegment(sketch, "E243.1.2.165", {"start": v(72.8, 49.92) * mm, "end": v(73, 49.72) * mm});
            skLineSegment(sketch, "E243.1.2.166", {"start": v(100.21, 64.85) * mm, "end": v(99.68, 65) * mm});
            skLineSegment(sketch, "E243.1.2.167", {"start": v(46.62, 59.35) * mm, "end": v(46.04, 59.39) * mm});
            skLineSegment(sketch, "E243.1.2.168", {"start": v(50.56, 50.06) * mm, "end": v(50.7, 49.53) * mm});
            skLineSegment(sketch, "E243.1.2.169", {"start": v(100.21, 68.48) * mm, "end": v(100.39, 68.48) * mm});
            skLineSegment(sketch, "E243.1.2.170", {"start": v(79.18, 50.66) * mm, "end": v(78.5, 50.57) * mm});
            skLineSegment(sketch, "E243.1.2.171", {"start": v(60.74, 47.55) * mm, "end": v(61.7, 47.66) * mm});
            skLineSegment(sketch, "E243.1.2.172", {"start": v(47.2, 62.48) * mm, "end": v(47.3, 62.44) * mm});
            skLineSegment(sketch, "E243.1.2.173", {"start": v(64.42, 53.5) * mm, "end": v(64.35, 53.28) * mm});
            skLineSegment(sketch, "E243.1.2.174", {"start": v(55.69, 60.92) * mm, "end": v(55.45, 60.71) * mm});
            skLineSegment(sketch, "E243.1.2.175", {"start": v(46.1, 62.66) * mm, "end": v(46.67, 62.61) * mm});
            skLineSegment(sketch, "E243.1.2.176", {"start": v(45.16, 62.63) * mm, "end": v(45.73, 62.66) * mm});
            skLineSegment(sketch, "E243.1.2.177", {"start": v(45.73, 62.66) * mm, "end": v(45.92, 62.66) * mm});
            skLineSegment(sketch, "E243.1.2.178", {"start": v(40.93, 55.26) * mm, "end": v(40.83, 54.28) * mm});
            skLineSegment(sketch, "E243.1.2.179", {"start": v(100.57, 68.48) * mm, "end": v(101.1, 68.34) * mm});
            skLineSegment(sketch, "E243.1.2.180", {"start": v(77.96, 50.57) * mm, "end": v(76.99, 50.77) * mm});
            skLineSegment(sketch, "E243.1.2.181", {"start": v(61.67, 59.22) * mm, "end": v(61.97, 59.1) * mm});
            skLineSegment(sketch, "E243.1.2.182", {"start": v(64.45, 61.21) * mm, "end": v(63.61, 61.69) * mm});
            skLineSegment(sketch, "E243.1.2.183", {"start": v(64.7, 61.02) * mm, "end": v(64.45, 61.21) * mm});
            skLineSegment(sketch, "E243.1.2.184", {"start": v(45.65, 59.39) * mm, "end": v(44.84, 59.3) * mm});
            skLineSegment(sketch, "E243.1.2.185", {"start": v(100.39, 64.85) * mm, "end": v(100.21, 64.85) * mm});
            skLineSegment(sketch, "E243.1.2.186", {"start": v(100.57, 64.85) * mm, "end": v(100.39, 64.85) * mm});
            skLineSegment(sketch, "E243.1.2.187", {"start": v(74.19, 53.31) * mm, "end": v(74.11, 53.5) * mm});
            skLineSegment(sketch, "E243.1.2.188", {"start": v(56.49, 61.45) * mm, "end": v(55.69, 60.92) * mm});
            skLineSegment(sketch, "E243.1.2.189", {"start": v(50.7, 49.35) * mm, "end": v(50.7, 49.17) * mm});
            skLineSegment(sketch, "E243.1.2.190", {"start": v(53.6, 51.64) * mm, "end": v(53.74, 51.35) * mm});
            skLineSegment(sketch, "E243.1.2.191", {"start": v(47.07, 49.17) * mm, "end": v(47.07, 49.35) * mm});
            skLineSegment(sketch, "E243.1.2.192", {"start": v(61.7, 47.66) * mm, "end": v(62, 47.74) * mm});
            skLineSegment(sketch, "E243.1.2.193", {"start": v(78, 62.48) * mm, "end": v(77.17, 62.4) * mm});
            skLineSegment(sketch, "E243.1.2.194", {"start": v(53.46, 51.92) * mm, "end": v(53.6, 51.64) * mm});
            skLineSegment(sketch, "E243.1.2.195", {"start": v(47.07, 49.53) * mm, "end": v(47.21, 50.06) * mm});
            skLineSegment(sketch, "E243.1.2.196", {"start": v(71.38, 57.87) * mm, "end": v(71.28, 57.6) * mm});
            skLineSegment(sketch, "E243.1.2.197", {"start": v(40.83, 54.28) * mm, "end": v(40.83, 53.96) * mm});
            skLineSegment(sketch, "E243.1.2.198", {"start": v(85.6, 56.5) * mm, "end": v(85.6, 56.51) * mm});
            skLineSegment(sketch, "E243.1.2.199", {"start": v(62, 47.74) * mm, "end": v(62.3, 47.81) * mm});
            skLineSegment(sketch, "E243.1.2.200", {"start": v(47.21, 48.64) * mm, "end": v(47.07, 49.17) * mm});
            skLineSegment(sketch, "E243.1.2.201", {"start": v(55.2, 60.5) * mm, "end": v(54.54, 59.81) * mm});
            skLineSegment(sketch, "E243.1.2.202", {"start": v(82.37, 53.28) * mm, "end": v(81.96, 52.53) * mm});
            skLineSegment(sketch, "E243.1.2.203", {"start": v(74.87, 52.18) * mm, "end": v(74.31, 53.01) * mm});
            skLineSegment(sketch, "E243.1.2.204", {"start": v(61.97, 59.1) * mm, "end": v(62.27, 58.98) * mm});
            skLineSegment(sketch, "E243.1.2.205", {"start": v(100.39, 68.48) * mm, "end": v(100.57, 68.48) * mm});
            skLineSegment(sketch, "E243.1.2.206", {"start": v(60.7, 59.42) * mm, "end": v(61.67, 59.22) * mm});
            skLineSegment(sketch, "E243.1.2.207", {"start": v(78.29, 50.57) * mm, "end": v(77.96, 50.57) * mm});
            skLineSegment(sketch, "E243.1.2.208", {"start": v(53.12, 52.82) * mm, "end": v(53.46, 51.92) * mm});
            skLineSegment(sketch, "E243.1.2.209", {"start": v(71.49, 58.13) * mm, "end": v(71.38, 57.87) * mm});
            skLineSegment(sketch, "E243.1.2.210", {"start": v(46.04, 59.39) * mm, "end": v(45.92, 59.39) * mm});
            skLineSegment(sketch, "E243.1.2.211", {"start": v(101.1, 65) * mm, "end": v(100.57, 64.85) * mm});
            skLineSegment(sketch, "E243.1.2.212", {"start": v(64.35, 53.28) * mm, "end": v(63.94, 52.53) * mm});
            skLineSegment(sketch, "E243.1.2.213", {"start": v(47.19, 59.25) * mm, "end": v(46.62, 59.35) * mm});
            skLineSegment(sketch, "E243.1.2.214", {"start": v(74.31, 53.01) * mm, "end": v(74.19, 53.31) * mm});
            skLineSegment(sketch, "E243.1.2.215", {"start": v(72.27, 50.57) * mm, "end": v(72.8, 49.92) * mm});
            skLineSegment(sketch, "E243.1.2.216", {"start": v(50.7, 49.17) * mm, "end": v(50.56, 48.64) * mm});
            skLineSegment(sketch, "E243.1.2.217", {"start": v(82.44, 53.5) * mm, "end": v(82.37, 53.28) * mm});
            skLineSegment(sketch, "E243.1.2.218", {"start": v(73, 49.72) * mm, "end": v(73.2, 49.53) * mm});
            skLineSegment(sketch, "E243.1.2.219", {"start": v(47.07, 49.35) * mm, "end": v(47.07, 49.53) * mm});
            skLineSegment(sketch, "E243.1.2.220", {"start": v(55.45, 60.71) * mm, "end": v(55.2, 60.5) * mm});
            skLineSegment(sketch, "E243.1.2.221", {"start": v(47.3, 59.23) * mm, "end": v(47.19, 59.25) * mm});
            skLineSegment(sketch, "E243.1.2.222", {"start": v(45.92, 59.39) * mm, "end": v(45.65, 59.39) * mm});
            skLineSegment(sketch, "E243.1.2.223", {"start": v(61.16, 50.66) * mm, "end": v(60.5, 50.57) * mm});
            skLineSegment(sketch, "E243.1.2.224", {"start": v(48.18, 51.02) * mm, "end": v(48.71, 51.17) * mm});
            skLineSegment(sketch, "E243.1.2.225", {"start": v(102.2, 66.49) * mm, "end": v(102.06, 65.96) * mm});
            skLineSegment(sketch, "E243.1.2.226", {"start": v(48.71, 51.17) * mm, "end": v(48.89, 51.17) * mm});
            skLineSegment(sketch, "E243.1.2.227", {"start": v(48.71, 47.53) * mm, "end": v(48.18, 47.68) * mm});
            skLineSegment(sketch, "E243.1.2.228", {"start": v(49.6, 47.68) * mm, "end": v(49.06, 47.53) * mm});
            skLineSegment(sketch, "E243.1.2.229", {"start": v(60.27, 50.57) * mm, "end": v(60.27, 50.57) * mm});
            skLineSegment(sketch, "E243.1.2.230", {"start": v(98.57, 66.84) * mm, "end": v(98.72, 67.37) * mm});
            skLineSegment(sketch, "E243.1.2.231", {"start": v(60.5, 50.57) * mm, "end": v(60.27, 50.57) * mm});
            skLineSegment(sketch, "E243.1.2.232", {"start": v(49.06, 51.17) * mm, "end": v(49.6, 51.02) * mm});
            skLineSegment(sketch, "E243.1.2.233", {"start": v(98.57, 66.66) * mm, "end": v(98.57, 66.84) * mm});
            skLineSegment(sketch, "E243.1.2.234", {"start": v(98.72, 65.96) * mm, "end": v(98.57, 66.49) * mm});
            skLineSegment(sketch, "E243.1.2.235", {"start": v(102.2, 66.84) * mm, "end": v(102.2, 66.66) * mm});
            skLineSegment(sketch, "E243.1.2.236", {"start": v(48.89, 47.53) * mm, "end": v(48.71, 47.53) * mm});
            skLineSegment(sketch, "E243.1.2.237", {"start": v(102.06, 67.37) * mm, "end": v(102.2, 66.84) * mm});
            skLineSegment(sketch, "E243.1.2.238", {"start": v(49.06, 47.53) * mm, "end": v(48.89, 47.53) * mm});
            skLineSegment(sketch, "E243.1.2.239", {"start": v(48.89, 51.17) * mm, "end": v(49.06, 51.17) * mm});
            skLineSegment(sketch, "E243.1.2.240", {"start": v(60.27, 50.57) * mm, "end": v(59.94, 50.57) * mm});
            skLineSegment(sketch, "E243.1.2.241", {"start": v(98.57, 66.49) * mm, "end": v(98.57, 66.66) * mm});
            skLineSegment(sketch, "E243.1.2.242", {"start": v(102.2, 66.66) * mm, "end": v(102.2, 66.49) * mm});
            skLineSegment(sketch, "E243.direction1", {"start": v(-32.2, -12.5) * mm, "end": v(37.8, -12.5) * mm, "construction": true});
            skLineSegment(sketch, "E243.direction2", {"start": v(-32.2, -12.5) * mm, "end": v(-32.2, 17.5) * mm, "construction": true});
            skLineSegment(sketch, "E244.bottom", {"start": v(-40, 80) * mm, "end": v(110, 80) * mm});
            skLineSegment(sketch, "E244.top", {"start": v(-40, -20) * mm, "end": v(110, -20) * mm});
            skLineSegment(sketch, "E244.left", {"start": v(-40, 80) * mm, "end": v(-40, -20) * mm});
            skLineSegment(sketch, "E244.right", {"start": v(110, 80) * mm, "end": v(110, -20) * mm});
            skSolve(sketch);
        }
        {
            var Q0;
            Q0=makeQuery(id+"F0.imprint","IMPRINT",FACE,{"disambiguationData":[TD([[makeQuery(id+"F0.imprint","IMPRINT",EDGE,{"derivedFrom":sQuery(id+"F0.wireOp",EDGE,"E0")}),1.0]])]});
            extrude(context, id + "F1", {"entities" : qUnion([Q0]), "depth" : 2 * mm, "offsetDistance" : 25 * mm});
        }
    });
